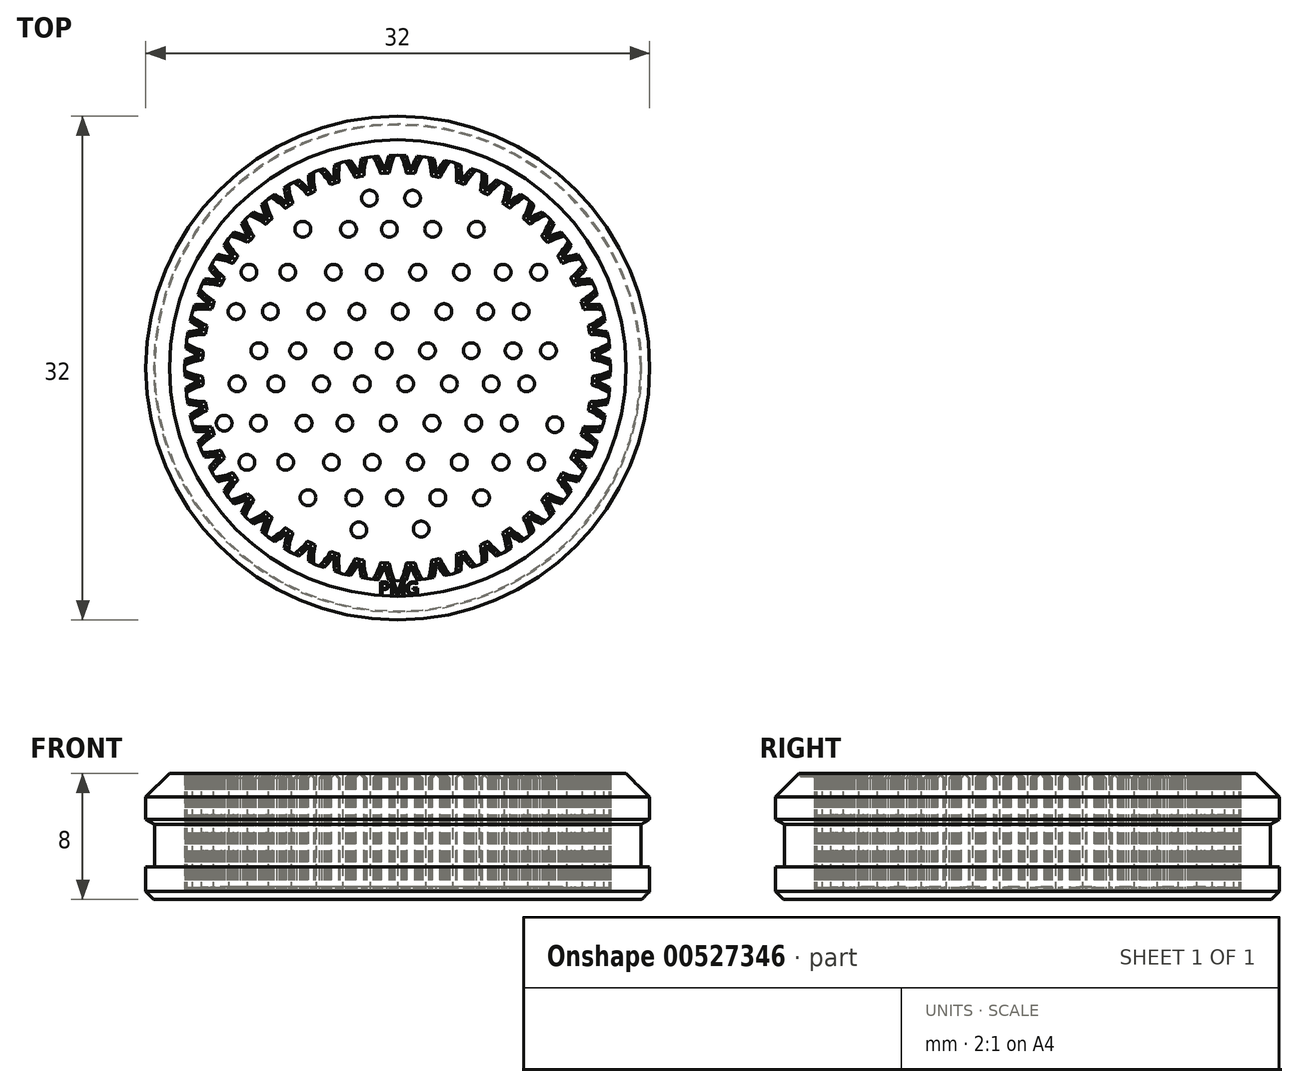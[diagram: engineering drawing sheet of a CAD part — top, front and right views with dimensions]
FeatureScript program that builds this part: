
annotation { "Feature Type Name" : "Feature", "Feature Type Description" : "" }
export const myFeature = defineFeature(function(context is Context, id is Id, definition is map)
    precondition{}
    {
        {
            var Q0;
            Q0=qCreatedBy(makeId("Top.planeOp"),FACE);
            var sketch = newSketch(context, id + "F0", { "sketchPlane" : qUnion([Q0])});
            skLineSegment(sketch, "E0", {"start": v(13.37, -1.96) * mm, "end": v(13.41, -1.77) * mm});
            skLineSegment(sketch, "E1", {"start": v(13.41, -1.77) * mm, "end": v(13.43, -1.57) * mm});
            skLineSegment(sketch, "E2", {"start": v(13.43, -1.57) * mm, "end": v(13.23, -1.46) * mm});
            skLineSegment(sketch, "E3", {"start": v(13.23, -1.46) * mm, "end": v(13.04, -1.36) * mm});
            skLineSegment(sketch, "E4", {"start": v(13.04, -1.36) * mm, "end": v(12.87, -1.28) * mm});
            skLineSegment(sketch, "E5", {"start": v(12.87, -1.28) * mm, "end": v(12.72, -1.21) * mm});
            skLineSegment(sketch, "E6", {"start": v(12.72, -1.21) * mm, "end": v(12.59, -1.16) * mm});
            skLineSegment(sketch, "E7", {"start": v(12.59, -1.16) * mm, "end": v(12.42, -1.11) * mm});
            skLineSegment(sketch, "E8", {"start": v(12.42, -1.11) * mm, "end": v(12.38, -1.09) * mm});
            skLineSegment(sketch, "E9", {"start": v(12.38, -1.09) * mm, "end": v(12.35, -1.06) * mm});
            skLineSegment(sketch, "E10", {"start": v(12.35, -1.06) * mm, "end": v(12.39, -0.56) * mm});
            skLineSegment(sketch, "E11", {"start": v(12.39, -0.56) * mm, "end": v(12.41, -0.54) * mm});
            skLineSegment(sketch, "E12", {"start": v(12.41, -0.54) * mm, "end": v(12.46, -0.52) * mm});
            skLineSegment(sketch, "E13", {"start": v(12.46, -0.52) * mm, "end": v(12.63, -0.49) * mm});
            skLineSegment(sketch, "E14", {"start": v(12.63, -0.49) * mm, "end": v(12.77, -0.46) * mm});
            skLineSegment(sketch, "E15", {"start": v(12.77, -0.46) * mm, "end": v(12.93, -0.41) * mm});
            skLineSegment(sketch, "E16", {"start": v(12.93, -0.41) * mm, "end": v(13.11, -0.36) * mm});
            skLineSegment(sketch, "E17", {"start": v(13.11, -0.36) * mm, "end": v(13.3, -0.28) * mm});
            skLineSegment(sketch, "E18", {"start": v(13.3, -0.28) * mm, "end": v(13.52, -0.2) * mm});
            skLineSegment(sketch, "E19", {"start": v(13.52, -0.2) * mm, "end": v(13.53, 0) * mm});
            skLineSegment(sketch, "E20", {"start": v(13.53, 0) * mm, "end": v(13.52, 0.2) * mm});
            skLineSegment(sketch, "E21", {"start": v(13.52, 0.2) * mm, "end": v(13.3, 0.28) * mm});
            skLineSegment(sketch, "E22", {"start": v(13.3, 0.28) * mm, "end": v(13.11, 0.36) * mm});
            skLineSegment(sketch, "E23", {"start": v(13.11, 0.36) * mm, "end": v(12.93, 0.41) * mm});
            skLineSegment(sketch, "E24", {"start": v(12.93, 0.41) * mm, "end": v(12.77, 0.46) * mm});
            skLineSegment(sketch, "E25", {"start": v(12.77, 0.46) * mm, "end": v(12.63, 0.49) * mm});
            skLineSegment(sketch, "E26", {"start": v(12.63, 0.49) * mm, "end": v(12.46, 0.52) * mm});
            skLineSegment(sketch, "E27", {"start": v(12.46, 0.52) * mm, "end": v(12.41, 0.54) * mm});
            skLineSegment(sketch, "E28", {"start": v(12.41, 0.54) * mm, "end": v(12.39, 0.56) * mm});
            skLineSegment(sketch, "E29", {"start": v(12.39, 0.56) * mm, "end": v(12.35, 1.06) * mm});
            skLineSegment(sketch, "E30", {"start": v(12.35, 1.06) * mm, "end": v(12.38, 1.09) * mm});
            skLineSegment(sketch, "E31", {"start": v(12.38, 1.09) * mm, "end": v(12.42, 1.11) * mm});
            skLineSegment(sketch, "E32", {"start": v(12.42, 1.11) * mm, "end": v(12.59, 1.16) * mm});
            skLineSegment(sketch, "E33", {"start": v(12.59, 1.16) * mm, "end": v(12.72, 1.21) * mm});
            skLineSegment(sketch, "E34", {"start": v(12.72, 1.21) * mm, "end": v(12.87, 1.28) * mm});
            skLineSegment(sketch, "E35", {"start": v(12.87, 1.28) * mm, "end": v(13.04, 1.36) * mm});
            skLineSegment(sketch, "E36", {"start": v(13.04, 1.36) * mm, "end": v(13.23, 1.46) * mm});
            skLineSegment(sketch, "E37", {"start": v(13.23, 1.46) * mm, "end": v(13.43, 1.57) * mm});
            skLineSegment(sketch, "E38", {"start": v(13.43, 1.57) * mm, "end": v(13.41, 1.77) * mm});
            skLineSegment(sketch, "E39", {"start": v(13.41, 1.77) * mm, "end": v(13.37, 1.96) * mm});
            skLineSegment(sketch, "E40", {"start": v(13.37, 1.96) * mm, "end": v(13.16, 2.02) * mm});
            skLineSegment(sketch, "E41", {"start": v(13.16, 2.02) * mm, "end": v(12.95, 2.07) * mm});
            skLineSegment(sketch, "E42", {"start": v(12.95, 2.07) * mm, "end": v(12.77, 2.1) * mm});
            skLineSegment(sketch, "E43", {"start": v(12.77, 2.1) * mm, "end": v(12.6, 2.12) * mm});
            skLineSegment(sketch, "E44", {"start": v(12.6, 2.12) * mm, "end": v(12.46, 2.13) * mm});
            skLineSegment(sketch, "E45", {"start": v(12.46, 2.13) * mm, "end": v(12.29, 2.14) * mm});
            skLineSegment(sketch, "E46", {"start": v(12.29, 2.14) * mm, "end": v(12.23, 2.15) * mm});
            skLineSegment(sketch, "E47", {"start": v(12.23, 2.15) * mm, "end": v(12.2, 2.17) * mm});
            skLineSegment(sketch, "E48", {"start": v(12.2, 2.17) * mm, "end": v(12.1, 2.66) * mm});
            skLineSegment(sketch, "E49", {"start": v(12.1, 2.66) * mm, "end": v(12.13, 2.7) * mm});
            skLineSegment(sketch, "E50", {"start": v(12.13, 2.7) * mm, "end": v(12.17, 2.72) * mm});
            skLineSegment(sketch, "E51", {"start": v(12.17, 2.72) * mm, "end": v(12.33, 2.8) * mm});
            skLineSegment(sketch, "E52", {"start": v(12.33, 2.8) * mm, "end": v(12.46, 2.86) * mm});
            skLineSegment(sketch, "E53", {"start": v(12.46, 2.86) * mm, "end": v(12.6, 2.95) * mm});
            skLineSegment(sketch, "E54", {"start": v(12.6, 2.95) * mm, "end": v(12.76, 3.05) * mm});
            skLineSegment(sketch, "E55", {"start": v(12.76, 3.05) * mm, "end": v(12.93, 3.17) * mm});
            skLineSegment(sketch, "E56", {"start": v(12.93, 3.17) * mm, "end": v(13.1, 3.3) * mm});
            skLineSegment(sketch, "E57", {"start": v(13.1, 3.3) * mm, "end": v(13.07, 3.5) * mm});
            skLineSegment(sketch, "E58", {"start": v(13.07, 3.5) * mm, "end": v(13, 3.69) * mm});
            skLineSegment(sketch, "E59", {"start": v(13, 3.69) * mm, "end": v(12.78, 3.72) * mm});
            skLineSegment(sketch, "E60", {"start": v(12.78, 3.72) * mm, "end": v(12.57, 3.74) * mm});
            skLineSegment(sketch, "E61", {"start": v(12.57, 3.74) * mm, "end": v(12.38, 3.75) * mm});
            skLineSegment(sketch, "E62", {"start": v(12.38, 3.75) * mm, "end": v(12.22, 3.75) * mm});
            skLineSegment(sketch, "E63", {"start": v(12.22, 3.75) * mm, "end": v(12.08, 3.74) * mm});
            skLineSegment(sketch, "E64", {"start": v(12.08, 3.74) * mm, "end": v(11.9, 3.73) * mm});
            skLineSegment(sketch, "E65", {"start": v(11.9, 3.73) * mm, "end": v(11.85, 3.73) * mm});
            skLineSegment(sketch, "E66", {"start": v(11.85, 3.73) * mm, "end": v(11.82, 3.75) * mm});
            skLineSegment(sketch, "E67", {"start": v(11.82, 3.75) * mm, "end": v(11.66, 4.22) * mm});
            skLineSegment(sketch, "E68", {"start": v(11.66, 4.22) * mm, "end": v(11.67, 4.25) * mm});
            skLineSegment(sketch, "E69", {"start": v(11.67, 4.25) * mm, "end": v(11.71, 4.29) * mm});
            skLineSegment(sketch, "E70", {"start": v(11.71, 4.29) * mm, "end": v(11.86, 4.38) * mm});
            skLineSegment(sketch, "E71", {"start": v(11.86, 4.38) * mm, "end": v(11.97, 4.47) * mm});
            skLineSegment(sketch, "E72", {"start": v(11.97, 4.47) * mm, "end": v(12.1, 4.57) * mm});
            skLineSegment(sketch, "E73", {"start": v(12.1, 4.57) * mm, "end": v(12.25, 4.69) * mm});
            skLineSegment(sketch, "E74", {"start": v(12.25, 4.69) * mm, "end": v(12.4, 4.83) * mm});
            skLineSegment(sketch, "E75", {"start": v(12.4, 4.83) * mm, "end": v(12.56, 4.99) * mm});
            skLineSegment(sketch, "E76", {"start": v(12.56, 4.99) * mm, "end": v(12.5, 5.18) * mm});
            skLineSegment(sketch, "E77", {"start": v(12.5, 5.18) * mm, "end": v(12.41, 5.36) * mm});
            skLineSegment(sketch, "E78", {"start": v(12.41, 5.36) * mm, "end": v(12.19, 5.36) * mm});
            skLineSegment(sketch, "E79", {"start": v(12.19, 5.36) * mm, "end": v(11.98, 5.35) * mm});
            skLineSegment(sketch, "E80", {"start": v(11.98, 5.35) * mm, "end": v(11.79, 5.33) * mm});
            skLineSegment(sketch, "E81", {"start": v(11.79, 5.33) * mm, "end": v(11.62, 5.31) * mm});
            skLineSegment(sketch, "E82", {"start": v(11.62, 5.31) * mm, "end": v(11.49, 5.29) * mm});
            skLineSegment(sketch, "E83", {"start": v(11.49, 5.29) * mm, "end": v(11.31, 5.25) * mm});
            skLineSegment(sketch, "E84", {"start": v(11.31, 5.25) * mm, "end": v(11.26, 5.25) * mm});
            skLineSegment(sketch, "E85", {"start": v(11.26, 5.25) * mm, "end": v(11.23, 5.26) * mm});
            skLineSegment(sketch, "E86", {"start": v(11.23, 5.26) * mm, "end": v(11, 5.7) * mm});
            skLineSegment(sketch, "E87", {"start": v(11, 5.7) * mm, "end": v(11.02, 5.74) * mm});
            skLineSegment(sketch, "E88", {"start": v(11.02, 5.74) * mm, "end": v(11.05, 5.78) * mm});
            skLineSegment(sketch, "E89", {"start": v(11.05, 5.78) * mm, "end": v(11.19, 5.9) * mm});
            skLineSegment(sketch, "E90", {"start": v(11.19, 5.9) * mm, "end": v(11.29, 5.99) * mm});
            skLineSegment(sketch, "E91", {"start": v(11.29, 5.99) * mm, "end": v(11.4, 6.1) * mm});
            skLineSegment(sketch, "E92", {"start": v(11.4, 6.1) * mm, "end": v(11.53, 6.25) * mm});
            skLineSegment(sketch, "E93", {"start": v(11.53, 6.25) * mm, "end": v(11.67, 6.4) * mm});
            skLineSegment(sketch, "E94", {"start": v(11.67, 6.4) * mm, "end": v(11.8, 6.59) * mm});
            skLineSegment(sketch, "E95", {"start": v(11.8, 6.59) * mm, "end": v(11.72, 6.76) * mm});
            skLineSegment(sketch, "E96", {"start": v(11.72, 6.76) * mm, "end": v(11.6, 6.93) * mm});
            skLineSegment(sketch, "E97", {"start": v(11.6, 6.93) * mm, "end": v(11.38, 6.9) * mm});
            skLineSegment(sketch, "E98", {"start": v(11.38, 6.9) * mm, "end": v(11.18, 6.86) * mm});
            skLineSegment(sketch, "E99", {"start": v(11.18, 6.86) * mm, "end": v(11, 6.82) * mm});
            skLineSegment(sketch, "E100", {"start": v(11, 6.82) * mm, "end": v(10.83, 6.78) * mm});
            skLineSegment(sketch, "E101", {"start": v(10.83, 6.78) * mm, "end": v(10.7, 6.74) * mm});
            skLineSegment(sketch, "E102", {"start": v(10.7, 6.74) * mm, "end": v(10.53, 6.68) * mm});
            skLineSegment(sketch, "E103", {"start": v(10.53, 6.68) * mm, "end": v(10.48, 6.67) * mm});
            skLineSegment(sketch, "E104", {"start": v(10.48, 6.67) * mm, "end": v(10.45, 6.68) * mm});
            skLineSegment(sketch, "E105", {"start": v(10.45, 6.68) * mm, "end": v(10.17, 7.1) * mm});
            skLineSegment(sketch, "E106", {"start": v(10.17, 7.1) * mm, "end": v(10.17, 7.13) * mm});
            skLineSegment(sketch, "E107", {"start": v(10.17, 7.13) * mm, "end": v(10.2, 7.17) * mm});
            skLineSegment(sketch, "E108", {"start": v(10.2, 7.17) * mm, "end": v(10.32, 7.3) * mm});
            skLineSegment(sketch, "E109", {"start": v(10.32, 7.3) * mm, "end": v(10.41, 7.41) * mm});
            skLineSegment(sketch, "E110", {"start": v(10.41, 7.41) * mm, "end": v(10.51, 7.54) * mm});
            skLineSegment(sketch, "E111", {"start": v(10.51, 7.54) * mm, "end": v(10.62, 7.7) * mm});
            skLineSegment(sketch, "E112", {"start": v(10.62, 7.7) * mm, "end": v(10.73, 7.88) * mm});
            skLineSegment(sketch, "E113", {"start": v(10.73, 7.88) * mm, "end": v(10.84, 8.07) * mm});
            skLineSegment(sketch, "E114", {"start": v(10.84, 8.07) * mm, "end": v(10.73, 8.24) * mm});
            skLineSegment(sketch, "E115", {"start": v(10.73, 8.24) * mm, "end": v(10.6, 8.39) * mm});
            skLineSegment(sketch, "E116", {"start": v(10.6, 8.39) * mm, "end": v(10.39, 8.33) * mm});
            skLineSegment(sketch, "E117", {"start": v(10.39, 8.33) * mm, "end": v(10.18, 8.26) * mm});
            skLineSegment(sketch, "E118", {"start": v(10.18, 8.26) * mm, "end": v(10, 8.2) * mm});
            skLineSegment(sketch, "E119", {"start": v(10, 8.2) * mm, "end": v(9.85, 8.14) * mm});
            skLineSegment(sketch, "E120", {"start": v(9.85, 8.14) * mm, "end": v(9.73, 8.08) * mm});
            skLineSegment(sketch, "E121", {"start": v(9.73, 8.08) * mm, "end": v(9.57, 8) * mm});
            skLineSegment(sketch, "E122", {"start": v(9.57, 8) * mm, "end": v(9.52, 7.98) * mm});
            skLineSegment(sketch, "E123", {"start": v(9.52, 7.98) * mm, "end": v(9.48, 7.99) * mm});
            skLineSegment(sketch, "E124", {"start": v(9.48, 7.99) * mm, "end": v(9.16, 8.36) * mm});
            skLineSegment(sketch, "E125", {"start": v(9.16, 8.36) * mm, "end": v(9.16, 8.4) * mm});
            skLineSegment(sketch, "E126", {"start": v(9.16, 8.4) * mm, "end": v(9.18, 8.44) * mm});
            skLineSegment(sketch, "E127", {"start": v(9.18, 8.44) * mm, "end": v(9.28, 8.59) * mm});
            skLineSegment(sketch, "E128", {"start": v(9.28, 8.59) * mm, "end": v(9.35, 8.7) * mm});
            skLineSegment(sketch, "E129", {"start": v(9.35, 8.7) * mm, "end": v(9.44, 8.85) * mm});
            skLineSegment(sketch, "E130", {"start": v(9.44, 8.85) * mm, "end": v(9.52, 9.02) * mm});
            skLineSegment(sketch, "E131", {"start": v(9.52, 9.02) * mm, "end": v(9.61, 9.2) * mm});
            skLineSegment(sketch, "E132", {"start": v(9.61, 9.2) * mm, "end": v(9.7, 9.42) * mm});
            skLineSegment(sketch, "E133", {"start": v(9.7, 9.42) * mm, "end": v(9.57, 9.57) * mm});
            skLineSegment(sketch, "E134", {"start": v(9.57, 9.57) * mm, "end": v(9.42, 9.7) * mm});
            skLineSegment(sketch, "E135", {"start": v(9.42, 9.7) * mm, "end": v(9.2, 9.61) * mm});
            skLineSegment(sketch, "E136", {"start": v(9.2, 9.61) * mm, "end": v(9.02, 9.52) * mm});
            skLineSegment(sketch, "E137", {"start": v(9.02, 9.52) * mm, "end": v(8.85, 9.44) * mm});
            skLineSegment(sketch, "E138", {"start": v(8.85, 9.44) * mm, "end": v(8.7, 9.35) * mm});
            skLineSegment(sketch, "E139", {"start": v(8.7, 9.35) * mm, "end": v(8.59, 9.28) * mm});
            skLineSegment(sketch, "E140", {"start": v(8.59, 9.28) * mm, "end": v(8.44, 9.18) * mm});
            skLineSegment(sketch, "E141", {"start": v(8.44, 9.18) * mm, "end": v(8.4, 9.16) * mm});
            skLineSegment(sketch, "E142", {"start": v(8.4, 9.16) * mm, "end": v(8.36, 9.16) * mm});
            skLineSegment(sketch, "E143", {"start": v(8.36, 9.16) * mm, "end": v(7.99, 9.48) * mm});
            skLineSegment(sketch, "E144", {"start": v(7.99, 9.48) * mm, "end": v(7.98, 9.52) * mm});
            skLineSegment(sketch, "E145", {"start": v(7.98, 9.52) * mm, "end": v(8, 9.57) * mm});
            skLineSegment(sketch, "E146", {"start": v(8, 9.57) * mm, "end": v(8.08, 9.73) * mm});
            skLineSegment(sketch, "E147", {"start": v(8.08, 9.73) * mm, "end": v(8.14, 9.85) * mm});
            skLineSegment(sketch, "E148", {"start": v(8.14, 9.85) * mm, "end": v(8.2, 10) * mm});
            skLineSegment(sketch, "E149", {"start": v(8.2, 10) * mm, "end": v(8.26, 10.18) * mm});
            skLineSegment(sketch, "E150", {"start": v(8.26, 10.18) * mm, "end": v(8.33, 10.39) * mm});
            skLineSegment(sketch, "E151", {"start": v(8.33, 10.39) * mm, "end": v(8.39, 10.6) * mm});
            skLineSegment(sketch, "E152", {"start": v(8.39, 10.6) * mm, "end": v(8.24, 10.73) * mm});
            skLineSegment(sketch, "E153", {"start": v(8.24, 10.73) * mm, "end": v(8.07, 10.84) * mm});
            skLineSegment(sketch, "E154", {"start": v(8.07, 10.84) * mm, "end": v(7.88, 10.73) * mm});
            skLineSegment(sketch, "E155", {"start": v(7.88, 10.73) * mm, "end": v(7.7, 10.62) * mm});
            skLineSegment(sketch, "E156", {"start": v(7.7, 10.62) * mm, "end": v(7.54, 10.51) * mm});
            skLineSegment(sketch, "E157", {"start": v(7.54, 10.51) * mm, "end": v(7.41, 10.41) * mm});
            skLineSegment(sketch, "E158", {"start": v(7.41, 10.41) * mm, "end": v(7.3, 10.32) * mm});
            skLineSegment(sketch, "E159", {"start": v(7.3, 10.32) * mm, "end": v(7.17, 10.2) * mm});
            skLineSegment(sketch, "E160", {"start": v(7.17, 10.2) * mm, "end": v(7.13, 10.17) * mm});
            skLineSegment(sketch, "E161", {"start": v(7.13, 10.17) * mm, "end": v(7.1, 10.17) * mm});
            skLineSegment(sketch, "E162", {"start": v(7.1, 10.17) * mm, "end": v(6.68, 10.45) * mm});
            skLineSegment(sketch, "E163", {"start": v(6.68, 10.45) * mm, "end": v(6.67, 10.48) * mm});
            skLineSegment(sketch, "E164", {"start": v(6.67, 10.48) * mm, "end": v(6.68, 10.53) * mm});
            skLineSegment(sketch, "E165", {"start": v(6.68, 10.53) * mm, "end": v(6.74, 10.7) * mm});
            skLineSegment(sketch, "E166", {"start": v(6.74, 10.7) * mm, "end": v(6.78, 10.83) * mm});
            skLineSegment(sketch, "E167", {"start": v(6.78, 10.83) * mm, "end": v(6.82, 11) * mm});
            skLineSegment(sketch, "E168", {"start": v(6.82, 11) * mm, "end": v(6.86, 11.18) * mm});
            skLineSegment(sketch, "E169", {"start": v(6.86, 11.18) * mm, "end": v(6.9, 11.38) * mm});
            skLineSegment(sketch, "E170", {"start": v(6.9, 11.38) * mm, "end": v(6.93, 11.6) * mm});
            skLineSegment(sketch, "E171", {"start": v(6.93, 11.6) * mm, "end": v(6.76, 11.72) * mm});
            skLineSegment(sketch, "E172", {"start": v(6.76, 11.72) * mm, "end": v(6.59, 11.8) * mm});
            skLineSegment(sketch, "E173", {"start": v(6.59, 11.8) * mm, "end": v(6.4, 11.67) * mm});
            skLineSegment(sketch, "E174", {"start": v(6.4, 11.67) * mm, "end": v(6.25, 11.53) * mm});
            skLineSegment(sketch, "E175", {"start": v(6.25, 11.53) * mm, "end": v(6.1, 11.4) * mm});
            skLineSegment(sketch, "E176", {"start": v(6.1, 11.4) * mm, "end": v(5.99, 11.29) * mm});
            skLineSegment(sketch, "E177", {"start": v(5.99, 11.29) * mm, "end": v(5.9, 11.19) * mm});
            skLineSegment(sketch, "E178", {"start": v(5.9, 11.19) * mm, "end": v(5.78, 11.05) * mm});
            skLineSegment(sketch, "E179", {"start": v(5.78, 11.05) * mm, "end": v(5.74, 11.02) * mm});
            skLineSegment(sketch, "E180", {"start": v(5.74, 11.02) * mm, "end": v(5.7, 11) * mm});
            skLineSegment(sketch, "E181", {"start": v(5.7, 11) * mm, "end": v(5.26, 11.23) * mm});
            skLineSegment(sketch, "E182", {"start": v(5.26, 11.23) * mm, "end": v(5.25, 11.26) * mm});
            skLineSegment(sketch, "E183", {"start": v(5.25, 11.26) * mm, "end": v(5.25, 11.31) * mm});
            skLineSegment(sketch, "E184", {"start": v(5.25, 11.31) * mm, "end": v(5.29, 11.49) * mm});
            skLineSegment(sketch, "E185", {"start": v(5.29, 11.49) * mm, "end": v(5.31, 11.62) * mm});
            skLineSegment(sketch, "E186", {"start": v(5.31, 11.62) * mm, "end": v(5.33, 11.79) * mm});
            skLineSegment(sketch, "E187", {"start": v(5.33, 11.79) * mm, "end": v(5.35, 11.98) * mm});
            skLineSegment(sketch, "E188", {"start": v(5.35, 11.98) * mm, "end": v(5.36, 12.19) * mm});
            skLineSegment(sketch, "E189", {"start": v(5.36, 12.19) * mm, "end": v(5.36, 12.41) * mm});
            skLineSegment(sketch, "E190", {"start": v(5.36, 12.41) * mm, "end": v(5.18, 12.5) * mm});
            skLineSegment(sketch, "E191", {"start": v(5.18, 12.5) * mm, "end": v(4.99, 12.56) * mm});
            skLineSegment(sketch, "E192", {"start": v(4.99, 12.56) * mm, "end": v(4.83, 12.4) * mm});
            skLineSegment(sketch, "E193", {"start": v(4.83, 12.4) * mm, "end": v(4.69, 12.25) * mm});
            skLineSegment(sketch, "E194", {"start": v(4.69, 12.25) * mm, "end": v(4.57, 12.1) * mm});
            skLineSegment(sketch, "E195", {"start": v(4.57, 12.1) * mm, "end": v(4.47, 11.97) * mm});
            skLineSegment(sketch, "E196", {"start": v(4.47, 11.97) * mm, "end": v(4.38, 11.86) * mm});
            skLineSegment(sketch, "E197", {"start": v(4.38, 11.86) * mm, "end": v(4.29, 11.71) * mm});
            skLineSegment(sketch, "E198", {"start": v(4.29, 11.71) * mm, "end": v(4.25, 11.67) * mm});
            skLineSegment(sketch, "E199", {"start": v(4.25, 11.67) * mm, "end": v(4.22, 11.66) * mm});
            skLineSegment(sketch, "E200", {"start": v(4.22, 11.66) * mm, "end": v(3.75, 11.82) * mm});
            skLineSegment(sketch, "E201", {"start": v(3.75, 11.82) * mm, "end": v(3.73, 11.85) * mm});
            skLineSegment(sketch, "E202", {"start": v(3.73, 11.85) * mm, "end": v(3.73, 11.9) * mm});
            skLineSegment(sketch, "E203", {"start": v(3.73, 11.9) * mm, "end": v(3.74, 12.08) * mm});
            skLineSegment(sketch, "E204", {"start": v(3.74, 12.08) * mm, "end": v(3.75, 12.22) * mm});
            skLineSegment(sketch, "E205", {"start": v(3.75, 12.22) * mm, "end": v(3.75, 12.38) * mm});
            skLineSegment(sketch, "E206", {"start": v(3.75, 12.38) * mm, "end": v(3.74, 12.57) * mm});
            skLineSegment(sketch, "E207", {"start": v(3.74, 12.57) * mm, "end": v(3.72, 12.78) * mm});
            skLineSegment(sketch, "E208", {"start": v(3.72, 12.78) * mm, "end": v(3.69, 13) * mm});
            skLineSegment(sketch, "E209", {"start": v(3.69, 13) * mm, "end": v(3.5, 13.07) * mm});
            skLineSegment(sketch, "E210", {"start": v(3.5, 13.07) * mm, "end": v(3.3, 13.1) * mm});
            skLineSegment(sketch, "E211", {"start": v(3.3, 13.1) * mm, "end": v(3.17, 12.93) * mm});
            skLineSegment(sketch, "E212", {"start": v(3.17, 12.93) * mm, "end": v(3.05, 12.76) * mm});
            skLineSegment(sketch, "E213", {"start": v(3.05, 12.76) * mm, "end": v(2.95, 12.6) * mm});
            skLineSegment(sketch, "E214", {"start": v(2.95, 12.6) * mm, "end": v(2.86, 12.46) * mm});
            skLineSegment(sketch, "E215", {"start": v(2.86, 12.46) * mm, "end": v(2.8, 12.33) * mm});
            skLineSegment(sketch, "E216", {"start": v(2.8, 12.33) * mm, "end": v(2.72, 12.17) * mm});
            skLineSegment(sketch, "E217", {"start": v(2.72, 12.17) * mm, "end": v(2.7, 12.13) * mm});
            skLineSegment(sketch, "E218", {"start": v(2.7, 12.13) * mm, "end": v(2.66, 12.1) * mm});
            skLineSegment(sketch, "E219", {"start": v(2.66, 12.1) * mm, "end": v(2.17, 12.2) * mm});
            skLineSegment(sketch, "E220", {"start": v(2.17, 12.2) * mm, "end": v(2.15, 12.23) * mm});
            skLineSegment(sketch, "E221", {"start": v(2.15, 12.23) * mm, "end": v(2.14, 12.29) * mm});
            skLineSegment(sketch, "E222", {"start": v(2.14, 12.29) * mm, "end": v(2.13, 12.46) * mm});
            skLineSegment(sketch, "E223", {"start": v(2.13, 12.46) * mm, "end": v(2.12, 12.6) * mm});
            skLineSegment(sketch, "E224", {"start": v(2.12, 12.6) * mm, "end": v(2.1, 12.77) * mm});
            skLineSegment(sketch, "E225", {"start": v(2.1, 12.77) * mm, "end": v(2.07, 12.95) * mm});
            skLineSegment(sketch, "E226", {"start": v(2.07, 12.95) * mm, "end": v(2.02, 13.16) * mm});
            skLineSegment(sketch, "E227", {"start": v(2.02, 13.16) * mm, "end": v(1.96, 13.37) * mm});
            skLineSegment(sketch, "E228", {"start": v(1.96, 13.37) * mm, "end": v(1.77, 13.41) * mm});
            skLineSegment(sketch, "E229", {"start": v(1.77, 13.41) * mm, "end": v(1.57, 13.43) * mm});
            skLineSegment(sketch, "E230", {"start": v(1.57, 13.43) * mm, "end": v(1.46, 13.23) * mm});
            skLineSegment(sketch, "E231", {"start": v(1.46, 13.23) * mm, "end": v(1.36, 13.04) * mm});
            skLineSegment(sketch, "E232", {"start": v(1.36, 13.04) * mm, "end": v(1.28, 12.87) * mm});
            skLineSegment(sketch, "E233", {"start": v(1.28, 12.87) * mm, "end": v(1.21, 12.72) * mm});
            skLineSegment(sketch, "E234", {"start": v(1.21, 12.72) * mm, "end": v(1.16, 12.59) * mm});
            skLineSegment(sketch, "E235", {"start": v(1.16, 12.59) * mm, "end": v(1.11, 12.42) * mm});
            skLineSegment(sketch, "E236", {"start": v(1.11, 12.42) * mm, "end": v(1.09, 12.38) * mm});
            skLineSegment(sketch, "E237", {"start": v(1.09, 12.38) * mm, "end": v(1.06, 12.35) * mm});
            skLineSegment(sketch, "E238", {"start": v(1.06, 12.35) * mm, "end": v(0.56, 12.39) * mm});
            skLineSegment(sketch, "E239", {"start": v(0.56, 12.39) * mm, "end": v(0.54, 12.41) * mm});
            skLineSegment(sketch, "E240", {"start": v(0.54, 12.41) * mm, "end": v(0.52, 12.46) * mm});
            skLineSegment(sketch, "E241", {"start": v(0.52, 12.46) * mm, "end": v(0.49, 12.63) * mm});
            skLineSegment(sketch, "E242", {"start": v(0.49, 12.63) * mm, "end": v(0.46, 12.77) * mm});
            skLineSegment(sketch, "E243", {"start": v(0.46, 12.77) * mm, "end": v(0.41, 12.93) * mm});
            skLineSegment(sketch, "E244", {"start": v(0.41, 12.93) * mm, "end": v(0.36, 13.11) * mm});
            skLineSegment(sketch, "E245", {"start": v(0.36, 13.11) * mm, "end": v(0.28, 13.3) * mm});
            skLineSegment(sketch, "E246", {"start": v(0.28, 13.3) * mm, "end": v(0.2, 13.52) * mm});
            skLineSegment(sketch, "E247", {"start": v(0.2, 13.52) * mm, "end": v(0, 13.53) * mm});
            skLineSegment(sketch, "E248", {"start": v(0, 13.53) * mm, "end": v(-0.2, 13.52) * mm});
            skLineSegment(sketch, "E249", {"start": v(-0.2, 13.52) * mm, "end": v(-0.28, 13.3) * mm});
            skLineSegment(sketch, "E250", {"start": v(-0.28, 13.3) * mm, "end": v(-0.36, 13.11) * mm});
            skLineSegment(sketch, "E251", {"start": v(-0.36, 13.11) * mm, "end": v(-0.41, 12.93) * mm});
            skLineSegment(sketch, "E252", {"start": v(-0.41, 12.93) * mm, "end": v(-0.46, 12.77) * mm});
            skLineSegment(sketch, "E253", {"start": v(-0.46, 12.77) * mm, "end": v(-0.49, 12.63) * mm});
            skLineSegment(sketch, "E254", {"start": v(-0.49, 12.63) * mm, "end": v(-0.52, 12.46) * mm});
            skLineSegment(sketch, "E255", {"start": v(-0.52, 12.46) * mm, "end": v(-0.54, 12.41) * mm});
            skLineSegment(sketch, "E256", {"start": v(-0.54, 12.41) * mm, "end": v(-0.56, 12.39) * mm});
            skLineSegment(sketch, "E257", {"start": v(-0.56, 12.39) * mm, "end": v(-1.06, 12.35) * mm});
            skLineSegment(sketch, "E258", {"start": v(-1.06, 12.35) * mm, "end": v(-1.09, 12.38) * mm});
            skLineSegment(sketch, "E259", {"start": v(-1.09, 12.38) * mm, "end": v(-1.11, 12.42) * mm});
            skLineSegment(sketch, "E260", {"start": v(-1.11, 12.42) * mm, "end": v(-1.16, 12.59) * mm});
            skLineSegment(sketch, "E261", {"start": v(-1.16, 12.59) * mm, "end": v(-1.21, 12.72) * mm});
            skLineSegment(sketch, "E262", {"start": v(-1.21, 12.72) * mm, "end": v(-1.28, 12.87) * mm});
            skLineSegment(sketch, "E263", {"start": v(-1.28, 12.87) * mm, "end": v(-1.36, 13.04) * mm});
            skLineSegment(sketch, "E264", {"start": v(-1.36, 13.04) * mm, "end": v(-1.46, 13.23) * mm});
            skLineSegment(sketch, "E265", {"start": v(-1.46, 13.23) * mm, "end": v(-1.57, 13.43) * mm});
            skLineSegment(sketch, "E266", {"start": v(-1.57, 13.43) * mm, "end": v(-1.77, 13.41) * mm});
            skLineSegment(sketch, "E267", {"start": v(-1.77, 13.41) * mm, "end": v(-1.96, 13.37) * mm});
            skLineSegment(sketch, "E268", {"start": v(-1.96, 13.37) * mm, "end": v(-2.02, 13.16) * mm});
            skLineSegment(sketch, "E269", {"start": v(-2.02, 13.16) * mm, "end": v(-2.07, 12.95) * mm});
            skLineSegment(sketch, "E270", {"start": v(-2.07, 12.95) * mm, "end": v(-2.1, 12.77) * mm});
            skLineSegment(sketch, "E271", {"start": v(-2.1, 12.77) * mm, "end": v(-2.12, 12.6) * mm});
            skLineSegment(sketch, "E272", {"start": v(-2.12, 12.6) * mm, "end": v(-2.13, 12.46) * mm});
            skLineSegment(sketch, "E273", {"start": v(-2.13, 12.46) * mm, "end": v(-2.14, 12.29) * mm});
            skLineSegment(sketch, "E274", {"start": v(-2.14, 12.29) * mm, "end": v(-2.15, 12.23) * mm});
            skLineSegment(sketch, "E275", {"start": v(-2.15, 12.23) * mm, "end": v(-2.17, 12.2) * mm});
            skLineSegment(sketch, "E276", {"start": v(-2.17, 12.2) * mm, "end": v(-2.66, 12.1) * mm});
            skLineSegment(sketch, "E277", {"start": v(-2.66, 12.1) * mm, "end": v(-2.7, 12.13) * mm});
            skLineSegment(sketch, "E278", {"start": v(-2.7, 12.13) * mm, "end": v(-2.72, 12.17) * mm});
            skLineSegment(sketch, "E279", {"start": v(-2.72, 12.17) * mm, "end": v(-2.8, 12.33) * mm});
            skLineSegment(sketch, "E280", {"start": v(-2.8, 12.33) * mm, "end": v(-2.86, 12.46) * mm});
            skLineSegment(sketch, "E281", {"start": v(-2.86, 12.46) * mm, "end": v(-2.95, 12.6) * mm});
            skLineSegment(sketch, "E282", {"start": v(-2.95, 12.6) * mm, "end": v(-3.05, 12.76) * mm});
            skLineSegment(sketch, "E283", {"start": v(-3.05, 12.76) * mm, "end": v(-3.17, 12.93) * mm});
            skLineSegment(sketch, "E284", {"start": v(-3.17, 12.93) * mm, "end": v(-3.3, 13.1) * mm});
            skLineSegment(sketch, "E285", {"start": v(-3.3, 13.1) * mm, "end": v(-3.5, 13.07) * mm});
            skLineSegment(sketch, "E286", {"start": v(-3.5, 13.07) * mm, "end": v(-3.69, 13) * mm});
            skLineSegment(sketch, "E287", {"start": v(-3.69, 13) * mm, "end": v(-3.72, 12.78) * mm});
            skLineSegment(sketch, "E288", {"start": v(-3.72, 12.78) * mm, "end": v(-3.74, 12.57) * mm});
            skLineSegment(sketch, "E289", {"start": v(-3.74, 12.57) * mm, "end": v(-3.75, 12.38) * mm});
            skLineSegment(sketch, "E290", {"start": v(-3.75, 12.38) * mm, "end": v(-3.75, 12.22) * mm});
            skLineSegment(sketch, "E291", {"start": v(-3.75, 12.22) * mm, "end": v(-3.74, 12.08) * mm});
            skLineSegment(sketch, "E292", {"start": v(-3.74, 12.08) * mm, "end": v(-3.73, 11.9) * mm});
            skLineSegment(sketch, "E293", {"start": v(-3.73, 11.9) * mm, "end": v(-3.73, 11.85) * mm});
            skLineSegment(sketch, "E294", {"start": v(-3.73, 11.85) * mm, "end": v(-3.75, 11.82) * mm});
            skLineSegment(sketch, "E295", {"start": v(-3.75, 11.82) * mm, "end": v(-4.22, 11.66) * mm});
            skLineSegment(sketch, "E296", {"start": v(-4.22, 11.66) * mm, "end": v(-4.25, 11.67) * mm});
            skLineSegment(sketch, "E297", {"start": v(-4.25, 11.67) * mm, "end": v(-4.29, 11.71) * mm});
            skLineSegment(sketch, "E298", {"start": v(-4.29, 11.71) * mm, "end": v(-4.38, 11.86) * mm});
            skLineSegment(sketch, "E299", {"start": v(-4.38, 11.86) * mm, "end": v(-4.47, 11.97) * mm});
            skLineSegment(sketch, "E300", {"start": v(-4.47, 11.97) * mm, "end": v(-4.57, 12.1) * mm});
            skLineSegment(sketch, "E301", {"start": v(-4.57, 12.1) * mm, "end": v(-4.69, 12.25) * mm});
            skLineSegment(sketch, "E302", {"start": v(-4.69, 12.25) * mm, "end": v(-4.83, 12.4) * mm});
            skLineSegment(sketch, "E303", {"start": v(-4.83, 12.4) * mm, "end": v(-4.99, 12.56) * mm});
            skLineSegment(sketch, "E304", {"start": v(-4.99, 12.56) * mm, "end": v(-5.18, 12.5) * mm});
            skLineSegment(sketch, "E305", {"start": v(-5.18, 12.5) * mm, "end": v(-5.36, 12.41) * mm});
            skLineSegment(sketch, "E306", {"start": v(-5.36, 12.41) * mm, "end": v(-5.36, 12.19) * mm});
            skLineSegment(sketch, "E307", {"start": v(-5.36, 12.19) * mm, "end": v(-5.35, 11.98) * mm});
            skLineSegment(sketch, "E308", {"start": v(-5.35, 11.98) * mm, "end": v(-5.33, 11.79) * mm});
            skLineSegment(sketch, "E309", {"start": v(-5.33, 11.79) * mm, "end": v(-5.31, 11.62) * mm});
            skLineSegment(sketch, "E310", {"start": v(-5.31, 11.62) * mm, "end": v(-5.29, 11.49) * mm});
            skLineSegment(sketch, "E311", {"start": v(-5.29, 11.49) * mm, "end": v(-5.25, 11.31) * mm});
            skLineSegment(sketch, "E312", {"start": v(-5.25, 11.31) * mm, "end": v(-5.25, 11.26) * mm});
            skLineSegment(sketch, "E313", {"start": v(-5.25, 11.26) * mm, "end": v(-5.26, 11.23) * mm});
            skLineSegment(sketch, "E314", {"start": v(-5.26, 11.23) * mm, "end": v(-5.7, 11) * mm});
            skLineSegment(sketch, "E315", {"start": v(-5.7, 11) * mm, "end": v(-5.74, 11.02) * mm});
            skLineSegment(sketch, "E316", {"start": v(-5.74, 11.02) * mm, "end": v(-5.78, 11.05) * mm});
            skLineSegment(sketch, "E317", {"start": v(-5.78, 11.05) * mm, "end": v(-5.9, 11.19) * mm});
            skLineSegment(sketch, "E318", {"start": v(-5.9, 11.19) * mm, "end": v(-5.99, 11.29) * mm});
            skLineSegment(sketch, "E319", {"start": v(-5.99, 11.29) * mm, "end": v(-6.1, 11.4) * mm});
            skLineSegment(sketch, "E320", {"start": v(-6.1, 11.4) * mm, "end": v(-6.25, 11.53) * mm});
            skLineSegment(sketch, "E321", {"start": v(-6.25, 11.53) * mm, "end": v(-6.4, 11.67) * mm});
            skLineSegment(sketch, "E322", {"start": v(-6.4, 11.67) * mm, "end": v(-6.59, 11.8) * mm});
            skLineSegment(sketch, "E323", {"start": v(-6.59, 11.8) * mm, "end": v(-6.76, 11.72) * mm});
            skLineSegment(sketch, "E324", {"start": v(-6.76, 11.72) * mm, "end": v(-6.93, 11.6) * mm});
            skLineSegment(sketch, "E325", {"start": v(-6.93, 11.6) * mm, "end": v(-6.9, 11.38) * mm});
            skLineSegment(sketch, "E326", {"start": v(-6.9, 11.38) * mm, "end": v(-6.86, 11.18) * mm});
            skLineSegment(sketch, "E327", {"start": v(-6.86, 11.18) * mm, "end": v(-6.82, 11) * mm});
            skLineSegment(sketch, "E328", {"start": v(-6.82, 11) * mm, "end": v(-6.78, 10.83) * mm});
            skLineSegment(sketch, "E329", {"start": v(-6.78, 10.83) * mm, "end": v(-6.74, 10.7) * mm});
            skLineSegment(sketch, "E330", {"start": v(-6.74, 10.7) * mm, "end": v(-6.68, 10.53) * mm});
            skLineSegment(sketch, "E331", {"start": v(-6.68, 10.53) * mm, "end": v(-6.67, 10.48) * mm});
            skLineSegment(sketch, "E332", {"start": v(-6.67, 10.48) * mm, "end": v(-6.68, 10.45) * mm});
            skLineSegment(sketch, "E333", {"start": v(-6.68, 10.45) * mm, "end": v(-7.1, 10.17) * mm});
            skLineSegment(sketch, "E334", {"start": v(-7.1, 10.17) * mm, "end": v(-7.13, 10.17) * mm});
            skLineSegment(sketch, "E335", {"start": v(-7.13, 10.17) * mm, "end": v(-7.17, 10.2) * mm});
            skLineSegment(sketch, "E336", {"start": v(-7.17, 10.2) * mm, "end": v(-7.3, 10.32) * mm});
            skLineSegment(sketch, "E337", {"start": v(-7.3, 10.32) * mm, "end": v(-7.41, 10.41) * mm});
            skLineSegment(sketch, "E338", {"start": v(-7.41, 10.41) * mm, "end": v(-7.54, 10.51) * mm});
            skLineSegment(sketch, "E339", {"start": v(-7.54, 10.51) * mm, "end": v(-7.7, 10.62) * mm});
            skLineSegment(sketch, "E340", {"start": v(-7.7, 10.62) * mm, "end": v(-7.88, 10.73) * mm});
            skLineSegment(sketch, "E341", {"start": v(-7.88, 10.73) * mm, "end": v(-8.07, 10.84) * mm});
            skLineSegment(sketch, "E342", {"start": v(-8.07, 10.84) * mm, "end": v(-8.24, 10.73) * mm});
            skLineSegment(sketch, "E343", {"start": v(-8.24, 10.73) * mm, "end": v(-8.39, 10.6) * mm});
            skLineSegment(sketch, "E344", {"start": v(-8.39, 10.6) * mm, "end": v(-8.33, 10.39) * mm});
            skLineSegment(sketch, "E345", {"start": v(-8.33, 10.39) * mm, "end": v(-8.26, 10.18) * mm});
            skLineSegment(sketch, "E346", {"start": v(-8.26, 10.18) * mm, "end": v(-8.2, 10) * mm});
            skLineSegment(sketch, "E347", {"start": v(-8.2, 10) * mm, "end": v(-8.14, 9.85) * mm});
            skLineSegment(sketch, "E348", {"start": v(-8.14, 9.85) * mm, "end": v(-8.08, 9.73) * mm});
            skLineSegment(sketch, "E349", {"start": v(-8.08, 9.73) * mm, "end": v(-8, 9.57) * mm});
            skLineSegment(sketch, "E350", {"start": v(-8, 9.57) * mm, "end": v(-7.98, 9.52) * mm});
            skLineSegment(sketch, "E351", {"start": v(-7.98, 9.52) * mm, "end": v(-7.99, 9.48) * mm});
            skLineSegment(sketch, "E352", {"start": v(-7.99, 9.48) * mm, "end": v(-8.36, 9.16) * mm});
            skLineSegment(sketch, "E353", {"start": v(-8.36, 9.16) * mm, "end": v(-8.4, 9.16) * mm});
            skLineSegment(sketch, "E354", {"start": v(-8.4, 9.16) * mm, "end": v(-8.44, 9.18) * mm});
            skLineSegment(sketch, "E355", {"start": v(-8.44, 9.18) * mm, "end": v(-8.59, 9.28) * mm});
            skLineSegment(sketch, "E356", {"start": v(-8.59, 9.28) * mm, "end": v(-8.7, 9.35) * mm});
            skLineSegment(sketch, "E357", {"start": v(-8.7, 9.35) * mm, "end": v(-8.85, 9.44) * mm});
            skLineSegment(sketch, "E358", {"start": v(-8.85, 9.44) * mm, "end": v(-9.02, 9.52) * mm});
            skLineSegment(sketch, "E359", {"start": v(-9.02, 9.52) * mm, "end": v(-9.2, 9.61) * mm});
            skLineSegment(sketch, "E360", {"start": v(-9.2, 9.61) * mm, "end": v(-9.42, 9.7) * mm});
            skLineSegment(sketch, "E361", {"start": v(-9.42, 9.7) * mm, "end": v(-9.57, 9.57) * mm});
            skLineSegment(sketch, "E362", {"start": v(-9.57, 9.57) * mm, "end": v(-9.7, 9.42) * mm});
            skLineSegment(sketch, "E363", {"start": v(-9.7, 9.42) * mm, "end": v(-9.61, 9.2) * mm});
            skLineSegment(sketch, "E364", {"start": v(-9.61, 9.2) * mm, "end": v(-9.52, 9.02) * mm});
            skLineSegment(sketch, "E365", {"start": v(-9.52, 9.02) * mm, "end": v(-9.44, 8.85) * mm});
            skLineSegment(sketch, "E366", {"start": v(-9.44, 8.85) * mm, "end": v(-9.35, 8.7) * mm});
            skLineSegment(sketch, "E367", {"start": v(-9.35, 8.7) * mm, "end": v(-9.28, 8.59) * mm});
            skLineSegment(sketch, "E368", {"start": v(-9.28, 8.59) * mm, "end": v(-9.18, 8.44) * mm});
            skLineSegment(sketch, "E369", {"start": v(-9.18, 8.44) * mm, "end": v(-9.16, 8.4) * mm});
            skLineSegment(sketch, "E370", {"start": v(-9.16, 8.4) * mm, "end": v(-9.16, 8.36) * mm});
            skLineSegment(sketch, "E371", {"start": v(-9.16, 8.36) * mm, "end": v(-9.48, 7.99) * mm});
            skLineSegment(sketch, "E372", {"start": v(-9.48, 7.99) * mm, "end": v(-9.52, 7.98) * mm});
            skLineSegment(sketch, "E373", {"start": v(-9.52, 7.98) * mm, "end": v(-9.57, 8) * mm});
            skLineSegment(sketch, "E374", {"start": v(-9.57, 8) * mm, "end": v(-9.73, 8.08) * mm});
            skLineSegment(sketch, "E375", {"start": v(-9.73, 8.08) * mm, "end": v(-9.85, 8.14) * mm});
            skLineSegment(sketch, "E376", {"start": v(-9.85, 8.14) * mm, "end": v(-10, 8.2) * mm});
            skLineSegment(sketch, "E377", {"start": v(-10, 8.2) * mm, "end": v(-10.18, 8.26) * mm});
            skLineSegment(sketch, "E378", {"start": v(-10.18, 8.26) * mm, "end": v(-10.39, 8.33) * mm});
            skLineSegment(sketch, "E379", {"start": v(-10.39, 8.33) * mm, "end": v(-10.6, 8.39) * mm});
            skLineSegment(sketch, "E380", {"start": v(-10.6, 8.39) * mm, "end": v(-10.73, 8.24) * mm});
            skLineSegment(sketch, "E381", {"start": v(-10.73, 8.24) * mm, "end": v(-10.84, 8.07) * mm});
            skLineSegment(sketch, "E382", {"start": v(-10.84, 8.07) * mm, "end": v(-10.73, 7.88) * mm});
            skLineSegment(sketch, "E383", {"start": v(-10.73, 7.88) * mm, "end": v(-10.62, 7.7) * mm});
            skLineSegment(sketch, "E384", {"start": v(-10.62, 7.7) * mm, "end": v(-10.51, 7.54) * mm});
            skLineSegment(sketch, "E385", {"start": v(-10.51, 7.54) * mm, "end": v(-10.41, 7.41) * mm});
            skLineSegment(sketch, "E386", {"start": v(-10.41, 7.41) * mm, "end": v(-10.32, 7.3) * mm});
            skLineSegment(sketch, "E387", {"start": v(-10.32, 7.3) * mm, "end": v(-10.2, 7.17) * mm});
            skLineSegment(sketch, "E388", {"start": v(-10.2, 7.17) * mm, "end": v(-10.17, 7.13) * mm});
            skLineSegment(sketch, "E389", {"start": v(-10.17, 7.13) * mm, "end": v(-10.17, 7.1) * mm});
            skLineSegment(sketch, "E390", {"start": v(-10.17, 7.1) * mm, "end": v(-10.45, 6.68) * mm});
            skLineSegment(sketch, "E391", {"start": v(-10.45, 6.68) * mm, "end": v(-10.48, 6.67) * mm});
            skLineSegment(sketch, "E392", {"start": v(-10.48, 6.67) * mm, "end": v(-10.53, 6.68) * mm});
            skLineSegment(sketch, "E393", {"start": v(-10.53, 6.68) * mm, "end": v(-10.7, 6.74) * mm});
            skLineSegment(sketch, "E394", {"start": v(-10.7, 6.74) * mm, "end": v(-10.83, 6.78) * mm});
            skLineSegment(sketch, "E395", {"start": v(-10.83, 6.78) * mm, "end": v(-11, 6.82) * mm});
            skLineSegment(sketch, "E396", {"start": v(-11, 6.82) * mm, "end": v(-11.18, 6.86) * mm});
            skLineSegment(sketch, "E397", {"start": v(-11.18, 6.86) * mm, "end": v(-11.38, 6.9) * mm});
            skLineSegment(sketch, "E398", {"start": v(-11.38, 6.9) * mm, "end": v(-11.6, 6.93) * mm});
            skLineSegment(sketch, "E399", {"start": v(-11.6, 6.93) * mm, "end": v(-11.72, 6.76) * mm});
            skLineSegment(sketch, "E400", {"start": v(-11.72, 6.76) * mm, "end": v(-11.8, 6.59) * mm});
            skLineSegment(sketch, "E401", {"start": v(-11.8, 6.59) * mm, "end": v(-11.67, 6.4) * mm});
            skLineSegment(sketch, "E402", {"start": v(-11.67, 6.4) * mm, "end": v(-11.53, 6.25) * mm});
            skLineSegment(sketch, "E403", {"start": v(-11.53, 6.25) * mm, "end": v(-11.4, 6.1) * mm});
            skLineSegment(sketch, "E404", {"start": v(-11.4, 6.1) * mm, "end": v(-11.29, 5.99) * mm});
            skLineSegment(sketch, "E405", {"start": v(-11.29, 5.99) * mm, "end": v(-11.19, 5.9) * mm});
            skLineSegment(sketch, "E406", {"start": v(-11.19, 5.9) * mm, "end": v(-11.05, 5.78) * mm});
            skLineSegment(sketch, "E407", {"start": v(-11.05, 5.78) * mm, "end": v(-11.02, 5.74) * mm});
            skLineSegment(sketch, "E408", {"start": v(-11.02, 5.74) * mm, "end": v(-11, 5.7) * mm});
            skLineSegment(sketch, "E409", {"start": v(-11, 5.7) * mm, "end": v(-11.23, 5.26) * mm});
            skLineSegment(sketch, "E410", {"start": v(-11.23, 5.26) * mm, "end": v(-11.26, 5.25) * mm});
            skLineSegment(sketch, "E411", {"start": v(-11.26, 5.25) * mm, "end": v(-11.31, 5.25) * mm});
            skLineSegment(sketch, "E412", {"start": v(-11.31, 5.25) * mm, "end": v(-11.49, 5.29) * mm});
            skLineSegment(sketch, "E413", {"start": v(-11.49, 5.29) * mm, "end": v(-11.62, 5.31) * mm});
            skLineSegment(sketch, "E414", {"start": v(-11.62, 5.31) * mm, "end": v(-11.79, 5.33) * mm});
            skLineSegment(sketch, "E415", {"start": v(-11.79, 5.33) * mm, "end": v(-11.98, 5.35) * mm});
            skLineSegment(sketch, "E416", {"start": v(-11.98, 5.35) * mm, "end": v(-12.19, 5.36) * mm});
            skLineSegment(sketch, "E417", {"start": v(-12.19, 5.36) * mm, "end": v(-12.41, 5.36) * mm});
            skLineSegment(sketch, "E418", {"start": v(-12.41, 5.36) * mm, "end": v(-12.5, 5.18) * mm});
            skLineSegment(sketch, "E419", {"start": v(-12.5, 5.18) * mm, "end": v(-12.56, 4.99) * mm});
            skLineSegment(sketch, "E420", {"start": v(-12.56, 4.99) * mm, "end": v(-12.4, 4.83) * mm});
            skLineSegment(sketch, "E421", {"start": v(-12.4, 4.83) * mm, "end": v(-12.25, 4.69) * mm});
            skLineSegment(sketch, "E422", {"start": v(-12.25, 4.69) * mm, "end": v(-12.1, 4.57) * mm});
            skLineSegment(sketch, "E423", {"start": v(-12.1, 4.57) * mm, "end": v(-11.97, 4.47) * mm});
            skLineSegment(sketch, "E424", {"start": v(-11.97, 4.47) * mm, "end": v(-11.86, 4.38) * mm});
            skLineSegment(sketch, "E425", {"start": v(-11.86, 4.38) * mm, "end": v(-11.71, 4.29) * mm});
            skLineSegment(sketch, "E426", {"start": v(-11.71, 4.29) * mm, "end": v(-11.67, 4.25) * mm});
            skLineSegment(sketch, "E427", {"start": v(-11.67, 4.25) * mm, "end": v(-11.66, 4.22) * mm});
            skLineSegment(sketch, "E428", {"start": v(-11.66, 4.22) * mm, "end": v(-11.82, 3.75) * mm});
            skLineSegment(sketch, "E429", {"start": v(-11.82, 3.75) * mm, "end": v(-11.85, 3.73) * mm});
            skLineSegment(sketch, "E430", {"start": v(-11.85, 3.73) * mm, "end": v(-11.9, 3.73) * mm});
            skLineSegment(sketch, "E431", {"start": v(-11.9, 3.73) * mm, "end": v(-12.08, 3.74) * mm});
            skLineSegment(sketch, "E432", {"start": v(-12.08, 3.74) * mm, "end": v(-12.22, 3.75) * mm});
            skLineSegment(sketch, "E433", {"start": v(-12.22, 3.75) * mm, "end": v(-12.38, 3.75) * mm});
            skLineSegment(sketch, "E434", {"start": v(-12.38, 3.75) * mm, "end": v(-12.57, 3.74) * mm});
            skLineSegment(sketch, "E435", {"start": v(-12.57, 3.74) * mm, "end": v(-12.78, 3.72) * mm});
            skLineSegment(sketch, "E436", {"start": v(-12.78, 3.72) * mm, "end": v(-13, 3.69) * mm});
            skLineSegment(sketch, "E437", {"start": v(-13, 3.69) * mm, "end": v(-13.07, 3.5) * mm});
            skLineSegment(sketch, "E438", {"start": v(-13.07, 3.5) * mm, "end": v(-13.1, 3.3) * mm});
            skLineSegment(sketch, "E439", {"start": v(-13.1, 3.3) * mm, "end": v(-12.93, 3.17) * mm});
            skLineSegment(sketch, "E440", {"start": v(-12.93, 3.17) * mm, "end": v(-12.76, 3.05) * mm});
            skLineSegment(sketch, "E441", {"start": v(-12.76, 3.05) * mm, "end": v(-12.6, 2.95) * mm});
            skLineSegment(sketch, "E442", {"start": v(-12.6, 2.95) * mm, "end": v(-12.46, 2.86) * mm});
            skLineSegment(sketch, "E443", {"start": v(-12.46, 2.86) * mm, "end": v(-12.33, 2.8) * mm});
            skLineSegment(sketch, "E444", {"start": v(-12.33, 2.8) * mm, "end": v(-12.17, 2.72) * mm});
            skLineSegment(sketch, "E445", {"start": v(-12.17, 2.72) * mm, "end": v(-12.13, 2.7) * mm});
            skLineSegment(sketch, "E446", {"start": v(-12.13, 2.7) * mm, "end": v(-12.1, 2.66) * mm});
            skLineSegment(sketch, "E447", {"start": v(-12.1, 2.66) * mm, "end": v(-12.2, 2.17) * mm});
            skLineSegment(sketch, "E448", {"start": v(-12.2, 2.17) * mm, "end": v(-12.23, 2.15) * mm});
            skLineSegment(sketch, "E449", {"start": v(-12.23, 2.15) * mm, "end": v(-12.29, 2.14) * mm});
            skLineSegment(sketch, "E450", {"start": v(-12.29, 2.14) * mm, "end": v(-12.46, 2.13) * mm});
            skLineSegment(sketch, "E451", {"start": v(-12.46, 2.13) * mm, "end": v(-12.6, 2.12) * mm});
            skLineSegment(sketch, "E452", {"start": v(-12.6, 2.12) * mm, "end": v(-12.77, 2.1) * mm});
            skLineSegment(sketch, "E453", {"start": v(-12.77, 2.1) * mm, "end": v(-12.95, 2.07) * mm});
            skLineSegment(sketch, "E454", {"start": v(-12.95, 2.07) * mm, "end": v(-13.16, 2.02) * mm});
            skLineSegment(sketch, "E455", {"start": v(-13.16, 2.02) * mm, "end": v(-13.37, 1.96) * mm});
            skLineSegment(sketch, "E456", {"start": v(-13.37, 1.96) * mm, "end": v(-13.41, 1.77) * mm});
            skLineSegment(sketch, "E457", {"start": v(-13.41, 1.77) * mm, "end": v(-13.43, 1.57) * mm});
            skLineSegment(sketch, "E458", {"start": v(-13.43, 1.57) * mm, "end": v(-13.23, 1.46) * mm});
            skLineSegment(sketch, "E459", {"start": v(-13.23, 1.46) * mm, "end": v(-13.04, 1.36) * mm});
            skLineSegment(sketch, "E460", {"start": v(-13.04, 1.36) * mm, "end": v(-12.87, 1.28) * mm});
            skLineSegment(sketch, "E461", {"start": v(-12.87, 1.28) * mm, "end": v(-12.72, 1.21) * mm});
            skLineSegment(sketch, "E462", {"start": v(-12.72, 1.21) * mm, "end": v(-12.59, 1.16) * mm});
            skLineSegment(sketch, "E463", {"start": v(-12.59, 1.16) * mm, "end": v(-12.42, 1.11) * mm});
            skLineSegment(sketch, "E464", {"start": v(-12.42, 1.11) * mm, "end": v(-12.38, 1.09) * mm});
            skLineSegment(sketch, "E465", {"start": v(-12.38, 1.09) * mm, "end": v(-12.35, 1.06) * mm});
            skLineSegment(sketch, "E466", {"start": v(-12.35, 1.06) * mm, "end": v(-12.39, 0.56) * mm});
            skLineSegment(sketch, "E467", {"start": v(-12.39, 0.56) * mm, "end": v(-12.41, 0.54) * mm});
            skLineSegment(sketch, "E468", {"start": v(-12.41, 0.54) * mm, "end": v(-12.46, 0.52) * mm});
            skLineSegment(sketch, "E469", {"start": v(-12.46, 0.52) * mm, "end": v(-12.63, 0.49) * mm});
            skLineSegment(sketch, "E470", {"start": v(-12.63, 0.49) * mm, "end": v(-12.77, 0.46) * mm});
            skLineSegment(sketch, "E471", {"start": v(-12.77, 0.46) * mm, "end": v(-12.93, 0.41) * mm});
            skLineSegment(sketch, "E472", {"start": v(-12.93, 0.41) * mm, "end": v(-13.11, 0.36) * mm});
            skLineSegment(sketch, "E473", {"start": v(-13.11, 0.36) * mm, "end": v(-13.3, 0.28) * mm});
            skLineSegment(sketch, "E474", {"start": v(-13.3, 0.28) * mm, "end": v(-13.52, 0.2) * mm});
            skLineSegment(sketch, "E475", {"start": v(-13.52, 0.2) * mm, "end": v(-13.53, 0) * mm});
            skLineSegment(sketch, "E476", {"start": v(-13.53, 0) * mm, "end": v(-13.52, -0.2) * mm});
            skLineSegment(sketch, "E477", {"start": v(-13.52, -0.2) * mm, "end": v(-13.3, -0.28) * mm});
            skLineSegment(sketch, "E478", {"start": v(-13.3, -0.28) * mm, "end": v(-13.11, -0.36) * mm});
            skLineSegment(sketch, "E479", {"start": v(-13.11, -0.36) * mm, "end": v(-12.93, -0.41) * mm});
            skLineSegment(sketch, "E480", {"start": v(-12.93, -0.41) * mm, "end": v(-12.77, -0.46) * mm});
            skLineSegment(sketch, "E481", {"start": v(-12.77, -0.46) * mm, "end": v(-12.63, -0.49) * mm});
            skLineSegment(sketch, "E482", {"start": v(-12.63, -0.49) * mm, "end": v(-12.46, -0.52) * mm});
            skLineSegment(sketch, "E483", {"start": v(-12.46, -0.52) * mm, "end": v(-12.41, -0.54) * mm});
            skLineSegment(sketch, "E484", {"start": v(-12.41, -0.54) * mm, "end": v(-12.39, -0.56) * mm});
            skLineSegment(sketch, "E485", {"start": v(-12.39, -0.56) * mm, "end": v(-12.35, -1.06) * mm});
            skLineSegment(sketch, "E486", {"start": v(-12.35, -1.06) * mm, "end": v(-12.38, -1.09) * mm});
            skLineSegment(sketch, "E487", {"start": v(-12.38, -1.09) * mm, "end": v(-12.42, -1.11) * mm});
            skLineSegment(sketch, "E488", {"start": v(-12.42, -1.11) * mm, "end": v(-12.59, -1.16) * mm});
            skLineSegment(sketch, "E489", {"start": v(-12.59, -1.16) * mm, "end": v(-12.72, -1.21) * mm});
            skLineSegment(sketch, "E490", {"start": v(-12.72, -1.21) * mm, "end": v(-12.87, -1.28) * mm});
            skLineSegment(sketch, "E491", {"start": v(-12.87, -1.28) * mm, "end": v(-13.04, -1.36) * mm});
            skLineSegment(sketch, "E492", {"start": v(-13.04, -1.36) * mm, "end": v(-13.23, -1.46) * mm});
            skLineSegment(sketch, "E493", {"start": v(-13.23, -1.46) * mm, "end": v(-13.43, -1.57) * mm});
            skLineSegment(sketch, "E494", {"start": v(-13.43, -1.57) * mm, "end": v(-13.41, -1.77) * mm});
            skLineSegment(sketch, "E495", {"start": v(-13.41, -1.77) * mm, "end": v(-13.37, -1.96) * mm});
            skLineSegment(sketch, "E496", {"start": v(-13.37, -1.96) * mm, "end": v(-13.16, -2.02) * mm});
            skLineSegment(sketch, "E497", {"start": v(-13.16, -2.02) * mm, "end": v(-12.95, -2.07) * mm});
            skLineSegment(sketch, "E498", {"start": v(-12.95, -2.07) * mm, "end": v(-12.77, -2.1) * mm});
            skLineSegment(sketch, "E499", {"start": v(-12.77, -2.1) * mm, "end": v(-12.6, -2.12) * mm});
            skLineSegment(sketch, "E500", {"start": v(-12.6, -2.12) * mm, "end": v(-12.46, -2.13) * mm});
            skLineSegment(sketch, "E501", {"start": v(-12.46, -2.13) * mm, "end": v(-12.29, -2.14) * mm});
            skLineSegment(sketch, "E502", {"start": v(-12.29, -2.14) * mm, "end": v(-12.23, -2.15) * mm});
            skLineSegment(sketch, "E503", {"start": v(-12.23, -2.15) * mm, "end": v(-12.2, -2.17) * mm});
            skLineSegment(sketch, "E504", {"start": v(-12.2, -2.17) * mm, "end": v(-12.1, -2.66) * mm});
            skLineSegment(sketch, "E505", {"start": v(-12.1, -2.66) * mm, "end": v(-12.13, -2.7) * mm});
            skLineSegment(sketch, "E506", {"start": v(-12.13, -2.7) * mm, "end": v(-12.17, -2.72) * mm});
            skLineSegment(sketch, "E507", {"start": v(-12.17, -2.72) * mm, "end": v(-12.33, -2.8) * mm});
            skLineSegment(sketch, "E508", {"start": v(-12.33, -2.8) * mm, "end": v(-12.46, -2.86) * mm});
            skLineSegment(sketch, "E509", {"start": v(-12.46, -2.86) * mm, "end": v(-12.6, -2.95) * mm});
            skLineSegment(sketch, "E510", {"start": v(-12.6, -2.95) * mm, "end": v(-12.76, -3.05) * mm});
            skLineSegment(sketch, "E511", {"start": v(-12.76, -3.05) * mm, "end": v(-12.93, -3.17) * mm});
            skLineSegment(sketch, "E512", {"start": v(-12.93, -3.17) * mm, "end": v(-13.1, -3.3) * mm});
            skLineSegment(sketch, "E513", {"start": v(-13.1, -3.3) * mm, "end": v(-13.07, -3.5) * mm});
            skLineSegment(sketch, "E514", {"start": v(-13.07, -3.5) * mm, "end": v(-13, -3.69) * mm});
            skLineSegment(sketch, "E515", {"start": v(-13, -3.69) * mm, "end": v(-12.78, -3.72) * mm});
            skLineSegment(sketch, "E516", {"start": v(-12.78, -3.72) * mm, "end": v(-12.57, -3.74) * mm});
            skLineSegment(sketch, "E517", {"start": v(-12.57, -3.74) * mm, "end": v(-12.38, -3.75) * mm});
            skLineSegment(sketch, "E518", {"start": v(-12.38, -3.75) * mm, "end": v(-12.22, -3.75) * mm});
            skLineSegment(sketch, "E519", {"start": v(-12.22, -3.75) * mm, "end": v(-12.08, -3.74) * mm});
            skLineSegment(sketch, "E520", {"start": v(-12.08, -3.74) * mm, "end": v(-11.9, -3.73) * mm});
            skLineSegment(sketch, "E521", {"start": v(-11.9, -3.73) * mm, "end": v(-11.85, -3.73) * mm});
            skLineSegment(sketch, "E522", {"start": v(-11.85, -3.73) * mm, "end": v(-11.82, -3.75) * mm});
            skLineSegment(sketch, "E523", {"start": v(-11.82, -3.75) * mm, "end": v(-11.66, -4.22) * mm});
            skLineSegment(sketch, "E524", {"start": v(-11.66, -4.22) * mm, "end": v(-11.67, -4.25) * mm});
            skLineSegment(sketch, "E525", {"start": v(-11.67, -4.25) * mm, "end": v(-11.71, -4.29) * mm});
            skLineSegment(sketch, "E526", {"start": v(-11.71, -4.29) * mm, "end": v(-11.86, -4.38) * mm});
            skLineSegment(sketch, "E527", {"start": v(-11.86, -4.38) * mm, "end": v(-11.97, -4.47) * mm});
            skLineSegment(sketch, "E528", {"start": v(-11.97, -4.47) * mm, "end": v(-12.1, -4.57) * mm});
            skLineSegment(sketch, "E529", {"start": v(-12.1, -4.57) * mm, "end": v(-12.25, -4.69) * mm});
            skLineSegment(sketch, "E530", {"start": v(-12.25, -4.69) * mm, "end": v(-12.4, -4.83) * mm});
            skLineSegment(sketch, "E531", {"start": v(-12.4, -4.83) * mm, "end": v(-12.56, -4.99) * mm});
            skLineSegment(sketch, "E532", {"start": v(-12.56, -4.99) * mm, "end": v(-12.5, -5.18) * mm});
            skLineSegment(sketch, "E533", {"start": v(-12.5, -5.18) * mm, "end": v(-12.41, -5.36) * mm});
            skLineSegment(sketch, "E534", {"start": v(-12.41, -5.36) * mm, "end": v(-12.19, -5.36) * mm});
            skLineSegment(sketch, "E535", {"start": v(-12.19, -5.36) * mm, "end": v(-11.98, -5.35) * mm});
            skLineSegment(sketch, "E536", {"start": v(-11.98, -5.35) * mm, "end": v(-11.79, -5.33) * mm});
            skLineSegment(sketch, "E537", {"start": v(-11.79, -5.33) * mm, "end": v(-11.62, -5.31) * mm});
            skLineSegment(sketch, "E538", {"start": v(-11.62, -5.31) * mm, "end": v(-11.49, -5.29) * mm});
            skLineSegment(sketch, "E539", {"start": v(-11.49, -5.29) * mm, "end": v(-11.31, -5.25) * mm});
            skLineSegment(sketch, "E540", {"start": v(-11.31, -5.25) * mm, "end": v(-11.26, -5.25) * mm});
            skLineSegment(sketch, "E541", {"start": v(-11.26, -5.25) * mm, "end": v(-11.23, -5.26) * mm});
            skLineSegment(sketch, "E542", {"start": v(-11.23, -5.26) * mm, "end": v(-11, -5.7) * mm});
            skLineSegment(sketch, "E543", {"start": v(-11, -5.7) * mm, "end": v(-11.02, -5.74) * mm});
            skLineSegment(sketch, "E544", {"start": v(-11.02, -5.74) * mm, "end": v(-11.05, -5.78) * mm});
            skLineSegment(sketch, "E545", {"start": v(-11.05, -5.78) * mm, "end": v(-11.19, -5.9) * mm});
            skLineSegment(sketch, "E546", {"start": v(-11.19, -5.9) * mm, "end": v(-11.29, -5.99) * mm});
            skLineSegment(sketch, "E547", {"start": v(-11.29, -5.99) * mm, "end": v(-11.4, -6.1) * mm});
            skLineSegment(sketch, "E548", {"start": v(-11.4, -6.1) * mm, "end": v(-11.53, -6.25) * mm});
            skLineSegment(sketch, "E549", {"start": v(-11.53, -6.25) * mm, "end": v(-11.67, -6.4) * mm});
            skLineSegment(sketch, "E550", {"start": v(-11.67, -6.4) * mm, "end": v(-11.8, -6.59) * mm});
            skLineSegment(sketch, "E551", {"start": v(-11.8, -6.59) * mm, "end": v(-11.72, -6.76) * mm});
            skLineSegment(sketch, "E552", {"start": v(-11.72, -6.76) * mm, "end": v(-11.6, -6.93) * mm});
            skLineSegment(sketch, "E553", {"start": v(-11.6, -6.93) * mm, "end": v(-11.38, -6.9) * mm});
            skLineSegment(sketch, "E554", {"start": v(-11.38, -6.9) * mm, "end": v(-11.18, -6.86) * mm});
            skLineSegment(sketch, "E555", {"start": v(-11.18, -6.86) * mm, "end": v(-11, -6.82) * mm});
            skLineSegment(sketch, "E556", {"start": v(-11, -6.82) * mm, "end": v(-10.83, -6.78) * mm});
            skLineSegment(sketch, "E557", {"start": v(-10.83, -6.78) * mm, "end": v(-10.7, -6.74) * mm});
            skLineSegment(sketch, "E558", {"start": v(-10.7, -6.74) * mm, "end": v(-10.53, -6.68) * mm});
            skLineSegment(sketch, "E559", {"start": v(-10.53, -6.68) * mm, "end": v(-10.48, -6.67) * mm});
            skLineSegment(sketch, "E560", {"start": v(-10.48, -6.67) * mm, "end": v(-10.45, -6.68) * mm});
            skLineSegment(sketch, "E561", {"start": v(-10.45, -6.68) * mm, "end": v(-10.17, -7.1) * mm});
            skLineSegment(sketch, "E562", {"start": v(-10.17, -7.1) * mm, "end": v(-10.17, -7.13) * mm});
            skLineSegment(sketch, "E563", {"start": v(-10.17, -7.13) * mm, "end": v(-10.2, -7.17) * mm});
            skLineSegment(sketch, "E564", {"start": v(-10.2, -7.17) * mm, "end": v(-10.32, -7.3) * mm});
            skLineSegment(sketch, "E565", {"start": v(-10.32, -7.3) * mm, "end": v(-10.41, -7.41) * mm});
            skLineSegment(sketch, "E566", {"start": v(-10.41, -7.41) * mm, "end": v(-10.51, -7.54) * mm});
            skLineSegment(sketch, "E567", {"start": v(-10.51, -7.54) * mm, "end": v(-10.62, -7.7) * mm});
            skLineSegment(sketch, "E568", {"start": v(-10.62, -7.7) * mm, "end": v(-10.73, -7.88) * mm});
            skLineSegment(sketch, "E569", {"start": v(-10.73, -7.88) * mm, "end": v(-10.84, -8.07) * mm});
            skLineSegment(sketch, "E570", {"start": v(-10.84, -8.07) * mm, "end": v(-10.73, -8.24) * mm});
            skLineSegment(sketch, "E571", {"start": v(-10.73, -8.24) * mm, "end": v(-10.6, -8.39) * mm});
            skLineSegment(sketch, "E572", {"start": v(-10.6, -8.39) * mm, "end": v(-10.39, -8.33) * mm});
            skLineSegment(sketch, "E573", {"start": v(-10.39, -8.33) * mm, "end": v(-10.18, -8.26) * mm});
            skLineSegment(sketch, "E574", {"start": v(-10.18, -8.26) * mm, "end": v(-10, -8.2) * mm});
            skLineSegment(sketch, "E575", {"start": v(-10, -8.2) * mm, "end": v(-9.85, -8.14) * mm});
            skLineSegment(sketch, "E576", {"start": v(-9.85, -8.14) * mm, "end": v(-9.73, -8.08) * mm});
            skLineSegment(sketch, "E577", {"start": v(-9.73, -8.08) * mm, "end": v(-9.57, -8) * mm});
            skLineSegment(sketch, "E578", {"start": v(-9.57, -8) * mm, "end": v(-9.52, -7.98) * mm});
            skLineSegment(sketch, "E579", {"start": v(-9.52, -7.98) * mm, "end": v(-9.48, -7.99) * mm});
            skLineSegment(sketch, "E580", {"start": v(-9.48, -7.99) * mm, "end": v(-9.16, -8.36) * mm});
            skLineSegment(sketch, "E581", {"start": v(-9.16, -8.36) * mm, "end": v(-9.16, -8.4) * mm});
            skLineSegment(sketch, "E582", {"start": v(-9.16, -8.4) * mm, "end": v(-9.18, -8.44) * mm});
            skLineSegment(sketch, "E583", {"start": v(-9.18, -8.44) * mm, "end": v(-9.28, -8.59) * mm});
            skLineSegment(sketch, "E584", {"start": v(-9.28, -8.59) * mm, "end": v(-9.35, -8.7) * mm});
            skLineSegment(sketch, "E585", {"start": v(-9.35, -8.7) * mm, "end": v(-9.44, -8.85) * mm});
            skLineSegment(sketch, "E586", {"start": v(-9.44, -8.85) * mm, "end": v(-9.52, -9.02) * mm});
            skLineSegment(sketch, "E587", {"start": v(-9.52, -9.02) * mm, "end": v(-9.61, -9.2) * mm});
            skLineSegment(sketch, "E588", {"start": v(-9.61, -9.2) * mm, "end": v(-9.7, -9.42) * mm});
            skLineSegment(sketch, "E589", {"start": v(-9.7, -9.42) * mm, "end": v(-9.57, -9.57) * mm});
            skLineSegment(sketch, "E590", {"start": v(-9.57, -9.57) * mm, "end": v(-9.42, -9.7) * mm});
            skLineSegment(sketch, "E591", {"start": v(-9.42, -9.7) * mm, "end": v(-9.2, -9.61) * mm});
            skLineSegment(sketch, "E592", {"start": v(-9.2, -9.61) * mm, "end": v(-9.02, -9.52) * mm});
            skLineSegment(sketch, "E593", {"start": v(-9.02, -9.52) * mm, "end": v(-8.85, -9.44) * mm});
            skLineSegment(sketch, "E594", {"start": v(-8.85, -9.44) * mm, "end": v(-8.7, -9.35) * mm});
            skLineSegment(sketch, "E595", {"start": v(-8.7, -9.35) * mm, "end": v(-8.59, -9.28) * mm});
            skLineSegment(sketch, "E596", {"start": v(-8.59, -9.28) * mm, "end": v(-8.44, -9.18) * mm});
            skLineSegment(sketch, "E597", {"start": v(-8.44, -9.18) * mm, "end": v(-8.4, -9.16) * mm});
            skLineSegment(sketch, "E598", {"start": v(-8.4, -9.16) * mm, "end": v(-8.36, -9.16) * mm});
            skLineSegment(sketch, "E599", {"start": v(-8.36, -9.16) * mm, "end": v(-7.99, -9.48) * mm});
            skLineSegment(sketch, "E600", {"start": v(-7.99, -9.48) * mm, "end": v(-7.98, -9.52) * mm});
            skLineSegment(sketch, "E601", {"start": v(-7.98, -9.52) * mm, "end": v(-8, -9.57) * mm});
            skLineSegment(sketch, "E602", {"start": v(-8, -9.57) * mm, "end": v(-8.08, -9.73) * mm});
            skLineSegment(sketch, "E603", {"start": v(-8.08, -9.73) * mm, "end": v(-8.14, -9.85) * mm});
            skLineSegment(sketch, "E604", {"start": v(-8.14, -9.85) * mm, "end": v(-8.2, -10) * mm});
            skLineSegment(sketch, "E605", {"start": v(-8.2, -10) * mm, "end": v(-8.26, -10.18) * mm});
            skLineSegment(sketch, "E606", {"start": v(-8.26, -10.18) * mm, "end": v(-8.33, -10.39) * mm});
            skLineSegment(sketch, "E607", {"start": v(-8.33, -10.39) * mm, "end": v(-8.39, -10.6) * mm});
            skLineSegment(sketch, "E608", {"start": v(-8.39, -10.6) * mm, "end": v(-8.24, -10.73) * mm});
            skLineSegment(sketch, "E609", {"start": v(-8.24, -10.73) * mm, "end": v(-8.07, -10.84) * mm});
            skLineSegment(sketch, "E610", {"start": v(-8.07, -10.84) * mm, "end": v(-7.88, -10.73) * mm});
            skLineSegment(sketch, "E611", {"start": v(-7.88, -10.73) * mm, "end": v(-7.7, -10.62) * mm});
            skLineSegment(sketch, "E612", {"start": v(-7.7, -10.62) * mm, "end": v(-7.54, -10.51) * mm});
            skLineSegment(sketch, "E613", {"start": v(-7.54, -10.51) * mm, "end": v(-7.41, -10.41) * mm});
            skLineSegment(sketch, "E614", {"start": v(-7.41, -10.41) * mm, "end": v(-7.3, -10.32) * mm});
            skLineSegment(sketch, "E615", {"start": v(-7.3, -10.32) * mm, "end": v(-7.17, -10.2) * mm});
            skLineSegment(sketch, "E616", {"start": v(-7.17, -10.2) * mm, "end": v(-7.13, -10.17) * mm});
            skLineSegment(sketch, "E617", {"start": v(-7.13, -10.17) * mm, "end": v(-7.1, -10.17) * mm});
            skLineSegment(sketch, "E618", {"start": v(-7.1, -10.17) * mm, "end": v(-6.68, -10.45) * mm});
            skLineSegment(sketch, "E619", {"start": v(-6.68, -10.45) * mm, "end": v(-6.67, -10.48) * mm});
            skLineSegment(sketch, "E620", {"start": v(-6.67, -10.48) * mm, "end": v(-6.68, -10.53) * mm});
            skLineSegment(sketch, "E621", {"start": v(-6.68, -10.53) * mm, "end": v(-6.74, -10.7) * mm});
            skLineSegment(sketch, "E622", {"start": v(-6.74, -10.7) * mm, "end": v(-6.78, -10.83) * mm});
            skLineSegment(sketch, "E623", {"start": v(-6.78, -10.83) * mm, "end": v(-6.82, -11) * mm});
            skLineSegment(sketch, "E624", {"start": v(-6.82, -11) * mm, "end": v(-6.86, -11.18) * mm});
            skLineSegment(sketch, "E625", {"start": v(-6.86, -11.18) * mm, "end": v(-6.9, -11.38) * mm});
            skLineSegment(sketch, "E626", {"start": v(-6.9, -11.38) * mm, "end": v(-6.93, -11.6) * mm});
            skLineSegment(sketch, "E627", {"start": v(-6.93, -11.6) * mm, "end": v(-6.76, -11.72) * mm});
            skLineSegment(sketch, "E628", {"start": v(-6.76, -11.72) * mm, "end": v(-6.59, -11.8) * mm});
            skLineSegment(sketch, "E629", {"start": v(-6.59, -11.8) * mm, "end": v(-6.4, -11.67) * mm});
            skLineSegment(sketch, "E630", {"start": v(-6.4, -11.67) * mm, "end": v(-6.25, -11.53) * mm});
            skLineSegment(sketch, "E631", {"start": v(-6.25, -11.53) * mm, "end": v(-6.1, -11.4) * mm});
            skLineSegment(sketch, "E632", {"start": v(-6.1, -11.4) * mm, "end": v(-5.99, -11.29) * mm});
            skLineSegment(sketch, "E633", {"start": v(-5.99, -11.29) * mm, "end": v(-5.9, -11.19) * mm});
            skLineSegment(sketch, "E634", {"start": v(-5.9, -11.19) * mm, "end": v(-5.78, -11.05) * mm});
            skLineSegment(sketch, "E635", {"start": v(-5.78, -11.05) * mm, "end": v(-5.74, -11.02) * mm});
            skLineSegment(sketch, "E636", {"start": v(-5.74, -11.02) * mm, "end": v(-5.7, -11) * mm});
            skLineSegment(sketch, "E637", {"start": v(-5.7, -11) * mm, "end": v(-5.26, -11.23) * mm});
            skLineSegment(sketch, "E638", {"start": v(-5.26, -11.23) * mm, "end": v(-5.25, -11.26) * mm});
            skLineSegment(sketch, "E639", {"start": v(-5.25, -11.26) * mm, "end": v(-5.25, -11.31) * mm});
            skLineSegment(sketch, "E640", {"start": v(-5.25, -11.31) * mm, "end": v(-5.29, -11.49) * mm});
            skLineSegment(sketch, "E641", {"start": v(-5.29, -11.49) * mm, "end": v(-5.31, -11.62) * mm});
            skLineSegment(sketch, "E642", {"start": v(-5.31, -11.62) * mm, "end": v(-5.33, -11.79) * mm});
            skLineSegment(sketch, "E643", {"start": v(-5.33, -11.79) * mm, "end": v(-5.35, -11.98) * mm});
            skLineSegment(sketch, "E644", {"start": v(-5.35, -11.98) * mm, "end": v(-5.36, -12.19) * mm});
            skLineSegment(sketch, "E645", {"start": v(-5.36, -12.19) * mm, "end": v(-5.36, -12.41) * mm});
            skLineSegment(sketch, "E646", {"start": v(-5.36, -12.41) * mm, "end": v(-5.18, -12.5) * mm});
            skLineSegment(sketch, "E647", {"start": v(-5.18, -12.5) * mm, "end": v(-4.99, -12.56) * mm});
            skLineSegment(sketch, "E648", {"start": v(-4.99, -12.56) * mm, "end": v(-4.83, -12.4) * mm});
            skLineSegment(sketch, "E649", {"start": v(-4.83, -12.4) * mm, "end": v(-4.69, -12.25) * mm});
            skLineSegment(sketch, "E650", {"start": v(-4.69, -12.25) * mm, "end": v(-4.57, -12.1) * mm});
            skLineSegment(sketch, "E651", {"start": v(-4.57, -12.1) * mm, "end": v(-4.47, -11.97) * mm});
            skLineSegment(sketch, "E652", {"start": v(-4.47, -11.97) * mm, "end": v(-4.38, -11.86) * mm});
            skLineSegment(sketch, "E653", {"start": v(-4.38, -11.86) * mm, "end": v(-4.29, -11.71) * mm});
            skLineSegment(sketch, "E654", {"start": v(-4.29, -11.71) * mm, "end": v(-4.25, -11.67) * mm});
            skLineSegment(sketch, "E655", {"start": v(-4.25, -11.67) * mm, "end": v(-4.22, -11.66) * mm});
            skLineSegment(sketch, "E656", {"start": v(-4.22, -11.66) * mm, "end": v(-3.75, -11.82) * mm});
            skLineSegment(sketch, "E657", {"start": v(-3.75, -11.82) * mm, "end": v(-3.73, -11.85) * mm});
            skLineSegment(sketch, "E658", {"start": v(-3.73, -11.85) * mm, "end": v(-3.73, -11.9) * mm});
            skLineSegment(sketch, "E659", {"start": v(-3.73, -11.9) * mm, "end": v(-3.74, -12.08) * mm});
            skLineSegment(sketch, "E660", {"start": v(-3.74, -12.08) * mm, "end": v(-3.75, -12.22) * mm});
            skLineSegment(sketch, "E661", {"start": v(-3.75, -12.22) * mm, "end": v(-3.75, -12.38) * mm});
            skLineSegment(sketch, "E662", {"start": v(-3.75, -12.38) * mm, "end": v(-3.74, -12.57) * mm});
            skLineSegment(sketch, "E663", {"start": v(-3.74, -12.57) * mm, "end": v(-3.72, -12.78) * mm});
            skLineSegment(sketch, "E664", {"start": v(-3.72, -12.78) * mm, "end": v(-3.69, -13) * mm});
            skLineSegment(sketch, "E665", {"start": v(-3.69, -13) * mm, "end": v(-3.5, -13.07) * mm});
            skLineSegment(sketch, "E666", {"start": v(-3.5, -13.07) * mm, "end": v(-3.3, -13.1) * mm});
            skLineSegment(sketch, "E667", {"start": v(-3.3, -13.1) * mm, "end": v(-3.17, -12.93) * mm});
            skLineSegment(sketch, "E668", {"start": v(-3.17, -12.93) * mm, "end": v(-3.05, -12.76) * mm});
            skLineSegment(sketch, "E669", {"start": v(-3.05, -12.76) * mm, "end": v(-2.95, -12.6) * mm});
            skLineSegment(sketch, "E670", {"start": v(-2.95, -12.6) * mm, "end": v(-2.86, -12.46) * mm});
            skLineSegment(sketch, "E671", {"start": v(-2.86, -12.46) * mm, "end": v(-2.8, -12.33) * mm});
            skLineSegment(sketch, "E672", {"start": v(-2.8, -12.33) * mm, "end": v(-2.72, -12.17) * mm});
            skLineSegment(sketch, "E673", {"start": v(-2.72, -12.17) * mm, "end": v(-2.7, -12.13) * mm});
            skLineSegment(sketch, "E674", {"start": v(-2.7, -12.13) * mm, "end": v(-2.66, -12.1) * mm});
            skLineSegment(sketch, "E675", {"start": v(-2.66, -12.1) * mm, "end": v(-2.17, -12.2) * mm});
            skLineSegment(sketch, "E676", {"start": v(-2.17, -12.2) * mm, "end": v(-2.15, -12.23) * mm});
            skLineSegment(sketch, "E677", {"start": v(-2.15, -12.23) * mm, "end": v(-2.14, -12.29) * mm});
            skLineSegment(sketch, "E678", {"start": v(-2.14, -12.29) * mm, "end": v(-2.13, -12.46) * mm});
            skLineSegment(sketch, "E679", {"start": v(-2.13, -12.46) * mm, "end": v(-2.12, -12.6) * mm});
            skLineSegment(sketch, "E680", {"start": v(-2.12, -12.6) * mm, "end": v(-2.1, -12.77) * mm});
            skLineSegment(sketch, "E681", {"start": v(-2.1, -12.77) * mm, "end": v(-2.07, -12.95) * mm});
            skLineSegment(sketch, "E682", {"start": v(-2.07, -12.95) * mm, "end": v(-2.02, -13.16) * mm});
            skLineSegment(sketch, "E683", {"start": v(-2.02, -13.16) * mm, "end": v(-1.96, -13.37) * mm});
            skLineSegment(sketch, "E684", {"start": v(-1.96, -13.37) * mm, "end": v(-1.77, -13.41) * mm});
            skLineSegment(sketch, "E685", {"start": v(-1.77, -13.41) * mm, "end": v(-1.57, -13.43) * mm});
            skLineSegment(sketch, "E686", {"start": v(-1.57, -13.43) * mm, "end": v(-1.46, -13.23) * mm});
            skLineSegment(sketch, "E687", {"start": v(-1.46, -13.23) * mm, "end": v(-1.36, -13.04) * mm});
            skLineSegment(sketch, "E688", {"start": v(-1.36, -13.04) * mm, "end": v(-1.28, -12.87) * mm});
            skLineSegment(sketch, "E689", {"start": v(-1.28, -12.87) * mm, "end": v(-1.21, -12.72) * mm});
            skLineSegment(sketch, "E690", {"start": v(-1.21, -12.72) * mm, "end": v(-1.16, -12.59) * mm});
            skLineSegment(sketch, "E691", {"start": v(-1.16, -12.59) * mm, "end": v(-1.11, -12.42) * mm});
            skLineSegment(sketch, "E692", {"start": v(-1.11, -12.42) * mm, "end": v(-1.09, -12.38) * mm});
            skLineSegment(sketch, "E693", {"start": v(-1.09, -12.38) * mm, "end": v(-1.06, -12.35) * mm});
            skLineSegment(sketch, "E694", {"start": v(-1.06, -12.35) * mm, "end": v(-0.56, -12.39) * mm});
            skLineSegment(sketch, "E695", {"start": v(-0.56, -12.39) * mm, "end": v(-0.54, -12.41) * mm});
            skLineSegment(sketch, "E696", {"start": v(-0.54, -12.41) * mm, "end": v(-0.52, -12.46) * mm});
            skLineSegment(sketch, "E697", {"start": v(-0.52, -12.46) * mm, "end": v(-0.49, -12.63) * mm});
            skLineSegment(sketch, "E698", {"start": v(-0.49, -12.63) * mm, "end": v(-0.46, -12.77) * mm});
            skLineSegment(sketch, "E699", {"start": v(-0.46, -12.77) * mm, "end": v(-0.41, -12.93) * mm});
            skLineSegment(sketch, "E700", {"start": v(-0.41, -12.93) * mm, "end": v(-0.36, -13.11) * mm});
            skLineSegment(sketch, "E701", {"start": v(-0.36, -13.11) * mm, "end": v(-0.28, -13.3) * mm});
            skLineSegment(sketch, "E702", {"start": v(-0.28, -13.3) * mm, "end": v(-0.2, -13.52) * mm});
            skLineSegment(sketch, "E703", {"start": v(-0.2, -13.52) * mm, "end": v(0, -13.53) * mm});
            skLineSegment(sketch, "E704", {"start": v(0, -13.53) * mm, "end": v(0.2, -13.52) * mm});
            skLineSegment(sketch, "E705", {"start": v(0.2, -13.52) * mm, "end": v(0.28, -13.3) * mm});
            skLineSegment(sketch, "E706", {"start": v(0.28, -13.3) * mm, "end": v(0.36, -13.11) * mm});
            skLineSegment(sketch, "E707", {"start": v(0.36, -13.11) * mm, "end": v(0.41, -12.93) * mm});
            skLineSegment(sketch, "E708", {"start": v(0.41, -12.93) * mm, "end": v(0.46, -12.77) * mm});
            skLineSegment(sketch, "E709", {"start": v(0.46, -12.77) * mm, "end": v(0.49, -12.63) * mm});
            skLineSegment(sketch, "E710", {"start": v(0.49, -12.63) * mm, "end": v(0.52, -12.46) * mm});
            skLineSegment(sketch, "E711", {"start": v(0.52, -12.46) * mm, "end": v(0.54, -12.41) * mm});
            skLineSegment(sketch, "E712", {"start": v(0.54, -12.41) * mm, "end": v(0.56, -12.39) * mm});
            skLineSegment(sketch, "E713", {"start": v(0.56, -12.39) * mm, "end": v(1.06, -12.35) * mm});
            skLineSegment(sketch, "E714", {"start": v(1.06, -12.35) * mm, "end": v(1.09, -12.38) * mm});
            skLineSegment(sketch, "E715", {"start": v(1.09, -12.38) * mm, "end": v(1.11, -12.42) * mm});
            skLineSegment(sketch, "E716", {"start": v(1.11, -12.42) * mm, "end": v(1.16, -12.59) * mm});
            skLineSegment(sketch, "E717", {"start": v(1.16, -12.59) * mm, "end": v(1.21, -12.72) * mm});
            skLineSegment(sketch, "E718", {"start": v(1.21, -12.72) * mm, "end": v(1.28, -12.87) * mm});
            skLineSegment(sketch, "E719", {"start": v(1.28, -12.87) * mm, "end": v(1.36, -13.04) * mm});
            skLineSegment(sketch, "E720", {"start": v(1.36, -13.04) * mm, "end": v(1.46, -13.23) * mm});
            skLineSegment(sketch, "E721", {"start": v(1.46, -13.23) * mm, "end": v(1.57, -13.43) * mm});
            skLineSegment(sketch, "E722", {"start": v(1.57, -13.43) * mm, "end": v(1.77, -13.41) * mm});
            skLineSegment(sketch, "E723", {"start": v(1.77, -13.41) * mm, "end": v(1.96, -13.37) * mm});
            skLineSegment(sketch, "E724", {"start": v(1.96, -13.37) * mm, "end": v(2.02, -13.16) * mm});
            skLineSegment(sketch, "E725", {"start": v(2.02, -13.16) * mm, "end": v(2.07, -12.95) * mm});
            skLineSegment(sketch, "E726", {"start": v(2.07, -12.95) * mm, "end": v(2.1, -12.77) * mm});
            skLineSegment(sketch, "E727", {"start": v(2.1, -12.77) * mm, "end": v(2.12, -12.6) * mm});
            skLineSegment(sketch, "E728", {"start": v(2.12, -12.6) * mm, "end": v(2.13, -12.46) * mm});
            skLineSegment(sketch, "E729", {"start": v(2.13, -12.46) * mm, "end": v(2.14, -12.29) * mm});
            skLineSegment(sketch, "E730", {"start": v(2.14, -12.29) * mm, "end": v(2.15, -12.23) * mm});
            skLineSegment(sketch, "E731", {"start": v(2.15, -12.23) * mm, "end": v(2.17, -12.2) * mm});
            skLineSegment(sketch, "E732", {"start": v(2.17, -12.2) * mm, "end": v(2.66, -12.1) * mm});
            skLineSegment(sketch, "E733", {"start": v(2.66, -12.1) * mm, "end": v(2.7, -12.13) * mm});
            skLineSegment(sketch, "E734", {"start": v(2.7, -12.13) * mm, "end": v(2.72, -12.17) * mm});
            skLineSegment(sketch, "E735", {"start": v(2.72, -12.17) * mm, "end": v(2.8, -12.33) * mm});
            skLineSegment(sketch, "E736", {"start": v(2.8, -12.33) * mm, "end": v(2.86, -12.46) * mm});
            skLineSegment(sketch, "E737", {"start": v(2.86, -12.46) * mm, "end": v(2.95, -12.6) * mm});
            skLineSegment(sketch, "E738", {"start": v(2.95, -12.6) * mm, "end": v(3.05, -12.76) * mm});
            skLineSegment(sketch, "E739", {"start": v(3.05, -12.76) * mm, "end": v(3.17, -12.93) * mm});
            skLineSegment(sketch, "E740", {"start": v(3.17, -12.93) * mm, "end": v(3.3, -13.1) * mm});
            skLineSegment(sketch, "E741", {"start": v(3.3, -13.1) * mm, "end": v(3.5, -13.07) * mm});
            skLineSegment(sketch, "E742", {"start": v(3.5, -13.07) * mm, "end": v(3.69, -13) * mm});
            skLineSegment(sketch, "E743", {"start": v(3.69, -13) * mm, "end": v(3.72, -12.78) * mm});
            skLineSegment(sketch, "E744", {"start": v(3.72, -12.78) * mm, "end": v(3.74, -12.57) * mm});
            skLineSegment(sketch, "E745", {"start": v(3.74, -12.57) * mm, "end": v(3.75, -12.38) * mm});
            skLineSegment(sketch, "E746", {"start": v(3.75, -12.38) * mm, "end": v(3.75, -12.22) * mm});
            skLineSegment(sketch, "E747", {"start": v(3.75, -12.22) * mm, "end": v(3.74, -12.08) * mm});
            skLineSegment(sketch, "E748", {"start": v(3.74, -12.08) * mm, "end": v(3.73, -11.9) * mm});
            skLineSegment(sketch, "E749", {"start": v(3.73, -11.9) * mm, "end": v(3.73, -11.85) * mm});
            skLineSegment(sketch, "E750", {"start": v(3.73, -11.85) * mm, "end": v(3.75, -11.82) * mm});
            skLineSegment(sketch, "E751", {"start": v(3.75, -11.82) * mm, "end": v(4.22, -11.66) * mm});
            skLineSegment(sketch, "E752", {"start": v(4.22, -11.66) * mm, "end": v(4.25, -11.67) * mm});
            skLineSegment(sketch, "E753", {"start": v(4.25, -11.67) * mm, "end": v(4.29, -11.71) * mm});
            skLineSegment(sketch, "E754", {"start": v(4.29, -11.71) * mm, "end": v(4.38, -11.86) * mm});
            skLineSegment(sketch, "E755", {"start": v(4.38, -11.86) * mm, "end": v(4.47, -11.97) * mm});
            skLineSegment(sketch, "E756", {"start": v(4.47, -11.97) * mm, "end": v(4.57, -12.1) * mm});
            skLineSegment(sketch, "E757", {"start": v(4.57, -12.1) * mm, "end": v(4.69, -12.25) * mm});
            skLineSegment(sketch, "E758", {"start": v(4.69, -12.25) * mm, "end": v(4.83, -12.4) * mm});
            skLineSegment(sketch, "E759", {"start": v(4.83, -12.4) * mm, "end": v(4.99, -12.56) * mm});
            skLineSegment(sketch, "E760", {"start": v(4.99, -12.56) * mm, "end": v(5.18, -12.5) * mm});
            skLineSegment(sketch, "E761", {"start": v(5.18, -12.5) * mm, "end": v(5.36, -12.41) * mm});
            skLineSegment(sketch, "E762", {"start": v(5.36, -12.41) * mm, "end": v(5.36, -12.19) * mm});
            skLineSegment(sketch, "E763", {"start": v(5.36, -12.19) * mm, "end": v(5.35, -11.98) * mm});
            skLineSegment(sketch, "E764", {"start": v(5.35, -11.98) * mm, "end": v(5.33, -11.79) * mm});
            skLineSegment(sketch, "E765", {"start": v(5.33, -11.79) * mm, "end": v(5.31, -11.62) * mm});
            skLineSegment(sketch, "E766", {"start": v(5.31, -11.62) * mm, "end": v(5.29, -11.49) * mm});
            skLineSegment(sketch, "E767", {"start": v(5.29, -11.49) * mm, "end": v(5.25, -11.31) * mm});
            skLineSegment(sketch, "E768", {"start": v(5.25, -11.31) * mm, "end": v(5.25, -11.26) * mm});
            skLineSegment(sketch, "E769", {"start": v(5.25, -11.26) * mm, "end": v(5.26, -11.23) * mm});
            skLineSegment(sketch, "E770", {"start": v(5.26, -11.23) * mm, "end": v(5.7, -11) * mm});
            skLineSegment(sketch, "E771", {"start": v(5.7, -11) * mm, "end": v(5.74, -11.02) * mm});
            skLineSegment(sketch, "E772", {"start": v(5.74, -11.02) * mm, "end": v(5.78, -11.05) * mm});
            skLineSegment(sketch, "E773", {"start": v(5.78, -11.05) * mm, "end": v(5.9, -11.19) * mm});
            skLineSegment(sketch, "E774", {"start": v(5.9, -11.19) * mm, "end": v(5.99, -11.29) * mm});
            skLineSegment(sketch, "E775", {"start": v(5.99, -11.29) * mm, "end": v(6.1, -11.4) * mm});
            skLineSegment(sketch, "E776", {"start": v(6.1, -11.4) * mm, "end": v(6.25, -11.53) * mm});
            skLineSegment(sketch, "E777", {"start": v(6.25, -11.53) * mm, "end": v(6.4, -11.67) * mm});
            skLineSegment(sketch, "E778", {"start": v(6.4, -11.67) * mm, "end": v(6.59, -11.8) * mm});
            skLineSegment(sketch, "E779", {"start": v(6.59, -11.8) * mm, "end": v(6.76, -11.72) * mm});
            skLineSegment(sketch, "E780", {"start": v(6.76, -11.72) * mm, "end": v(6.93, -11.6) * mm});
            skLineSegment(sketch, "E781", {"start": v(6.93, -11.6) * mm, "end": v(6.9, -11.38) * mm});
            skLineSegment(sketch, "E782", {"start": v(6.9, -11.38) * mm, "end": v(6.86, -11.18) * mm});
            skLineSegment(sketch, "E783", {"start": v(6.86, -11.18) * mm, "end": v(6.82, -11) * mm});
            skLineSegment(sketch, "E784", {"start": v(6.82, -11) * mm, "end": v(6.78, -10.83) * mm});
            skLineSegment(sketch, "E785", {"start": v(6.78, -10.83) * mm, "end": v(6.74, -10.7) * mm});
            skLineSegment(sketch, "E786", {"start": v(6.74, -10.7) * mm, "end": v(6.68, -10.53) * mm});
            skLineSegment(sketch, "E787", {"start": v(6.68, -10.53) * mm, "end": v(6.67, -10.48) * mm});
            skLineSegment(sketch, "E788", {"start": v(6.67, -10.48) * mm, "end": v(6.68, -10.45) * mm});
            skLineSegment(sketch, "E789", {"start": v(6.68, -10.45) * mm, "end": v(7.1, -10.17) * mm});
            skLineSegment(sketch, "E790", {"start": v(7.1, -10.17) * mm, "end": v(7.13, -10.17) * mm});
            skLineSegment(sketch, "E791", {"start": v(7.13, -10.17) * mm, "end": v(7.17, -10.2) * mm});
            skLineSegment(sketch, "E792", {"start": v(7.17, -10.2) * mm, "end": v(7.3, -10.32) * mm});
            skLineSegment(sketch, "E793", {"start": v(7.3, -10.32) * mm, "end": v(7.41, -10.41) * mm});
            skLineSegment(sketch, "E794", {"start": v(7.41, -10.41) * mm, "end": v(7.54, -10.51) * mm});
            skLineSegment(sketch, "E795", {"start": v(7.54, -10.51) * mm, "end": v(7.7, -10.62) * mm});
            skLineSegment(sketch, "E796", {"start": v(7.7, -10.62) * mm, "end": v(7.88, -10.73) * mm});
            skLineSegment(sketch, "E797", {"start": v(7.88, -10.73) * mm, "end": v(8.07, -10.84) * mm});
            skLineSegment(sketch, "E798", {"start": v(8.07, -10.84) * mm, "end": v(8.24, -10.73) * mm});
            skLineSegment(sketch, "E799", {"start": v(8.24, -10.73) * mm, "end": v(8.39, -10.6) * mm});
            skLineSegment(sketch, "E800", {"start": v(8.39, -10.6) * mm, "end": v(8.33, -10.39) * mm});
            skLineSegment(sketch, "E801", {"start": v(8.33, -10.39) * mm, "end": v(8.26, -10.18) * mm});
            skLineSegment(sketch, "E802", {"start": v(8.26, -10.18) * mm, "end": v(8.2, -10) * mm});
            skLineSegment(sketch, "E803", {"start": v(8.2, -10) * mm, "end": v(8.14, -9.85) * mm});
            skLineSegment(sketch, "E804", {"start": v(8.14, -9.85) * mm, "end": v(8.08, -9.73) * mm});
            skLineSegment(sketch, "E805", {"start": v(8.08, -9.73) * mm, "end": v(8, -9.57) * mm});
            skLineSegment(sketch, "E806", {"start": v(8, -9.57) * mm, "end": v(7.98, -9.52) * mm});
            skLineSegment(sketch, "E807", {"start": v(7.98, -9.52) * mm, "end": v(7.99, -9.48) * mm});
            skLineSegment(sketch, "E808", {"start": v(7.99, -9.48) * mm, "end": v(8.36, -9.16) * mm});
            skLineSegment(sketch, "E809", {"start": v(8.36, -9.16) * mm, "end": v(8.4, -9.16) * mm});
            skLineSegment(sketch, "E810", {"start": v(8.4, -9.16) * mm, "end": v(8.44, -9.18) * mm});
            skLineSegment(sketch, "E811", {"start": v(8.44, -9.18) * mm, "end": v(8.59, -9.28) * mm});
            skLineSegment(sketch, "E812", {"start": v(8.59, -9.28) * mm, "end": v(8.7, -9.35) * mm});
            skLineSegment(sketch, "E813", {"start": v(8.7, -9.35) * mm, "end": v(8.85, -9.44) * mm});
            skLineSegment(sketch, "E814", {"start": v(8.85, -9.44) * mm, "end": v(9.02, -9.52) * mm});
            skLineSegment(sketch, "E815", {"start": v(9.02, -9.52) * mm, "end": v(9.2, -9.61) * mm});
            skLineSegment(sketch, "E816", {"start": v(9.2, -9.61) * mm, "end": v(9.42, -9.7) * mm});
            skLineSegment(sketch, "E817", {"start": v(9.42, -9.7) * mm, "end": v(9.57, -9.57) * mm});
            skLineSegment(sketch, "E818", {"start": v(9.57, -9.57) * mm, "end": v(9.7, -9.42) * mm});
            skLineSegment(sketch, "E819", {"start": v(9.7, -9.42) * mm, "end": v(9.61, -9.2) * mm});
            skLineSegment(sketch, "E820", {"start": v(9.61, -9.2) * mm, "end": v(9.52, -9.02) * mm});
            skLineSegment(sketch, "E821", {"start": v(9.52, -9.02) * mm, "end": v(9.44, -8.85) * mm});
            skLineSegment(sketch, "E822", {"start": v(9.44, -8.85) * mm, "end": v(9.35, -8.7) * mm});
            skLineSegment(sketch, "E823", {"start": v(9.35, -8.7) * mm, "end": v(9.28, -8.59) * mm});
            skLineSegment(sketch, "E824", {"start": v(9.28, -8.59) * mm, "end": v(9.18, -8.44) * mm});
            skLineSegment(sketch, "E825", {"start": v(9.18, -8.44) * mm, "end": v(9.16, -8.4) * mm});
            skLineSegment(sketch, "E826", {"start": v(9.16, -8.4) * mm, "end": v(9.16, -8.36) * mm});
            skLineSegment(sketch, "E827", {"start": v(9.16, -8.36) * mm, "end": v(9.48, -7.99) * mm});
            skLineSegment(sketch, "E828", {"start": v(9.48, -7.99) * mm, "end": v(9.52, -7.98) * mm});
            skLineSegment(sketch, "E829", {"start": v(9.52, -7.98) * mm, "end": v(9.57, -8) * mm});
            skLineSegment(sketch, "E830", {"start": v(9.57, -8) * mm, "end": v(9.73, -8.08) * mm});
            skLineSegment(sketch, "E831", {"start": v(9.73, -8.08) * mm, "end": v(9.85, -8.14) * mm});
            skLineSegment(sketch, "E832", {"start": v(9.85, -8.14) * mm, "end": v(10, -8.2) * mm});
            skLineSegment(sketch, "E833", {"start": v(10, -8.2) * mm, "end": v(10.18, -8.26) * mm});
            skLineSegment(sketch, "E834", {"start": v(10.18, -8.26) * mm, "end": v(10.39, -8.33) * mm});
            skLineSegment(sketch, "E835", {"start": v(10.39, -8.33) * mm, "end": v(10.6, -8.39) * mm});
            skLineSegment(sketch, "E836", {"start": v(10.6, -8.39) * mm, "end": v(10.73, -8.24) * mm});
            skLineSegment(sketch, "E837", {"start": v(10.73, -8.24) * mm, "end": v(10.84, -8.07) * mm});
            skLineSegment(sketch, "E838", {"start": v(10.84, -8.07) * mm, "end": v(10.73, -7.88) * mm});
            skLineSegment(sketch, "E839", {"start": v(10.73, -7.88) * mm, "end": v(10.62, -7.7) * mm});
            skLineSegment(sketch, "E840", {"start": v(10.62, -7.7) * mm, "end": v(10.51, -7.54) * mm});
            skLineSegment(sketch, "E841", {"start": v(10.51, -7.54) * mm, "end": v(10.41, -7.41) * mm});
            skLineSegment(sketch, "E842", {"start": v(10.41, -7.41) * mm, "end": v(10.32, -7.3) * mm});
            skLineSegment(sketch, "E843", {"start": v(10.32, -7.3) * mm, "end": v(10.2, -7.17) * mm});
            skLineSegment(sketch, "E844", {"start": v(10.2, -7.17) * mm, "end": v(10.17, -7.13) * mm});
            skLineSegment(sketch, "E845", {"start": v(10.17, -7.13) * mm, "end": v(10.17, -7.1) * mm});
            skLineSegment(sketch, "E846", {"start": v(10.17, -7.1) * mm, "end": v(10.45, -6.68) * mm});
            skLineSegment(sketch, "E847", {"start": v(10.45, -6.68) * mm, "end": v(10.48, -6.67) * mm});
            skLineSegment(sketch, "E848", {"start": v(10.48, -6.67) * mm, "end": v(10.53, -6.68) * mm});
            skLineSegment(sketch, "E849", {"start": v(10.53, -6.68) * mm, "end": v(10.7, -6.74) * mm});
            skLineSegment(sketch, "E850", {"start": v(10.7, -6.74) * mm, "end": v(10.83, -6.78) * mm});
            skLineSegment(sketch, "E851", {"start": v(10.83, -6.78) * mm, "end": v(11, -6.82) * mm});
            skLineSegment(sketch, "E852", {"start": v(11, -6.82) * mm, "end": v(11.18, -6.86) * mm});
            skLineSegment(sketch, "E853", {"start": v(11.18, -6.86) * mm, "end": v(11.38, -6.9) * mm});
            skLineSegment(sketch, "E854", {"start": v(11.38, -6.9) * mm, "end": v(11.6, -6.93) * mm});
            skLineSegment(sketch, "E855", {"start": v(11.6, -6.93) * mm, "end": v(11.72, -6.76) * mm});
            skLineSegment(sketch, "E856", {"start": v(11.72, -6.76) * mm, "end": v(11.8, -6.59) * mm});
            skLineSegment(sketch, "E857", {"start": v(11.8, -6.59) * mm, "end": v(11.67, -6.4) * mm});
            skLineSegment(sketch, "E858", {"start": v(11.67, -6.4) * mm, "end": v(11.53, -6.25) * mm});
            skLineSegment(sketch, "E859", {"start": v(11.53, -6.25) * mm, "end": v(11.4, -6.1) * mm});
            skLineSegment(sketch, "E860", {"start": v(11.4, -6.1) * mm, "end": v(11.29, -5.99) * mm});
            skLineSegment(sketch, "E861", {"start": v(11.29, -5.99) * mm, "end": v(11.19, -5.9) * mm});
            skLineSegment(sketch, "E862", {"start": v(11.19, -5.9) * mm, "end": v(11.05, -5.78) * mm});
            skLineSegment(sketch, "E863", {"start": v(11.05, -5.78) * mm, "end": v(11.02, -5.74) * mm});
            skLineSegment(sketch, "E864", {"start": v(11.02, -5.74) * mm, "end": v(11, -5.7) * mm});
            skLineSegment(sketch, "E865", {"start": v(11, -5.7) * mm, "end": v(11.23, -5.26) * mm});
            skLineSegment(sketch, "E866", {"start": v(11.23, -5.26) * mm, "end": v(11.26, -5.25) * mm});
            skLineSegment(sketch, "E867", {"start": v(11.26, -5.25) * mm, "end": v(11.31, -5.25) * mm});
            skLineSegment(sketch, "E868", {"start": v(11.31, -5.25) * mm, "end": v(11.49, -5.29) * mm});
            skLineSegment(sketch, "E869", {"start": v(11.49, -5.29) * mm, "end": v(11.62, -5.31) * mm});
            skLineSegment(sketch, "E870", {"start": v(11.62, -5.31) * mm, "end": v(11.79, -5.33) * mm});
            skLineSegment(sketch, "E871", {"start": v(11.79, -5.33) * mm, "end": v(11.98, -5.35) * mm});
            skLineSegment(sketch, "E872", {"start": v(11.98, -5.35) * mm, "end": v(12.19, -5.36) * mm});
            skLineSegment(sketch, "E873", {"start": v(12.19, -5.36) * mm, "end": v(12.41, -5.36) * mm});
            skLineSegment(sketch, "E874", {"start": v(12.41, -5.36) * mm, "end": v(12.5, -5.18) * mm});
            skLineSegment(sketch, "E875", {"start": v(12.5, -5.18) * mm, "end": v(12.56, -4.99) * mm});
            skLineSegment(sketch, "E876", {"start": v(12.56, -4.99) * mm, "end": v(12.4, -4.83) * mm});
            skLineSegment(sketch, "E877", {"start": v(12.4, -4.83) * mm, "end": v(12.25, -4.69) * mm});
            skLineSegment(sketch, "E878", {"start": v(12.25, -4.69) * mm, "end": v(12.1, -4.57) * mm});
            skLineSegment(sketch, "E879", {"start": v(12.1, -4.57) * mm, "end": v(11.97, -4.47) * mm});
            skLineSegment(sketch, "E880", {"start": v(11.97, -4.47) * mm, "end": v(11.86, -4.38) * mm});
            skLineSegment(sketch, "E881", {"start": v(11.86, -4.38) * mm, "end": v(11.71, -4.29) * mm});
            skLineSegment(sketch, "E882", {"start": v(11.71, -4.29) * mm, "end": v(11.67, -4.25) * mm});
            skLineSegment(sketch, "E883", {"start": v(11.67, -4.25) * mm, "end": v(11.66, -4.22) * mm});
            skLineSegment(sketch, "E884", {"start": v(11.66, -4.22) * mm, "end": v(11.82, -3.75) * mm});
            skLineSegment(sketch, "E885", {"start": v(11.82, -3.75) * mm, "end": v(11.85, -3.73) * mm});
            skLineSegment(sketch, "E886", {"start": v(11.85, -3.73) * mm, "end": v(11.9, -3.73) * mm});
            skLineSegment(sketch, "E887", {"start": v(11.9, -3.73) * mm, "end": v(12.08, -3.74) * mm});
            skLineSegment(sketch, "E888", {"start": v(12.08, -3.74) * mm, "end": v(12.22, -3.75) * mm});
            skLineSegment(sketch, "E889", {"start": v(12.22, -3.75) * mm, "end": v(12.38, -3.75) * mm});
            skLineSegment(sketch, "E890", {"start": v(12.38, -3.75) * mm, "end": v(12.57, -3.74) * mm});
            skLineSegment(sketch, "E891", {"start": v(12.57, -3.74) * mm, "end": v(12.78, -3.72) * mm});
            skLineSegment(sketch, "E892", {"start": v(12.78, -3.72) * mm, "end": v(13, -3.69) * mm});
            skLineSegment(sketch, "E893", {"start": v(13, -3.69) * mm, "end": v(13.07, -3.5) * mm});
            skLineSegment(sketch, "E894", {"start": v(13.07, -3.5) * mm, "end": v(13.1, -3.3) * mm});
            skLineSegment(sketch, "E895", {"start": v(13.1, -3.3) * mm, "end": v(12.93, -3.17) * mm});
            skLineSegment(sketch, "E896", {"start": v(12.93, -3.17) * mm, "end": v(12.76, -3.05) * mm});
            skLineSegment(sketch, "E897", {"start": v(12.76, -3.05) * mm, "end": v(12.6, -2.95) * mm});
            skLineSegment(sketch, "E898", {"start": v(12.6, -2.95) * mm, "end": v(12.46, -2.86) * mm});
            skLineSegment(sketch, "E899", {"start": v(12.46, -2.86) * mm, "end": v(12.33, -2.8) * mm});
            skLineSegment(sketch, "E900", {"start": v(12.33, -2.8) * mm, "end": v(12.17, -2.72) * mm});
            skLineSegment(sketch, "E901", {"start": v(12.17, -2.72) * mm, "end": v(12.13, -2.7) * mm});
            skLineSegment(sketch, "E902", {"start": v(12.13, -2.7) * mm, "end": v(12.1, -2.66) * mm});
            skLineSegment(sketch, "E903", {"start": v(12.1, -2.66) * mm, "end": v(12.2, -2.17) * mm});
            skLineSegment(sketch, "E904", {"start": v(12.2, -2.17) * mm, "end": v(12.23, -2.15) * mm});
            skLineSegment(sketch, "E905", {"start": v(12.23, -2.15) * mm, "end": v(12.29, -2.14) * mm});
            skLineSegment(sketch, "E906", {"start": v(12.29, -2.14) * mm, "end": v(12.46, -2.13) * mm});
            skLineSegment(sketch, "E907", {"start": v(12.46, -2.13) * mm, "end": v(12.6, -2.12) * mm});
            skLineSegment(sketch, "E908", {"start": v(12.6, -2.12) * mm, "end": v(12.77, -2.1) * mm});
            skLineSegment(sketch, "E909", {"start": v(12.77, -2.1) * mm, "end": v(12.95, -2.07) * mm});
            skLineSegment(sketch, "E910", {"start": v(12.95, -2.07) * mm, "end": v(13.16, -2.02) * mm});
            skLineSegment(sketch, "E911", {"start": v(13.16, -2.02) * mm, "end": v(13.37, -1.96) * mm});
            skLineSegment(sketch, "E912", {"start": v(0.42, -1.96) * mm, "end": v(0, -2) * mm});
            skLineSegment(sketch, "E913", {"start": v(0, -2) * mm, "end": v(-0.42, -1.96) * mm});
            skLineSegment(sketch, "E914", {"start": v(-0.42, -1.96) * mm, "end": v(-0.81, -1.83) * mm});
            skLineSegment(sketch, "E915", {"start": v(-0.81, -1.83) * mm, "end": v(-1.18, -1.62) * mm});
            skLineSegment(sketch, "E916", {"start": v(-1.18, -1.62) * mm, "end": v(-1.49, -1.34) * mm});
            skLineSegment(sketch, "E917", {"start": v(-1.49, -1.34) * mm, "end": v(-1.73, -1) * mm});
            skLineSegment(sketch, "E918", {"start": v(-1.73, -1) * mm, "end": v(-1.9, -0.62) * mm});
            skLineSegment(sketch, "E919", {"start": v(-1.9, -0.62) * mm, "end": v(-1.99, -0.2) * mm});
            skLineSegment(sketch, "E920", {"start": v(-1.99, -0.2) * mm, "end": v(-1.99, 0.2) * mm});
            skLineSegment(sketch, "E921", {"start": v(-1.99, 0.2) * mm, "end": v(-1.9, 0.62) * mm});
            skLineSegment(sketch, "E922", {"start": v(-1.9, 0.62) * mm, "end": v(-1.73, 1) * mm});
            skLineSegment(sketch, "E923", {"start": v(-1.73, 1) * mm, "end": v(-1.49, 1.34) * mm});
            skLineSegment(sketch, "E924", {"start": v(-1.49, 1.34) * mm, "end": v(-1.18, 1.62) * mm});
            skLineSegment(sketch, "E925", {"start": v(-1.18, 1.62) * mm, "end": v(-0.81, 1.83) * mm});
            skLineSegment(sketch, "E926", {"start": v(-0.81, 1.83) * mm, "end": v(-0.42, 1.96) * mm});
            skLineSegment(sketch, "E927", {"start": v(-0.42, 1.96) * mm, "end": v(0, 2) * mm});
            skLineSegment(sketch, "E928", {"start": v(0, 2) * mm, "end": v(0.42, 1.96) * mm});
            skLineSegment(sketch, "E929", {"start": v(0.42, 1.96) * mm, "end": v(0.81, 1.83) * mm});
            skLineSegment(sketch, "E930", {"start": v(0.81, 1.83) * mm, "end": v(1.18, 1.62) * mm});
            skLineSegment(sketch, "E931", {"start": v(1.18, 1.62) * mm, "end": v(1.49, 1.34) * mm});
            skLineSegment(sketch, "E932", {"start": v(1.49, 1.34) * mm, "end": v(1.73, 1) * mm});
            skLineSegment(sketch, "E933", {"start": v(1.73, 1) * mm, "end": v(1.9, 0.62) * mm});
            skLineSegment(sketch, "E934", {"start": v(1.9, 0.62) * mm, "end": v(1.99, 0.2) * mm});
            skLineSegment(sketch, "E935", {"start": v(1.99, 0.2) * mm, "end": v(1.99, -0.2) * mm});
            skLineSegment(sketch, "E936", {"start": v(1.99, -0.2) * mm, "end": v(1.9, -0.62) * mm});
            skLineSegment(sketch, "E937", {"start": v(1.9, -0.62) * mm, "end": v(1.73, -1) * mm});
            skLineSegment(sketch, "E938", {"start": v(1.73, -1) * mm, "end": v(1.49, -1.34) * mm});
            skLineSegment(sketch, "E939", {"start": v(1.49, -1.34) * mm, "end": v(1.18, -1.62) * mm});
            skLineSegment(sketch, "E940", {"start": v(1.18, -1.62) * mm, "end": v(0.81, -1.83) * mm});
            skLineSegment(sketch, "E941", {"start": v(0.81, -1.83) * mm, "end": v(0.42, -1.96) * mm});
            skCircle(sketch, "E942", {"center": v(0, 0) * mm, "radius": 13.53 * mm, "construction": true});
            skCircle(sketch, "E943", {"center": v(0, 0) * mm, "radius": 16 * mm});
            skSolve(sketch);
        }
        {
            var Q0;
            Q0=makeQuery(id+"F0.imprint","IMPRINT",FACE,{"disambiguationData":[TD([[makeQuery(id+"F0.imprint","IMPRINT",EDGE,{"derivedFrom":sQuery(id+"F0.wireOp",EDGE,"E0")}),-1.0]])]});
            var Q1;
            Q1 = qConstructionFilter(qBodyType(qCreatedBy(id + "F0" ,EDGE), BodyType.WIRE), ConstructionObject.NO);
            extrude(context, id + "F1", {"entities" : qUnion([Q0]), "surfaceEntities" : qUnion([Q1]), "depth" : 8 * mm, "offsetDistance" : 25 * mm});
        }
        {
            var Q0;
            Q0=makeQuery(id+"F1.opExtrude","CAP_EDGE",EDGE,{"disambiguationData":[OSD([sQuery(id+"F0.wireOp",EDGE,"E943")])],"isStart":false});
            chamfer(context, id + "F2", {"entities" : qUnion([Q0]), "width" : 1.5 * mm, "tangentPropagation" : true});
        }
        {
            var Q0;
            Q0=qCreatedBy(makeId("Top.planeOp"),FACE);
            var sketch = newSketch(context, id + "F3", { "sketchPlane" : qUnion([Q0])});
            skCircle(sketch, "E944", {"center": v(0, 0) * mm, "radius": 16 * mm});
            skSolve(sketch);
        }
        {
            var Q0;
            Q0=makeQuery(id+"F3.imprint","IMPRINT",FACE,{"disambiguationData":[TD([[makeQuery(id+"F3.imprint","IMPRINT",EDGE,{"derivedFrom":sQuery(id+"F3.wireOp",EDGE,"E944")}),1.0]])]});
            extrude(context, id + "F4", {"entities" : qUnion([Q0]), "operationType" : NewBodyOperationType.ADD, "depth" : 0.6 * mm, "offsetDistance" : 25 * mm});
        }
        {
            var Q0;
            Q0=makeQuery(id+"F1.opExtrude","CAP_EDGE",EDGE,{"disambiguationData":[OSD([sQuery(id+"F0.wireOp",EDGE,"E892")])],"isStart":false});
            var Q1;
            Q1=makeQuery(id+"F1.opExtrude","CAP_EDGE",EDGE,{"disambiguationData":[OSD([sQuery(id+"F0.wireOp",EDGE,"E891")])],"isStart":false});
            var Q2;
            Q2=makeQuery(id+"F1.opExtrude","CAP_EDGE",EDGE,{"disambiguationData":[OSD([sQuery(id+"F0.wireOp",EDGE,"E890")])],"isStart":false});
            var Q3;
            Q3=makeQuery(id+"F1.opExtrude","CAP_EDGE",EDGE,{"disambiguationData":[OSD([sQuery(id+"F0.wireOp",EDGE,"E889")])],"isStart":false});
            var Q4;
            Q4=makeQuery(id+"F1.opExtrude","CAP_EDGE",EDGE,{"disambiguationData":[OSD([sQuery(id+"F0.wireOp",EDGE,"E888")])],"isStart":false});
            var Q5;
            Q5=makeQuery(id+"F1.opExtrude","CAP_EDGE",EDGE,{"disambiguationData":[OSD([sQuery(id+"F0.wireOp",EDGE,"E887")])],"isStart":false});
            var Q6;
            Q6=makeQuery(id+"F1.opExtrude","CAP_EDGE",EDGE,{"disambiguationData":[OSD([sQuery(id+"F0.wireOp",EDGE,"E886")])],"isStart":false});
            var Q7;
            Q7=makeQuery(id+"F1.opExtrude","CAP_EDGE",EDGE,{"disambiguationData":[OSD([sQuery(id+"F0.wireOp",EDGE,"E881")])],"isStart":false});
            var Q8;
            Q8=makeQuery(id+"F1.opExtrude","CAP_EDGE",EDGE,{"disambiguationData":[OSD([sQuery(id+"F0.wireOp",EDGE,"E870")])],"isStart":false});
            var Q9;
            Q9=makeQuery(id+"F1.opExtrude","CAP_EDGE",EDGE,{"disambiguationData":[OSD([sQuery(id+"F0.wireOp",EDGE,"E860")])],"isStart":false});
            var Q10;
            Q10=makeQuery(id+"F1.opExtrude","CAP_EDGE",EDGE,{"disambiguationData":[OSD([sQuery(id+"F0.wireOp",EDGE,"E851")])],"isStart":false});
            var Q11;
            Q11=makeQuery(id+"F1.opExtrude","CAP_EDGE",EDGE,{"disambiguationData":[OSD([sQuery(id+"F0.wireOp",EDGE,"E841")])],"isStart":false});
            var Q12;
            Q12=makeQuery(id+"F1.opExtrude","CAP_EDGE",EDGE,{"disambiguationData":[OSD([sQuery(id+"F0.wireOp",EDGE,"E832")])],"isStart":false});
            var Q13;
            Q13=makeQuery(id+"F1.opExtrude","CAP_EDGE",EDGE,{"disambiguationData":[OSD([sQuery(id+"F0.wireOp",EDGE,"E822")])],"isStart":false});
            var Q14;
            Q14=makeQuery(id+"F1.opExtrude","CAP_EDGE",EDGE,{"disambiguationData":[OSD([sQuery(id+"F0.wireOp",EDGE,"E813")])],"isStart":false});
            var Q15;
            Q15=makeQuery(id+"F1.opExtrude","CAP_EDGE",EDGE,{"disambiguationData":[OSD([sQuery(id+"F0.wireOp",EDGE,"E802")])],"isStart":false});
            var Q16;
            Q16=makeQuery(id+"F1.opExtrude","CAP_EDGE",EDGE,{"disambiguationData":[OSD([sQuery(id+"F0.wireOp",EDGE,"E794")])],"isStart":false});
            var Q17;
            Q17=makeQuery(id+"F1.opExtrude","CAP_EDGE",EDGE,{"disambiguationData":[OSD([sQuery(id+"F0.wireOp",EDGE,"E784")])],"isStart":false});
            var Q18;
            Q18=makeQuery(id+"F1.opExtrude","CAP_EDGE",EDGE,{"disambiguationData":[OSD([sQuery(id+"F0.wireOp",EDGE,"E775")])],"isStart":false});
            var Q19;
            Q19=makeQuery(id+"F1.opExtrude","CAP_EDGE",EDGE,{"disambiguationData":[OSD([sQuery(id+"F0.wireOp",EDGE,"E765")])],"isStart":false});
            var Q20;
            Q20=makeQuery(id+"F1.opExtrude","CAP_EDGE",EDGE,{"disambiguationData":[OSD([sQuery(id+"F0.wireOp",EDGE,"E756")])],"isStart":false});
            var Q21;
            Q21=makeQuery(id+"F1.opExtrude","CAP_EDGE",EDGE,{"disambiguationData":[OSD([sQuery(id+"F0.wireOp",EDGE,"E746")])],"isStart":false});
            chamfer(context, id + "F5", {"entities" : qUnion([Q0, Q1, Q2, Q3, Q4, Q5, Q6, Q7, Q8, Q9, Q10, Q11, Q12, Q13, Q14, Q15, Q16, Q17, Q18, Q19, Q20, Q21]), "width" : 0.3 * mm, "tangentPropagation" : true});
        }
        {
            var Q0;
            Q0=qCreatedBy(makeId("Right.planeOp"),FACE);
            var sketch = newSketch(context, id + "F6", { "sketchPlane" : qUnion([Q0])});
            skLineSegment(sketch, "E945", {"start": v(-16.5, 5.39) * mm, "end": v(-15.44, 4.75) * mm});
            skLineSegment(sketch, "E946", {"start": v(-15.44, 4.75) * mm, "end": v(-15.44, 2.05) * mm});
            skLineSegment(sketch, "E947", {"start": v(-15.44, 2.05) * mm, "end": v(-16.5, 2.05) * mm});
            skLineSegment(sketch, "E948", {"start": v(-16.5, 2.05) * mm, "end": v(-16.5, 5.39) * mm});
            skSolve(sketch);
        }
        {
            var Q0;
            Q0=qCreatedBy(makeId("Right.planeOp"),FACE);
            var sketch = newSketch(context, id + "F7", { "sketchPlane" : qUnion([Q0])});
            skLineSegment(sketch, "E949", {"start": v(0, 0) * mm, "end": v(0, 28.16) * mm});
            skSolve(sketch);
        }
        {
            var Q0;
            Q0=makeQuery(id+"F6.imprint","IMPRINT",FACE,{"disambiguationData":[TD([[makeQuery(id+"F6.imprint","IMPRINT",EDGE,{"derivedFrom":sQuery(id+"F6.wireOp",EDGE,"E945")}),-1.0]])]});
            var Q1;
            Q1=sQuery(id+"F7.wireOp",EDGE,"E949");
            revolve(context, id + "F8", {"operationType" : NewBodyOperationType.REMOVE, "entities" : qUnion([Q0]), "axis" : qUnion([Q1]), "revolveType" : RevolveType.FULL, "oppositeDirection" : true});
        }
        {
            var Q0;
            Q0=makeQuery(id+"F1.opExtrude","CAP_EDGE",EDGE,{"disambiguationData":[OSD([sQuery(id+"F0.wireOp",EDGE,"E740")])],"isStart":false});
            var Q1;
            Q1=makeQuery(id+"F1.opExtrude","CAP_EDGE",EDGE,{"disambiguationData":[OSD([sQuery(id+"F0.wireOp",EDGE,"E739")])],"isStart":false});
            var Q2;
            Q2=makeQuery(id+"F1.opExtrude","CAP_EDGE",EDGE,{"disambiguationData":[OSD([sQuery(id+"F0.wireOp",EDGE,"E728")])],"isStart":false});
            var Q3;
            Q3=makeQuery(id+"F1.opExtrude","CAP_EDGE",EDGE,{"disambiguationData":[OSD([sQuery(id+"F0.wireOp",EDGE,"E727")])],"isStart":false});
            var Q4;
            Q4=makeQuery(id+"F1.opExtrude","CAP_EDGE",EDGE,{"disambiguationData":[OSD([sQuery(id+"F0.wireOp",EDGE,"E720")])],"isStart":false});
            var Q5;
            Q5=makeQuery(id+"F1.opExtrude","CAP_EDGE",EDGE,{"disambiguationData":[OSD([sQuery(id+"F0.wireOp",EDGE,"E719")])],"isStart":false});
            var Q6;
            Q6=makeQuery(id+"F1.opExtrude","CAP_EDGE",EDGE,{"disambiguationData":[OSD([sQuery(id+"F0.wireOp",EDGE,"E708")])],"isStart":false});
            var Q7;
            Q7=makeQuery(id+"F1.opExtrude","CAP_EDGE",EDGE,{"disambiguationData":[OSD([sQuery(id+"F0.wireOp",EDGE,"E707")])],"isStart":false});
            var Q8;
            Q8=makeQuery(id+"F1.opExtrude","CAP_EDGE",EDGE,{"disambiguationData":[OSD([sQuery(id+"F0.wireOp",EDGE,"E699")])],"isStart":false});
            var Q9;
            Q9=makeQuery(id+"F1.opExtrude","CAP_EDGE",EDGE,{"disambiguationData":[OSD([sQuery(id+"F0.wireOp",EDGE,"E700")])],"isStart":false});
            var Q10;
            Q10=makeQuery(id+"F1.opExtrude","CAP_EDGE",EDGE,{"disambiguationData":[OSD([sQuery(id+"F0.wireOp",EDGE,"E689")])],"isStart":false});
            var Q11;
            Q11=makeQuery(id+"F1.opExtrude","CAP_EDGE",EDGE,{"disambiguationData":[OSD([sQuery(id+"F0.wireOp",EDGE,"E688")])],"isStart":false});
            var Q12;
            Q12=makeQuery(id+"F1.opExtrude","CAP_EDGE",EDGE,{"disambiguationData":[OSD([sQuery(id+"F0.wireOp",EDGE,"E681")])],"isStart":false});
            var Q13;
            Q13=makeQuery(id+"F1.opExtrude","CAP_EDGE",EDGE,{"disambiguationData":[OSD([sQuery(id+"F0.wireOp",EDGE,"E680")])],"isStart":false});
            var Q14;
            Q14=makeQuery(id+"F1.opExtrude","CAP_EDGE",EDGE,{"disambiguationData":[OSD([sQuery(id+"F0.wireOp",EDGE,"E670")])],"isStart":false});
            var Q15;
            Q15=makeQuery(id+"F1.opExtrude","CAP_EDGE",EDGE,{"disambiguationData":[OSD([sQuery(id+"F0.wireOp",EDGE,"E669")])],"isStart":false});
            var Q16;
            Q16=makeQuery(id+"F1.opExtrude","CAP_EDGE",EDGE,{"disambiguationData":[OSD([sQuery(id+"F0.wireOp",EDGE,"E662")])],"isStart":false});
            var Q17;
            Q17=makeQuery(id+"F1.opExtrude","CAP_EDGE",EDGE,{"disambiguationData":[OSD([sQuery(id+"F0.wireOp",EDGE,"E661")])],"isStart":false});
            var Q18;
            Q18=makeQuery(id+"F1.opExtrude","CAP_EDGE",EDGE,{"disambiguationData":[OSD([sQuery(id+"F0.wireOp",EDGE,"E651")])],"isStart":false});
            var Q19;
            Q19=makeQuery(id+"F1.opExtrude","CAP_EDGE",EDGE,{"disambiguationData":[OSD([sQuery(id+"F0.wireOp",EDGE,"E650")])],"isStart":false});
            var Q20;
            Q20=makeQuery(id+"F1.opExtrude","CAP_EDGE",EDGE,{"disambiguationData":[OSD([sQuery(id+"F0.wireOp",EDGE,"E643")])],"isStart":false});
            var Q21;
            Q21=makeQuery(id+"F1.opExtrude","CAP_EDGE",EDGE,{"disambiguationData":[OSD([sQuery(id+"F0.wireOp",EDGE,"E642")])],"isStart":false});
            var Q22;
            Q22=makeQuery(id+"F1.opExtrude","CAP_EDGE",EDGE,{"disambiguationData":[OSD([sQuery(id+"F0.wireOp",EDGE,"E633")])],"isStart":false});
            var Q23;
            Q23=makeQuery(id+"F1.opExtrude","CAP_EDGE",EDGE,{"disambiguationData":[OSD([sQuery(id+"F0.wireOp",EDGE,"E632")])],"isStart":false});
            var Q24;
            Q24=makeQuery(id+"F1.opExtrude","CAP_EDGE",EDGE,{"disambiguationData":[OSD([sQuery(id+"F0.wireOp",EDGE,"E624")])],"isStart":false});
            var Q25;
            Q25=makeQuery(id+"F1.opExtrude","CAP_EDGE",EDGE,{"disambiguationData":[OSD([sQuery(id+"F0.wireOp",EDGE,"E623")])],"isStart":false});
            var Q26;
            Q26=makeQuery(id+"F1.opExtrude","CAP_EDGE",EDGE,{"disambiguationData":[OSD([sQuery(id+"F0.wireOp",EDGE,"E613")])],"isStart":false});
            var Q27;
            Q27=makeQuery(id+"F1.opExtrude","CAP_EDGE",EDGE,{"disambiguationData":[OSD([sQuery(id+"F0.wireOp",EDGE,"E612")])],"isStart":false});
            var Q28;
            Q28=makeQuery(id+"F1.opExtrude","CAP_EDGE",EDGE,{"disambiguationData":[OSD([sQuery(id+"F0.wireOp",EDGE,"E605")])],"isStart":false});
            var Q29;
            Q29=makeQuery(id+"F1.opExtrude","CAP_EDGE",EDGE,{"disambiguationData":[OSD([sQuery(id+"F0.wireOp",EDGE,"E604")])],"isStart":false});
            var Q30;
            Q30=makeQuery(id+"F1.opExtrude","CAP_EDGE",EDGE,{"disambiguationData":[OSD([sQuery(id+"F0.wireOp",EDGE,"E594")])],"isStart":false});
            var Q31;
            Q31=makeQuery(id+"F1.opExtrude","CAP_EDGE",EDGE,{"disambiguationData":[OSD([sQuery(id+"F0.wireOp",EDGE,"E593")])],"isStart":false});
            var Q32;
            Q32=makeQuery(id+"F1.opExtrude","CAP_EDGE",EDGE,{"disambiguationData":[OSD([sQuery(id+"F0.wireOp",EDGE,"E585")])],"isStart":false});
            var Q33;
            Q33=makeQuery(id+"F1.opExtrude","CAP_EDGE",EDGE,{"disambiguationData":[OSD([sQuery(id+"F0.wireOp",EDGE,"E586")])],"isStart":false});
            var Q34;
            Q34=makeQuery(id+"F1.opExtrude","CAP_EDGE",EDGE,{"disambiguationData":[OSD([sQuery(id+"F0.wireOp",EDGE,"E575")])],"isStart":false});
            var Q35;
            Q35=makeQuery(id+"F1.opExtrude","CAP_EDGE",EDGE,{"disambiguationData":[OSD([sQuery(id+"F0.wireOp",EDGE,"E574")])],"isStart":false});
            var Q36;
            Q36=makeQuery(id+"F1.opExtrude","CAP_EDGE",EDGE,{"disambiguationData":[OSD([sQuery(id+"F0.wireOp",EDGE,"E567")])],"isStart":false});
            var Q37;
            Q37=makeQuery(id+"F1.opExtrude","CAP_EDGE",EDGE,{"disambiguationData":[OSD([sQuery(id+"F0.wireOp",EDGE,"E566")])],"isStart":false});
            var Q38;
            Q38=makeQuery(id+"F1.opExtrude","CAP_EDGE",EDGE,{"disambiguationData":[OSD([sQuery(id+"F0.wireOp",EDGE,"E556")])],"isStart":false});
            var Q39;
            Q39=makeQuery(id+"F1.opExtrude","CAP_EDGE",EDGE,{"disambiguationData":[OSD([sQuery(id+"F0.wireOp",EDGE,"E555")])],"isStart":false});
            var Q40;
            Q40=makeQuery(id+"F1.opExtrude","CAP_EDGE",EDGE,{"disambiguationData":[OSD([sQuery(id+"F0.wireOp",EDGE,"E548")])],"isStart":false});
            var Q41;
            Q41=makeQuery(id+"F1.opExtrude","CAP_EDGE",EDGE,{"disambiguationData":[OSD([sQuery(id+"F0.wireOp",EDGE,"E547")])],"isStart":false});
            var Q42;
            Q42=makeQuery(id+"F1.opExtrude","CAP_EDGE",EDGE,{"disambiguationData":[OSD([sQuery(id+"F0.wireOp",EDGE,"E537")])],"isStart":false});
            var Q43;
            Q43=makeQuery(id+"F1.opExtrude","CAP_EDGE",EDGE,{"disambiguationData":[OSD([sQuery(id+"F0.wireOp",EDGE,"E536")])],"isStart":false});
            var Q44;
            Q44=makeQuery(id+"F1.opExtrude","CAP_EDGE",EDGE,{"disambiguationData":[OSD([sQuery(id+"F0.wireOp",EDGE,"E529")])],"isStart":false});
            var Q45;
            Q45=makeQuery(id+"F1.opExtrude","CAP_EDGE",EDGE,{"disambiguationData":[OSD([sQuery(id+"F0.wireOp",EDGE,"E530")])],"isStart":false});
            var Q46;
            Q46=makeQuery(id+"F1.opExtrude","CAP_EDGE",EDGE,{"disambiguationData":[OSD([sQuery(id+"F0.wireOp",EDGE,"E518")])],"isStart":false});
            var Q47;
            Q47=makeQuery(id+"F1.opExtrude","CAP_EDGE",EDGE,{"disambiguationData":[OSD([sQuery(id+"F0.wireOp",EDGE,"E517")])],"isStart":false});
            var Q48;
            Q48=makeQuery(id+"F1.opExtrude","CAP_EDGE",EDGE,{"disambiguationData":[OSD([sQuery(id+"F0.wireOp",EDGE,"E511")])],"isStart":false});
            var Q49;
            Q49=makeQuery(id+"F1.opExtrude","CAP_EDGE",EDGE,{"disambiguationData":[OSD([sQuery(id+"F0.wireOp",EDGE,"E510")])],"isStart":false});
            var Q50;
            Q50=makeQuery(id+"F1.opExtrude","CAP_EDGE",EDGE,{"disambiguationData":[OSD([sQuery(id+"F0.wireOp",EDGE,"E498")])],"isStart":false});
            var Q51;
            Q51=makeQuery(id+"F1.opExtrude","CAP_EDGE",EDGE,{"disambiguationData":[OSD([sQuery(id+"F0.wireOp",EDGE,"E497")])],"isStart":false});
            var Q52;
            Q52=makeQuery(id+"F1.opExtrude","CAP_EDGE",EDGE,{"disambiguationData":[OSD([sQuery(id+"F0.wireOp",EDGE,"E490")])],"isStart":false});
            var Q53;
            Q53=makeQuery(id+"F1.opExtrude","CAP_EDGE",EDGE,{"disambiguationData":[OSD([sQuery(id+"F0.wireOp",EDGE,"E489")])],"isStart":false});
            var Q54;
            Q54=makeQuery(id+"F1.opExtrude","CAP_EDGE",EDGE,{"disambiguationData":[OSD([sQuery(id+"F0.wireOp",EDGE,"E480")])],"isStart":false});
            var Q55;
            Q55=makeQuery(id+"F1.opExtrude","CAP_EDGE",EDGE,{"disambiguationData":[OSD([sQuery(id+"F0.wireOp",EDGE,"E479")])],"isStart":false});
            var Q56;
            Q56=makeQuery(id+"F1.opExtrude","CAP_EDGE",EDGE,{"disambiguationData":[OSD([sQuery(id+"F0.wireOp",EDGE,"E472")])],"isStart":false});
            var Q57;
            Q57=makeQuery(id+"F1.opExtrude","CAP_EDGE",EDGE,{"disambiguationData":[OSD([sQuery(id+"F0.wireOp",EDGE,"E471")])],"isStart":false});
            var Q58;
            Q58=makeQuery(id+"F1.opExtrude","CAP_EDGE",EDGE,{"disambiguationData":[OSD([sQuery(id+"F0.wireOp",EDGE,"E461")])],"isStart":false});
            var Q59;
            Q59=makeQuery(id+"F1.opExtrude","CAP_EDGE",EDGE,{"disambiguationData":[OSD([sQuery(id+"F0.wireOp",EDGE,"E460")])],"isStart":false});
            var Q60;
            Q60=makeQuery(id+"F1.opExtrude","CAP_EDGE",EDGE,{"disambiguationData":[OSD([sQuery(id+"F0.wireOp",EDGE,"E454")])],"isStart":false});
            var Q61;
            Q61=makeQuery(id+"F1.opExtrude","CAP_EDGE",EDGE,{"disambiguationData":[OSD([sQuery(id+"F0.wireOp",EDGE,"E453")])],"isStart":false});
            var Q62;
            Q62=makeQuery(id+"F1.opExtrude","CAP_EDGE",EDGE,{"disambiguationData":[OSD([sQuery(id+"F0.wireOp",EDGE,"E441")])],"isStart":false});
            chamfer(context, id + "F9", {"entities" : qUnion([Q0, Q1, Q2, Q3, Q4, Q5, Q6, Q7, Q8, Q9, Q10, Q11, Q12, Q13, Q14, Q15, Q16, Q17, Q18, Q19, Q20, Q21, Q22, Q23, Q24, Q25, Q26, Q27, Q28, Q29, Q30, Q31, Q32, Q33, Q34, Q35, Q36, Q37, Q38, Q39, Q40, Q41, Q42, Q43, Q44, Q45, Q46, Q47, Q48, Q49, Q50, Q51, Q52, Q53, Q54, Q55, Q56, Q57, Q58, Q59, Q60, Q61, Q62]), "width" : 0.3 * mm, "tangentPropagation" : true});
        }
        {
            var Q0;
            Q0=makeQuery(id+"F1.opExtrude","CAP_EDGE",EDGE,{"disambiguationData":[OSD([sQuery(id+"F0.wireOp",EDGE,"E434")])],"isStart":false});
            var Q1;
            Q1=makeQuery(id+"F1.opExtrude","CAP_EDGE",EDGE,{"disambiguationData":[OSD([sQuery(id+"F0.wireOp",EDGE,"E433")])],"isStart":false});
            var Q2;
            Q2=makeQuery(id+"F1.opExtrude","CAP_EDGE",EDGE,{"disambiguationData":[OSD([sQuery(id+"F0.wireOp",EDGE,"E422")])],"isStart":false});
            var Q3;
            Q3=makeQuery(id+"F1.opExtrude","CAP_EDGE",EDGE,{"disambiguationData":[OSD([sQuery(id+"F0.wireOp",EDGE,"E421")])],"isStart":false});
            var Q4;
            Q4=makeQuery(id+"F1.opExtrude","CAP_EDGE",EDGE,{"disambiguationData":[OSD([sQuery(id+"F0.wireOp",EDGE,"E416")])],"isStart":false});
            var Q5;
            Q5=makeQuery(id+"F1.opExtrude","CAP_EDGE",EDGE,{"disambiguationData":[OSD([sQuery(id+"F0.wireOp",EDGE,"E415")])],"isStart":false});
            var Q6;
            Q6=makeQuery(id+"F1.opExtrude","CAP_EDGE",EDGE,{"disambiguationData":[OSD([sQuery(id+"F0.wireOp",EDGE,"E403")])],"isStart":false});
            var Q7;
            Q7=makeQuery(id+"F1.opExtrude","CAP_EDGE",EDGE,{"disambiguationData":[OSD([sQuery(id+"F0.wireOp",EDGE,"E402")])],"isStart":false});
            var Q8;
            Q8=makeQuery(id+"F1.opExtrude","CAP_EDGE",EDGE,{"disambiguationData":[OSD([sQuery(id+"F0.wireOp",EDGE,"E397")])],"isStart":false});
            var Q9;
            Q9=makeQuery(id+"F1.opExtrude","CAP_EDGE",EDGE,{"disambiguationData":[OSD([sQuery(id+"F0.wireOp",EDGE,"E396")])],"isStart":false});
            var Q10;
            Q10=makeQuery(id+"F1.opExtrude","CAP_EDGE",EDGE,{"disambiguationData":[OSD([sQuery(id+"F0.wireOp",EDGE,"E384")])],"isStart":false});
            var Q11;
            Q11=makeQuery(id+"F1.opExtrude","CAP_EDGE",EDGE,{"disambiguationData":[OSD([sQuery(id+"F0.wireOp",EDGE,"E383")])],"isStart":false});
            var Q12;
            Q12=makeQuery(id+"F1.opExtrude","CAP_EDGE",EDGE,{"disambiguationData":[OSD([sQuery(id+"F0.wireOp",EDGE,"E365")])],"isStart":false});
            var Q13;
            Q13=makeQuery(id+"F1.opExtrude","CAP_EDGE",EDGE,{"disambiguationData":[OSD([sQuery(id+"F0.wireOp",EDGE,"E364")])],"isStart":false});
            var Q14;
            Q14=makeQuery(id+"F1.opExtrude","CAP_EDGE",EDGE,{"disambiguationData":[OSD([sQuery(id+"F0.wireOp",EDGE,"E346")])],"isStart":false});
            var Q15;
            Q15=makeQuery(id+"F1.opExtrude","CAP_EDGE",EDGE,{"disambiguationData":[OSD([sQuery(id+"F0.wireOp",EDGE,"E347")])],"isStart":false});
            var Q16;
            Q16=makeQuery(id+"F1.opExtrude","CAP_EDGE",EDGE,{"disambiguationData":[OSD([sQuery(id+"F0.wireOp",EDGE,"E357")])],"isStart":false});
            var Q17;
            Q17=makeQuery(id+"F1.opExtrude","CAP_EDGE",EDGE,{"disambiguationData":[OSD([sQuery(id+"F0.wireOp",EDGE,"E358")])],"isStart":false});
            var Q18;
            Q18=makeQuery(id+"F1.opExtrude","CAP_EDGE",EDGE,{"disambiguationData":[OSD([sQuery(id+"F0.wireOp",EDGE,"E377")])],"isStart":false});
            var Q19;
            Q19=makeQuery(id+"F1.opExtrude","CAP_EDGE",EDGE,{"disambiguationData":[OSD([sQuery(id+"F0.wireOp",EDGE,"E339")])],"isStart":false});
            var Q20;
            Q20=makeQuery(id+"F1.opExtrude","CAP_EDGE",EDGE,{"disambiguationData":[OSD([sQuery(id+"F0.wireOp",EDGE,"E340")])],"isStart":false});
            var Q21;
            Q21=makeQuery(id+"F1.opExtrude","CAP_EDGE",EDGE,{"disambiguationData":[OSD([sQuery(id+"F0.wireOp",EDGE,"E327")])],"isStart":false});
            var Q22;
            Q22=makeQuery(id+"F1.opExtrude","CAP_EDGE",EDGE,{"disambiguationData":[OSD([sQuery(id+"F0.wireOp",EDGE,"E326")])],"isStart":false});
            var Q23;
            Q23=makeQuery(id+"F1.opExtrude","CAP_EDGE",EDGE,{"disambiguationData":[OSD([sQuery(id+"F0.wireOp",EDGE,"E320")])],"isStart":false});
            var Q24;
            Q24=makeQuery(id+"F1.opExtrude","CAP_EDGE",EDGE,{"disambiguationData":[OSD([sQuery(id+"F0.wireOp",EDGE,"E319")])],"isStart":false});
            var Q25;
            Q25=makeQuery(id+"F1.opExtrude","CAP_EDGE",EDGE,{"disambiguationData":[OSD([sQuery(id+"F0.wireOp",EDGE,"E308")])],"isStart":false});
            var Q26;
            Q26=makeQuery(id+"F1.opExtrude","CAP_EDGE",EDGE,{"disambiguationData":[OSD([sQuery(id+"F0.wireOp",EDGE,"E307")])],"isStart":false});
            var Q27;
            Q27=makeQuery(id+"F1.opExtrude","CAP_EDGE",EDGE,{"disambiguationData":[OSD([sQuery(id+"F0.wireOp",EDGE,"E301")])],"isStart":false});
            var Q28;
            Q28=makeQuery(id+"F1.opExtrude","CAP_EDGE",EDGE,{"disambiguationData":[OSD([sQuery(id+"F0.wireOp",EDGE,"E302")])],"isStart":false});
            var Q29;
            Q29=makeQuery(id+"F1.opExtrude","CAP_EDGE",EDGE,{"disambiguationData":[OSD([sQuery(id+"F0.wireOp",EDGE,"E288")])],"isStart":false});
            var Q30;
            Q30=makeQuery(id+"F1.opExtrude","CAP_EDGE",EDGE,{"disambiguationData":[OSD([sQuery(id+"F0.wireOp",EDGE,"E289")])],"isStart":false});
            var Q31;
            Q31=makeQuery(id+"F1.opExtrude","CAP_EDGE",EDGE,{"disambiguationData":[OSD([sQuery(id+"F0.wireOp",EDGE,"E282")])],"isStart":false});
            var Q32;
            Q32=makeQuery(id+"F1.opExtrude","CAP_EDGE",EDGE,{"disambiguationData":[OSD([sQuery(id+"F0.wireOp",EDGE,"E283")])],"isStart":false});
            var Q33;
            Q33=makeQuery(id+"F1.opExtrude","CAP_EDGE",EDGE,{"disambiguationData":[OSD([sQuery(id+"F0.wireOp",EDGE,"E270")])],"isStart":false});
            var Q34;
            Q34=makeQuery(id+"F1.opExtrude","CAP_EDGE",EDGE,{"disambiguationData":[OSD([sQuery(id+"F0.wireOp",EDGE,"E269")])],"isStart":false});
            var Q35;
            Q35=makeQuery(id+"F1.opExtrude","CAP_EDGE",EDGE,{"disambiguationData":[OSD([sQuery(id+"F0.wireOp",EDGE,"E263")])],"isStart":false});
            var Q36;
            Q36=makeQuery(id+"F1.opExtrude","CAP_EDGE",EDGE,{"disambiguationData":[OSD([sQuery(id+"F0.wireOp",EDGE,"E264")])],"isStart":false});
            var Q37;
            Q37=makeQuery(id+"F1.opExtrude","CAP_EDGE",EDGE,{"disambiguationData":[OSD([sQuery(id+"F0.wireOp",EDGE,"E251")])],"isStart":false});
            var Q38;
            Q38=makeQuery(id+"F1.opExtrude","CAP_EDGE",EDGE,{"disambiguationData":[OSD([sQuery(id+"F0.wireOp",EDGE,"E250")])],"isStart":false});
            chamfer(context, id + "F10", {"entities" : qUnion([Q0, Q1, Q2, Q3, Q4, Q5, Q6, Q7, Q8, Q9, Q10, Q11, Q12, Q13, Q14, Q15, Q16, Q17, Q18, Q19, Q20, Q21, Q22, Q23, Q24, Q25, Q26, Q27, Q28, Q29, Q30, Q31, Q32, Q33, Q34, Q35, Q36, Q37, Q38]), "width" : 0.3 * mm, "tangentPropagation" : true});
        }
        {
            var Q0;
            Q0=makeQuery(id+"F1.opExtrude","CAP_EDGE",EDGE,{"disambiguationData":[OSD([sQuery(id+"F0.wireOp",EDGE,"E243")])],"isStart":false});
            var Q1;
            Q1=makeQuery(id+"F1.opExtrude","CAP_EDGE",EDGE,{"disambiguationData":[OSD([sQuery(id+"F0.wireOp",EDGE,"E244")])],"isStart":false});
            var Q2;
            Q2=makeQuery(id+"F1.opExtrude","CAP_EDGE",EDGE,{"disambiguationData":[OSD([sQuery(id+"F0.wireOp",EDGE,"E232")])],"isStart":false});
            var Q3;
            Q3=makeQuery(id+"F1.opExtrude","CAP_EDGE",EDGE,{"disambiguationData":[OSD([sQuery(id+"F0.wireOp",EDGE,"E231")])],"isStart":false});
            var Q4;
            Q4=makeQuery(id+"F1.opExtrude","CAP_EDGE",EDGE,{"disambiguationData":[OSD([sQuery(id+"F0.wireOp",EDGE,"E225")])],"isStart":false});
            var Q5;
            Q5=makeQuery(id+"F1.opExtrude","CAP_EDGE",EDGE,{"disambiguationData":[OSD([sQuery(id+"F0.wireOp",EDGE,"E226")])],"isStart":false});
            var Q6;
            Q6=makeQuery(id+"F1.opExtrude","CAP_EDGE",EDGE,{"disambiguationData":[OSD([sQuery(id+"F0.wireOp",EDGE,"E213")])],"isStart":false});
            var Q7;
            Q7=makeQuery(id+"F1.opExtrude","CAP_EDGE",EDGE,{"disambiguationData":[OSD([sQuery(id+"F0.wireOp",EDGE,"E212")])],"isStart":false});
            var Q8;
            Q8=makeQuery(id+"F1.opExtrude","CAP_EDGE",EDGE,{"disambiguationData":[OSD([sQuery(id+"F0.wireOp",EDGE,"E207")])],"isStart":false});
            var Q9;
            Q9=makeQuery(id+"F1.opExtrude","CAP_EDGE",EDGE,{"disambiguationData":[OSD([sQuery(id+"F0.wireOp",EDGE,"E206")])],"isStart":false});
            var Q10;
            Q10=makeQuery(id+"F1.opExtrude","CAP_EDGE",EDGE,{"disambiguationData":[OSD([sQuery(id+"F0.wireOp",EDGE,"E195")])],"isStart":false});
            var Q11;
            Q11=makeQuery(id+"F1.opExtrude","CAP_EDGE",EDGE,{"disambiguationData":[OSD([sQuery(id+"F0.wireOp",EDGE,"E194")])],"isStart":false});
            var Q12;
            Q12=makeQuery(id+"F1.opExtrude","CAP_EDGE",EDGE,{"disambiguationData":[OSD([sQuery(id+"F0.wireOp",EDGE,"E187")])],"isStart":false});
            var Q13;
            Q13=makeQuery(id+"F1.opExtrude","CAP_EDGE",EDGE,{"disambiguationData":[OSD([sQuery(id+"F0.wireOp",EDGE,"E186")])],"isStart":false});
            var Q14;
            Q14=makeQuery(id+"F1.opExtrude","CAP_EDGE",EDGE,{"disambiguationData":[OSD([sQuery(id+"F0.wireOp",EDGE,"E176")])],"isStart":false});
            var Q15;
            Q15=makeQuery(id+"F1.opExtrude","CAP_EDGE",EDGE,{"disambiguationData":[OSD([sQuery(id+"F0.wireOp",EDGE,"E175")])],"isStart":false});
            var Q16;
            Q16=makeQuery(id+"F1.opExtrude","CAP_EDGE",EDGE,{"disambiguationData":[OSD([sQuery(id+"F0.wireOp",EDGE,"E168")])],"isStart":false});
            var Q17;
            Q17=makeQuery(id+"F1.opExtrude","CAP_EDGE",EDGE,{"disambiguationData":[OSD([sQuery(id+"F0.wireOp",EDGE,"E167")])],"isStart":false});
            var Q18;
            Q18=makeQuery(id+"F1.opExtrude","CAP_EDGE",EDGE,{"disambiguationData":[OSD([sQuery(id+"F0.wireOp",EDGE,"E157")])],"isStart":false});
            var Q19;
            Q19=makeQuery(id+"F1.opExtrude","CAP_EDGE",EDGE,{"disambiguationData":[OSD([sQuery(id+"F0.wireOp",EDGE,"E156")])],"isStart":false});
            var Q20;
            Q20=makeQuery(id+"F1.opExtrude","CAP_EDGE",EDGE,{"disambiguationData":[OSD([sQuery(id+"F0.wireOp",EDGE,"E149")])],"isStart":false});
            var Q21;
            Q21=makeQuery(id+"F1.opExtrude","CAP_EDGE",EDGE,{"disambiguationData":[OSD([sQuery(id+"F0.wireOp",EDGE,"E148")])],"isStart":false});
            var Q22;
            Q22=makeQuery(id+"F1.opExtrude","CAP_EDGE",EDGE,{"disambiguationData":[OSD([sQuery(id+"F0.wireOp",EDGE,"E137")])],"isStart":false});
            var Q23;
            Q23=makeQuery(id+"F1.opExtrude","CAP_EDGE",EDGE,{"disambiguationData":[OSD([sQuery(id+"F0.wireOp",EDGE,"E136")])],"isStart":false});
            var Q24;
            Q24=makeQuery(id+"F1.opExtrude","CAP_EDGE",EDGE,{"disambiguationData":[OSD([sQuery(id+"F0.wireOp",EDGE,"E130")])],"isStart":false});
            var Q25;
            Q25=makeQuery(id+"F1.opExtrude","CAP_EDGE",EDGE,{"disambiguationData":[OSD([sQuery(id+"F0.wireOp",EDGE,"E129")])],"isStart":false});
            var Q26;
            Q26=makeQuery(id+"F1.opExtrude","CAP_EDGE",EDGE,{"disambiguationData":[OSD([sQuery(id+"F0.wireOp",EDGE,"E119")])],"isStart":false});
            var Q27;
            Q27=makeQuery(id+"F1.opExtrude","CAP_EDGE",EDGE,{"disambiguationData":[OSD([sQuery(id+"F0.wireOp",EDGE,"E118")])],"isStart":false});
            var Q28;
            Q28=makeQuery(id+"F1.opExtrude","CAP_EDGE",EDGE,{"disambiguationData":[OSD([sQuery(id+"F0.wireOp",EDGE,"E110")])],"isStart":false});
            var Q29;
            Q29=makeQuery(id+"F1.opExtrude","CAP_EDGE",EDGE,{"disambiguationData":[OSD([sQuery(id+"F0.wireOp",EDGE,"E111")])],"isStart":false});
            var Q30;
            Q30=makeQuery(id+"F1.opExtrude","CAP_EDGE",EDGE,{"disambiguationData":[OSD([sQuery(id+"F0.wireOp",EDGE,"E99")])],"isStart":false});
            var Q31;
            Q31=makeQuery(id+"F1.opExtrude","CAP_EDGE",EDGE,{"disambiguationData":[OSD([sQuery(id+"F0.wireOp",EDGE,"E98")])],"isStart":false});
            chamfer(context, id + "F11", {"entities" : qUnion([Q0, Q1, Q2, Q3, Q4, Q5, Q6, Q7, Q8, Q9, Q10, Q11, Q12, Q13, Q14, Q15, Q16, Q17, Q18, Q19, Q20, Q21, Q22, Q23, Q24, Q25, Q26, Q27, Q28, Q29, Q30, Q31]), "width" : .3 * mm, "tangentPropagation" : true});
        }
        {
            var Q0;
            Q0=makeQuery(id+"F1.opExtrude","CAP_EDGE",EDGE,{"disambiguationData":[OSD([sQuery(id+"F0.wireOp",EDGE,"E92")])],"isStart":false});
            var Q1;
            Q1=makeQuery(id+"F1.opExtrude","CAP_EDGE",EDGE,{"disambiguationData":[OSD([sQuery(id+"F0.wireOp",EDGE,"E91")])],"isStart":false});
            var Q2;
            Q2=makeQuery(id+"F1.opExtrude","CAP_EDGE",EDGE,{"disambiguationData":[OSD([sQuery(id+"F0.wireOp",EDGE,"E80")])],"isStart":false});
            var Q3;
            Q3=makeQuery(id+"F1.opExtrude","CAP_EDGE",EDGE,{"disambiguationData":[OSD([sQuery(id+"F0.wireOp",EDGE,"E79")])],"isStart":false});
            var Q4;
            Q4=makeQuery(id+"F1.opExtrude","CAP_EDGE",EDGE,{"disambiguationData":[OSD([sQuery(id+"F0.wireOp",EDGE,"E74")])],"isStart":false});
            var Q5;
            Q5=makeQuery(id+"F1.opExtrude","CAP_EDGE",EDGE,{"disambiguationData":[OSD([sQuery(id+"F0.wireOp",EDGE,"E73")])],"isStart":false});
            var Q6;
            Q6=makeQuery(id+"F1.opExtrude","CAP_EDGE",EDGE,{"disambiguationData":[OSD([sQuery(id+"F0.wireOp",EDGE,"E60")])],"isStart":false});
            var Q7;
            Q7=makeQuery(id+"F1.opExtrude","CAP_EDGE",EDGE,{"disambiguationData":[OSD([sQuery(id+"F0.wireOp",EDGE,"E61")])],"isStart":false});
            var Q8;
            Q8=makeQuery(id+"F1.opExtrude","CAP_EDGE",EDGE,{"disambiguationData":[OSD([sQuery(id+"F0.wireOp",EDGE,"E55")])],"isStart":false});
            var Q9;
            Q9=makeQuery(id+"F1.opExtrude","CAP_EDGE",EDGE,{"disambiguationData":[OSD([sQuery(id+"F0.wireOp",EDGE,"E54")])],"isStart":false});
            var Q10;
            Q10=makeQuery(id+"F1.opExtrude","CAP_EDGE",EDGE,{"disambiguationData":[OSD([sQuery(id+"F0.wireOp",EDGE,"E41")])],"isStart":false});
            var Q11;
            Q11=makeQuery(id+"F1.opExtrude","CAP_EDGE",EDGE,{"disambiguationData":[OSD([sQuery(id+"F0.wireOp",EDGE,"E42")])],"isStart":false});
            var Q12;
            Q12=makeQuery(id+"F1.opExtrude","CAP_EDGE",EDGE,{"disambiguationData":[OSD([sQuery(id+"F0.wireOp",EDGE,"E36")])],"isStart":false});
            var Q13;
            Q13=makeQuery(id+"F1.opExtrude","CAP_EDGE",EDGE,{"disambiguationData":[OSD([sQuery(id+"F0.wireOp",EDGE,"E35")])],"isStart":false});
            var Q14;
            Q14=makeQuery(id+"F1.opExtrude","CAP_EDGE",EDGE,{"disambiguationData":[OSD([sQuery(id+"F0.wireOp",EDGE,"E23")])],"isStart":false});
            var Q15;
            Q15=makeQuery(id+"F1.opExtrude","CAP_EDGE",EDGE,{"disambiguationData":[OSD([sQuery(id+"F0.wireOp",EDGE,"E22")])],"isStart":false});
            var Q16;
            Q16=makeQuery(id+"F1.opExtrude","CAP_EDGE",EDGE,{"disambiguationData":[OSD([sQuery(id+"F0.wireOp",EDGE,"E16")])],"isStart":false});
            var Q17;
            Q17=makeQuery(id+"F1.opExtrude","CAP_EDGE",EDGE,{"disambiguationData":[OSD([sQuery(id+"F0.wireOp",EDGE,"E17")])],"isStart":false});
            var Q18;
            Q18=makeQuery(id+"F1.opExtrude","CAP_EDGE",EDGE,{"disambiguationData":[OSD([sQuery(id+"F0.wireOp",EDGE,"E4")])],"isStart":false});
            var Q19;
            Q19=makeQuery(id+"F1.opExtrude","CAP_EDGE",EDGE,{"disambiguationData":[OSD([sQuery(id+"F0.wireOp",EDGE,"E5")])],"isStart":false});
            var Q20;
            Q20=makeQuery(id+"F1.opExtrude","CAP_EDGE",EDGE,{"disambiguationData":[OSD([sQuery(id+"F0.wireOp",EDGE,"E909")])],"isStart":false});
            var Q21;
            Q21=makeQuery(id+"F1.opExtrude","CAP_EDGE",EDGE,{"disambiguationData":[OSD([sQuery(id+"F0.wireOp",EDGE,"E910")])],"isStart":false});
            var Q22;
            Q22=makeQuery(id+"F1.opExtrude","CAP_EDGE",EDGE,{"disambiguationData":[OSD([sQuery(id+"F0.wireOp",EDGE,"E897")])],"isStart":false});
            var Q23;
            Q23=makeQuery(id+"F1.opExtrude","CAP_EDGE",EDGE,{"disambiguationData":[OSD([sQuery(id+"F0.wireOp",EDGE,"E898")])],"isStart":false});
            chamfer(context, id + "F12", {"entities" : qUnion([Q0, Q1, Q2, Q3, Q4, Q5, Q6, Q7, Q8, Q9, Q10, Q11, Q12, Q13, Q14, Q15, Q16, Q17, Q18, Q19, Q20, Q21, Q22, Q23]), "width" : .3 * mm, "tangentPropagation" : true});
        }
        {
            var Q0;
            Q0=makeQuery(id+"F1.opExtrude","CAP_FACE",FACE,{"disambiguationData":[OSD([sQuery(id+"F0.wireOp",EDGE,"E0"),sQuery(id+"F0.wireOp",EDGE,"E1"),sQuery(id+"F0.wireOp",EDGE,"E2"),sQuery(id+"F0.wireOp",EDGE,"E3"),sQuery(id+"F0.wireOp",EDGE,"E4"),sQuery(id+"F0.wireOp",EDGE,"E5"),sQuery(id+"F0.wireOp",EDGE,"E6"),sQuery(id+"F0.wireOp",EDGE,"E7"),sQuery(id+"F0.wireOp",EDGE,"E8"),sQuery(id+"F0.wireOp",EDGE,"E9"),sQuery(id+"F0.wireOp",EDGE,"E10"),sQuery(id+"F0.wireOp",EDGE,"E11"),sQuery(id+"F0.wireOp",EDGE,"E12"),sQuery(id+"F0.wireOp",EDGE,"E13"),sQuery(id+"F0.wireOp",EDGE,"E14"),sQuery(id+"F0.wireOp",EDGE,"E15"),sQuery(id+"F0.wireOp",EDGE,"E16"),sQuery(id+"F0.wireOp",EDGE,"E17"),sQuery(id+"F0.wireOp",EDGE,"E18"),sQuery(id+"F0.wireOp",EDGE,"E19"),sQuery(id+"F0.wireOp",EDGE,"E20"),sQuery(id+"F0.wireOp",EDGE,"E21"),sQuery(id+"F0.wireOp",EDGE,"E22"),sQuery(id+"F0.wireOp",EDGE,"E23"),sQuery(id+"F0.wireOp",EDGE,"E24"),sQuery(id+"F0.wireOp",EDGE,"E25"),sQuery(id+"F0.wireOp",EDGE,"E26"),sQuery(id+"F0.wireOp",EDGE,"E27"),sQuery(id+"F0.wireOp",EDGE,"E28"),sQuery(id+"F0.wireOp",EDGE,"E29"),sQuery(id+"F0.wireOp",EDGE,"E30"),sQuery(id+"F0.wireOp",EDGE,"E31"),sQuery(id+"F0.wireOp",EDGE,"E32"),sQuery(id+"F0.wireOp",EDGE,"E33"),sQuery(id+"F0.wireOp",EDGE,"E34"),sQuery(id+"F0.wireOp",EDGE,"E35"),sQuery(id+"F0.wireOp",EDGE,"E36"),sQuery(id+"F0.wireOp",EDGE,"E37"),sQuery(id+"F0.wireOp",EDGE,"E38"),sQuery(id+"F0.wireOp",EDGE,"E39"),sQuery(id+"F0.wireOp",EDGE,"E40"),sQuery(id+"F0.wireOp",EDGE,"E41"),sQuery(id+"F0.wireOp",EDGE,"E42"),sQuery(id+"F0.wireOp",EDGE,"E43"),sQuery(id+"F0.wireOp",EDGE,"E44"),sQuery(id+"F0.wireOp",EDGE,"E45"),sQuery(id+"F0.wireOp",EDGE,"E46"),sQuery(id+"F0.wireOp",EDGE,"E47"),sQuery(id+"F0.wireOp",EDGE,"E48"),sQuery(id+"F0.wireOp",EDGE,"E49"),sQuery(id+"F0.wireOp",EDGE,"E50"),sQuery(id+"F0.wireOp",EDGE,"E51"),sQuery(id+"F0.wireOp",EDGE,"E52"),sQuery(id+"F0.wireOp",EDGE,"E53"),sQuery(id+"F0.wireOp",EDGE,"E54"),sQuery(id+"F0.wireOp",EDGE,"E55"),sQuery(id+"F0.wireOp",EDGE,"E56"),sQuery(id+"F0.wireOp",EDGE,"E57"),sQuery(id+"F0.wireOp",EDGE,"E58"),sQuery(id+"F0.wireOp",EDGE,"E59"),sQuery(id+"F0.wireOp",EDGE,"E60"),sQuery(id+"F0.wireOp",EDGE,"E61"),sQuery(id+"F0.wireOp",EDGE,"E62"),sQuery(id+"F0.wireOp",EDGE,"E63"),sQuery(id+"F0.wireOp",EDGE,"E64"),sQuery(id+"F0.wireOp",EDGE,"E65"),sQuery(id+"F0.wireOp",EDGE,"E66"),sQuery(id+"F0.wireOp",EDGE,"E67"),sQuery(id+"F0.wireOp",EDGE,"E68"),sQuery(id+"F0.wireOp",EDGE,"E69"),sQuery(id+"F0.wireOp",EDGE,"E70"),sQuery(id+"F0.wireOp",EDGE,"E71"),sQuery(id+"F0.wireOp",EDGE,"E72"),sQuery(id+"F0.wireOp",EDGE,"E73"),sQuery(id+"F0.wireOp",EDGE,"E74"),sQuery(id+"F0.wireOp",EDGE,"E75"),sQuery(id+"F0.wireOp",EDGE,"E76"),sQuery(id+"F0.wireOp",EDGE,"E77"),sQuery(id+"F0.wireOp",EDGE,"E78"),sQuery(id+"F0.wireOp",EDGE,"E79"),sQuery(id+"F0.wireOp",EDGE,"E80"),sQuery(id+"F0.wireOp",EDGE,"E81"),sQuery(id+"F0.wireOp",EDGE,"E82"),sQuery(id+"F0.wireOp",EDGE,"E83"),sQuery(id+"F0.wireOp",EDGE,"E84"),sQuery(id+"F0.wireOp",EDGE,"E85"),sQuery(id+"F0.wireOp",EDGE,"E86"),sQuery(id+"F0.wireOp",EDGE,"E87"),sQuery(id+"F0.wireOp",EDGE,"E88"),sQuery(id+"F0.wireOp",EDGE,"E89"),sQuery(id+"F0.wireOp",EDGE,"E90"),sQuery(id+"F0.wireOp",EDGE,"E91"),sQuery(id+"F0.wireOp",EDGE,"E92"),sQuery(id+"F0.wireOp",EDGE,"E93"),sQuery(id+"F0.wireOp",EDGE,"E94"),sQuery(id+"F0.wireOp",EDGE,"E95"),sQuery(id+"F0.wireOp",EDGE,"E96"),sQuery(id+"F0.wireOp",EDGE,"E97"),sQuery(id+"F0.wireOp",EDGE,"E98"),sQuery(id+"F0.wireOp",EDGE,"E99"),sQuery(id+"F0.wireOp",EDGE,"E100"),sQuery(id+"F0.wireOp",EDGE,"E101"),sQuery(id+"F0.wireOp",EDGE,"E102"),sQuery(id+"F0.wireOp",EDGE,"E103"),sQuery(id+"F0.wireOp",EDGE,"E104"),sQuery(id+"F0.wireOp",EDGE,"E105"),sQuery(id+"F0.wireOp",EDGE,"E106"),sQuery(id+"F0.wireOp",EDGE,"E107"),sQuery(id+"F0.wireOp",EDGE,"E108"),sQuery(id+"F0.wireOp",EDGE,"E109"),sQuery(id+"F0.wireOp",EDGE,"E110"),sQuery(id+"F0.wireOp",EDGE,"E111"),sQuery(id+"F0.wireOp",EDGE,"E112"),sQuery(id+"F0.wireOp",EDGE,"E113"),sQuery(id+"F0.wireOp",EDGE,"E114"),sQuery(id+"F0.wireOp",EDGE,"E115"),sQuery(id+"F0.wireOp",EDGE,"E116"),sQuery(id+"F0.wireOp",EDGE,"E117"),sQuery(id+"F0.wireOp",EDGE,"E118"),sQuery(id+"F0.wireOp",EDGE,"E119"),sQuery(id+"F0.wireOp",EDGE,"E120"),sQuery(id+"F0.wireOp",EDGE,"E121"),sQuery(id+"F0.wireOp",EDGE,"E122"),sQuery(id+"F0.wireOp",EDGE,"E123"),sQuery(id+"F0.wireOp",EDGE,"E124"),sQuery(id+"F0.wireOp",EDGE,"E125"),sQuery(id+"F0.wireOp",EDGE,"E126"),sQuery(id+"F0.wireOp",EDGE,"E127"),sQuery(id+"F0.wireOp",EDGE,"E128"),sQuery(id+"F0.wireOp",EDGE,"E129"),sQuery(id+"F0.wireOp",EDGE,"E130"),sQuery(id+"F0.wireOp",EDGE,"E131"),sQuery(id+"F0.wireOp",EDGE,"E132"),sQuery(id+"F0.wireOp",EDGE,"E133"),sQuery(id+"F0.wireOp",EDGE,"E134"),sQuery(id+"F0.wireOp",EDGE,"E135"),sQuery(id+"F0.wireOp",EDGE,"E136"),sQuery(id+"F0.wireOp",EDGE,"E137"),sQuery(id+"F0.wireOp",EDGE,"E138"),sQuery(id+"F0.wireOp",EDGE,"E139"),sQuery(id+"F0.wireOp",EDGE,"E140"),sQuery(id+"F0.wireOp",EDGE,"E141"),sQuery(id+"F0.wireOp",EDGE,"E142"),sQuery(id+"F0.wireOp",EDGE,"E143"),sQuery(id+"F0.wireOp",EDGE,"E144"),sQuery(id+"F0.wireOp",EDGE,"E145"),sQuery(id+"F0.wireOp",EDGE,"E146"),sQuery(id+"F0.wireOp",EDGE,"E147"),sQuery(id+"F0.wireOp",EDGE,"E148"),sQuery(id+"F0.wireOp",EDGE,"E149"),sQuery(id+"F0.wireOp",EDGE,"E150"),sQuery(id+"F0.wireOp",EDGE,"E151"),sQuery(id+"F0.wireOp",EDGE,"E152"),sQuery(id+"F0.wireOp",EDGE,"E153"),sQuery(id+"F0.wireOp",EDGE,"E154"),sQuery(id+"F0.wireOp",EDGE,"E155"),sQuery(id+"F0.wireOp",EDGE,"E156"),sQuery(id+"F0.wireOp",EDGE,"E157"),sQuery(id+"F0.wireOp",EDGE,"E158"),sQuery(id+"F0.wireOp",EDGE,"E159"),sQuery(id+"F0.wireOp",EDGE,"E160"),sQuery(id+"F0.wireOp",EDGE,"E161"),sQuery(id+"F0.wireOp",EDGE,"E162"),sQuery(id+"F0.wireOp",EDGE,"E163"),sQuery(id+"F0.wireOp",EDGE,"E164"),sQuery(id+"F0.wireOp",EDGE,"E165"),sQuery(id+"F0.wireOp",EDGE,"E166"),sQuery(id+"F0.wireOp",EDGE,"E167"),sQuery(id+"F0.wireOp",EDGE,"E168"),sQuery(id+"F0.wireOp",EDGE,"E169"),sQuery(id+"F0.wireOp",EDGE,"E170"),sQuery(id+"F0.wireOp",EDGE,"E171"),sQuery(id+"F0.wireOp",EDGE,"E172"),sQuery(id+"F0.wireOp",EDGE,"E173"),sQuery(id+"F0.wireOp",EDGE,"E174"),sQuery(id+"F0.wireOp",EDGE,"E175"),sQuery(id+"F0.wireOp",EDGE,"E176"),sQuery(id+"F0.wireOp",EDGE,"E177"),sQuery(id+"F0.wireOp",EDGE,"E178"),sQuery(id+"F0.wireOp",EDGE,"E179"),sQuery(id+"F0.wireOp",EDGE,"E180"),sQuery(id+"F0.wireOp",EDGE,"E181"),sQuery(id+"F0.wireOp",EDGE,"E182"),sQuery(id+"F0.wireOp",EDGE,"E183"),sQuery(id+"F0.wireOp",EDGE,"E184"),sQuery(id+"F0.wireOp",EDGE,"E185"),sQuery(id+"F0.wireOp",EDGE,"E186"),sQuery(id+"F0.wireOp",EDGE,"E187"),sQuery(id+"F0.wireOp",EDGE,"E188"),sQuery(id+"F0.wireOp",EDGE,"E189"),sQuery(id+"F0.wireOp",EDGE,"E190"),sQuery(id+"F0.wireOp",EDGE,"E191"),sQuery(id+"F0.wireOp",EDGE,"E192"),sQuery(id+"F0.wireOp",EDGE,"E193"),sQuery(id+"F0.wireOp",EDGE,"E194"),sQuery(id+"F0.wireOp",EDGE,"E195"),sQuery(id+"F0.wireOp",EDGE,"E196"),sQuery(id+"F0.wireOp",EDGE,"E197"),sQuery(id+"F0.wireOp",EDGE,"E198"),sQuery(id+"F0.wireOp",EDGE,"E199"),sQuery(id+"F0.wireOp",EDGE,"E200"),sQuery(id+"F0.wireOp",EDGE,"E201"),sQuery(id+"F0.wireOp",EDGE,"E202"),sQuery(id+"F0.wireOp",EDGE,"E203"),sQuery(id+"F0.wireOp",EDGE,"E204"),sQuery(id+"F0.wireOp",EDGE,"E205"),sQuery(id+"F0.wireOp",EDGE,"E206"),sQuery(id+"F0.wireOp",EDGE,"E207"),sQuery(id+"F0.wireOp",EDGE,"E208"),sQuery(id+"F0.wireOp",EDGE,"E209"),sQuery(id+"F0.wireOp",EDGE,"E210"),sQuery(id+"F0.wireOp",EDGE,"E211"),sQuery(id+"F0.wireOp",EDGE,"E212"),sQuery(id+"F0.wireOp",EDGE,"E213"),sQuery(id+"F0.wireOp",EDGE,"E214"),sQuery(id+"F0.wireOp",EDGE,"E215"),sQuery(id+"F0.wireOp",EDGE,"E216"),sQuery(id+"F0.wireOp",EDGE,"E217"),sQuery(id+"F0.wireOp",EDGE,"E218"),sQuery(id+"F0.wireOp",EDGE,"E219"),sQuery(id+"F0.wireOp",EDGE,"E220"),sQuery(id+"F0.wireOp",EDGE,"E221"),sQuery(id+"F0.wireOp",EDGE,"E222"),sQuery(id+"F0.wireOp",EDGE,"E223"),sQuery(id+"F0.wireOp",EDGE,"E224"),sQuery(id+"F0.wireOp",EDGE,"E225"),sQuery(id+"F0.wireOp",EDGE,"E226"),sQuery(id+"F0.wireOp",EDGE,"E227"),sQuery(id+"F0.wireOp",EDGE,"E228"),sQuery(id+"F0.wireOp",EDGE,"E229"),sQuery(id+"F0.wireOp",EDGE,"E230"),sQuery(id+"F0.wireOp",EDGE,"E231"),sQuery(id+"F0.wireOp",EDGE,"E232"),sQuery(id+"F0.wireOp",EDGE,"E233"),sQuery(id+"F0.wireOp",EDGE,"E234"),sQuery(id+"F0.wireOp",EDGE,"E235"),sQuery(id+"F0.wireOp",EDGE,"E236"),sQuery(id+"F0.wireOp",EDGE,"E237"),sQuery(id+"F0.wireOp",EDGE,"E238"),sQuery(id+"F0.wireOp",EDGE,"E239"),sQuery(id+"F0.wireOp",EDGE,"E240"),sQuery(id+"F0.wireOp",EDGE,"E241"),sQuery(id+"F0.wireOp",EDGE,"E242"),sQuery(id+"F0.wireOp",EDGE,"E243"),sQuery(id+"F0.wireOp",EDGE,"E244"),sQuery(id+"F0.wireOp",EDGE,"E245"),sQuery(id+"F0.wireOp",EDGE,"E246"),sQuery(id+"F0.wireOp",EDGE,"E247"),sQuery(id+"F0.wireOp",EDGE,"E248"),sQuery(id+"F0.wireOp",EDGE,"E249"),sQuery(id+"F0.wireOp",EDGE,"E250"),sQuery(id+"F0.wireOp",EDGE,"E251"),sQuery(id+"F0.wireOp",EDGE,"E252"),sQuery(id+"F0.wireOp",EDGE,"E253"),sQuery(id+"F0.wireOp",EDGE,"E254"),sQuery(id+"F0.wireOp",EDGE,"E255"),sQuery(id+"F0.wireOp",EDGE,"E256"),sQuery(id+"F0.wireOp",EDGE,"E257"),sQuery(id+"F0.wireOp",EDGE,"E258"),sQuery(id+"F0.wireOp",EDGE,"E259"),sQuery(id+"F0.wireOp",EDGE,"E260"),sQuery(id+"F0.wireOp",EDGE,"E261"),sQuery(id+"F0.wireOp",EDGE,"E262"),sQuery(id+"F0.wireOp",EDGE,"E263"),sQuery(id+"F0.wireOp",EDGE,"E264"),sQuery(id+"F0.wireOp",EDGE,"E265"),sQuery(id+"F0.wireOp",EDGE,"E266"),sQuery(id+"F0.wireOp",EDGE,"E267"),sQuery(id+"F0.wireOp",EDGE,"E268"),sQuery(id+"F0.wireOp",EDGE,"E269"),sQuery(id+"F0.wireOp",EDGE,"E270"),sQuery(id+"F0.wireOp",EDGE,"E271"),sQuery(id+"F0.wireOp",EDGE,"E272"),sQuery(id+"F0.wireOp",EDGE,"E273"),sQuery(id+"F0.wireOp",EDGE,"E274"),sQuery(id+"F0.wireOp",EDGE,"E275"),sQuery(id+"F0.wireOp",EDGE,"E276"),sQuery(id+"F0.wireOp",EDGE,"E277"),sQuery(id+"F0.wireOp",EDGE,"E278"),sQuery(id+"F0.wireOp",EDGE,"E279"),sQuery(id+"F0.wireOp",EDGE,"E280"),sQuery(id+"F0.wireOp",EDGE,"E281"),sQuery(id+"F0.wireOp",EDGE,"E282"),sQuery(id+"F0.wireOp",EDGE,"E283"),sQuery(id+"F0.wireOp",EDGE,"E284"),sQuery(id+"F0.wireOp",EDGE,"E285"),sQuery(id+"F0.wireOp",EDGE,"E286"),sQuery(id+"F0.wireOp",EDGE,"E287"),sQuery(id+"F0.wireOp",EDGE,"E288"),sQuery(id+"F0.wireOp",EDGE,"E289"),sQuery(id+"F0.wireOp",EDGE,"E290"),sQuery(id+"F0.wireOp",EDGE,"E291"),sQuery(id+"F0.wireOp",EDGE,"E292"),sQuery(id+"F0.wireOp",EDGE,"E293"),sQuery(id+"F0.wireOp",EDGE,"E294"),sQuery(id+"F0.wireOp",EDGE,"E295"),sQuery(id+"F0.wireOp",EDGE,"E296"),sQuery(id+"F0.wireOp",EDGE,"E297"),sQuery(id+"F0.wireOp",EDGE,"E298"),sQuery(id+"F0.wireOp",EDGE,"E299"),sQuery(id+"F0.wireOp",EDGE,"E300"),sQuery(id+"F0.wireOp",EDGE,"E301"),sQuery(id+"F0.wireOp",EDGE,"E302"),sQuery(id+"F0.wireOp",EDGE,"E303"),sQuery(id+"F0.wireOp",EDGE,"E304"),sQuery(id+"F0.wireOp",EDGE,"E305"),sQuery(id+"F0.wireOp",EDGE,"E306"),sQuery(id+"F0.wireOp",EDGE,"E307"),sQuery(id+"F0.wireOp",EDGE,"E308"),sQuery(id+"F0.wireOp",EDGE,"E309"),sQuery(id+"F0.wireOp",EDGE,"E310"),sQuery(id+"F0.wireOp",EDGE,"E311"),sQuery(id+"F0.wireOp",EDGE,"E312"),sQuery(id+"F0.wireOp",EDGE,"E313"),sQuery(id+"F0.wireOp",EDGE,"E314"),sQuery(id+"F0.wireOp",EDGE,"E315"),sQuery(id+"F0.wireOp",EDGE,"E316"),sQuery(id+"F0.wireOp",EDGE,"E317"),sQuery(id+"F0.wireOp",EDGE,"E318"),sQuery(id+"F0.wireOp",EDGE,"E319"),sQuery(id+"F0.wireOp",EDGE,"E320"),sQuery(id+"F0.wireOp",EDGE,"E321"),sQuery(id+"F0.wireOp",EDGE,"E322"),sQuery(id+"F0.wireOp",EDGE,"E323"),sQuery(id+"F0.wireOp",EDGE,"E324"),sQuery(id+"F0.wireOp",EDGE,"E325"),sQuery(id+"F0.wireOp",EDGE,"E326"),sQuery(id+"F0.wireOp",EDGE,"E327"),sQuery(id+"F0.wireOp",EDGE,"E328"),sQuery(id+"F0.wireOp",EDGE,"E329"),sQuery(id+"F0.wireOp",EDGE,"E330"),sQuery(id+"F0.wireOp",EDGE,"E331"),sQuery(id+"F0.wireOp",EDGE,"E332"),sQuery(id+"F0.wireOp",EDGE,"E333"),sQuery(id+"F0.wireOp",EDGE,"E334"),sQuery(id+"F0.wireOp",EDGE,"E335"),sQuery(id+"F0.wireOp",EDGE,"E336"),sQuery(id+"F0.wireOp",EDGE,"E337"),sQuery(id+"F0.wireOp",EDGE,"E338"),sQuery(id+"F0.wireOp",EDGE,"E339"),sQuery(id+"F0.wireOp",EDGE,"E340"),sQuery(id+"F0.wireOp",EDGE,"E341"),sQuery(id+"F0.wireOp",EDGE,"E342"),sQuery(id+"F0.wireOp",EDGE,"E343"),sQuery(id+"F0.wireOp",EDGE,"E344"),sQuery(id+"F0.wireOp",EDGE,"E345"),sQuery(id+"F0.wireOp",EDGE,"E346"),sQuery(id+"F0.wireOp",EDGE,"E347"),sQuery(id+"F0.wireOp",EDGE,"E348"),sQuery(id+"F0.wireOp",EDGE,"E349"),sQuery(id+"F0.wireOp",EDGE,"E350"),sQuery(id+"F0.wireOp",EDGE,"E351"),sQuery(id+"F0.wireOp",EDGE,"E352"),sQuery(id+"F0.wireOp",EDGE,"E353"),sQuery(id+"F0.wireOp",EDGE,"E354"),sQuery(id+"F0.wireOp",EDGE,"E355"),sQuery(id+"F0.wireOp",EDGE,"E356"),sQuery(id+"F0.wireOp",EDGE,"E357"),sQuery(id+"F0.wireOp",EDGE,"E358"),sQuery(id+"F0.wireOp",EDGE,"E359"),sQuery(id+"F0.wireOp",EDGE,"E360"),sQuery(id+"F0.wireOp",EDGE,"E361"),sQuery(id+"F0.wireOp",EDGE,"E362"),sQuery(id+"F0.wireOp",EDGE,"E363"),sQuery(id+"F0.wireOp",EDGE,"E364"),sQuery(id+"F0.wireOp",EDGE,"E365"),sQuery(id+"F0.wireOp",EDGE,"E366"),sQuery(id+"F0.wireOp",EDGE,"E367"),sQuery(id+"F0.wireOp",EDGE,"E368"),sQuery(id+"F0.wireOp",EDGE,"E369"),sQuery(id+"F0.wireOp",EDGE,"E370"),sQuery(id+"F0.wireOp",EDGE,"E371"),sQuery(id+"F0.wireOp",EDGE,"E372"),sQuery(id+"F0.wireOp",EDGE,"E373"),sQuery(id+"F0.wireOp",EDGE,"E374"),sQuery(id+"F0.wireOp",EDGE,"E375"),sQuery(id+"F0.wireOp",EDGE,"E376"),sQuery(id+"F0.wireOp",EDGE,"E377"),sQuery(id+"F0.wireOp",EDGE,"E378"),sQuery(id+"F0.wireOp",EDGE,"E379"),sQuery(id+"F0.wireOp",EDGE,"E380"),sQuery(id+"F0.wireOp",EDGE,"E381"),sQuery(id+"F0.wireOp",EDGE,"E382"),sQuery(id+"F0.wireOp",EDGE,"E383"),sQuery(id+"F0.wireOp",EDGE,"E384"),sQuery(id+"F0.wireOp",EDGE,"E385"),sQuery(id+"F0.wireOp",EDGE,"E386"),sQuery(id+"F0.wireOp",EDGE,"E387"),sQuery(id+"F0.wireOp",EDGE,"E388"),sQuery(id+"F0.wireOp",EDGE,"E389"),sQuery(id+"F0.wireOp",EDGE,"E390"),sQuery(id+"F0.wireOp",EDGE,"E391"),sQuery(id+"F0.wireOp",EDGE,"E392"),sQuery(id+"F0.wireOp",EDGE,"E393"),sQuery(id+"F0.wireOp",EDGE,"E394"),sQuery(id+"F0.wireOp",EDGE,"E395"),sQuery(id+"F0.wireOp",EDGE,"E396"),sQuery(id+"F0.wireOp",EDGE,"E397"),sQuery(id+"F0.wireOp",EDGE,"E398"),sQuery(id+"F0.wireOp",EDGE,"E399"),sQuery(id+"F0.wireOp",EDGE,"E400"),sQuery(id+"F0.wireOp",EDGE,"E401"),sQuery(id+"F0.wireOp",EDGE,"E402"),sQuery(id+"F0.wireOp",EDGE,"E403"),sQuery(id+"F0.wireOp",EDGE,"E404"),sQuery(id+"F0.wireOp",EDGE,"E405"),sQuery(id+"F0.wireOp",EDGE,"E406"),sQuery(id+"F0.wireOp",EDGE,"E407"),sQuery(id+"F0.wireOp",EDGE,"E408"),sQuery(id+"F0.wireOp",EDGE,"E409"),sQuery(id+"F0.wireOp",EDGE,"E410"),sQuery(id+"F0.wireOp",EDGE,"E411"),sQuery(id+"F0.wireOp",EDGE,"E412"),sQuery(id+"F0.wireOp",EDGE,"E413"),sQuery(id+"F0.wireOp",EDGE,"E414"),sQuery(id+"F0.wireOp",EDGE,"E415"),sQuery(id+"F0.wireOp",EDGE,"E416"),sQuery(id+"F0.wireOp",EDGE,"E417"),sQuery(id+"F0.wireOp",EDGE,"E418"),sQuery(id+"F0.wireOp",EDGE,"E419"),sQuery(id+"F0.wireOp",EDGE,"E420"),sQuery(id+"F0.wireOp",EDGE,"E421"),sQuery(id+"F0.wireOp",EDGE,"E422"),sQuery(id+"F0.wireOp",EDGE,"E423"),sQuery(id+"F0.wireOp",EDGE,"E424"),sQuery(id+"F0.wireOp",EDGE,"E425"),sQuery(id+"F0.wireOp",EDGE,"E426"),sQuery(id+"F0.wireOp",EDGE,"E427"),sQuery(id+"F0.wireOp",EDGE,"E428"),sQuery(id+"F0.wireOp",EDGE,"E429"),sQuery(id+"F0.wireOp",EDGE,"E430"),sQuery(id+"F0.wireOp",EDGE,"E431"),sQuery(id+"F0.wireOp",EDGE,"E432"),sQuery(id+"F0.wireOp",EDGE,"E433"),sQuery(id+"F0.wireOp",EDGE,"E434"),sQuery(id+"F0.wireOp",EDGE,"E435"),sQuery(id+"F0.wireOp",EDGE,"E436"),sQuery(id+"F0.wireOp",EDGE,"E437"),sQuery(id+"F0.wireOp",EDGE,"E438"),sQuery(id+"F0.wireOp",EDGE,"E439"),sQuery(id+"F0.wireOp",EDGE,"E440"),sQuery(id+"F0.wireOp",EDGE,"E441"),sQuery(id+"F0.wireOp",EDGE,"E442"),sQuery(id+"F0.wireOp",EDGE,"E443"),sQuery(id+"F0.wireOp",EDGE,"E444"),sQuery(id+"F0.wireOp",EDGE,"E445"),sQuery(id+"F0.wireOp",EDGE,"E446"),sQuery(id+"F0.wireOp",EDGE,"E447"),sQuery(id+"F0.wireOp",EDGE,"E448"),sQuery(id+"F0.wireOp",EDGE,"E449"),sQuery(id+"F0.wireOp",EDGE,"E450"),sQuery(id+"F0.wireOp",EDGE,"E451"),sQuery(id+"F0.wireOp",EDGE,"E452"),sQuery(id+"F0.wireOp",EDGE,"E453"),sQuery(id+"F0.wireOp",EDGE,"E454"),sQuery(id+"F0.wireOp",EDGE,"E455"),sQuery(id+"F0.wireOp",EDGE,"E456"),sQuery(id+"F0.wireOp",EDGE,"E457"),sQuery(id+"F0.wireOp",EDGE,"E458"),sQuery(id+"F0.wireOp",EDGE,"E459"),sQuery(id+"F0.wireOp",EDGE,"E460"),sQuery(id+"F0.wireOp",EDGE,"E461"),sQuery(id+"F0.wireOp",EDGE,"E462"),sQuery(id+"F0.wireOp",EDGE,"E463"),sQuery(id+"F0.wireOp",EDGE,"E464"),sQuery(id+"F0.wireOp",EDGE,"E465"),sQuery(id+"F0.wireOp",EDGE,"E466"),sQuery(id+"F0.wireOp",EDGE,"E467"),sQuery(id+"F0.wireOp",EDGE,"E468"),sQuery(id+"F0.wireOp",EDGE,"E469"),sQuery(id+"F0.wireOp",EDGE,"E470"),sQuery(id+"F0.wireOp",EDGE,"E471"),sQuery(id+"F0.wireOp",EDGE,"E472"),sQuery(id+"F0.wireOp",EDGE,"E473"),sQuery(id+"F0.wireOp",EDGE,"E474"),sQuery(id+"F0.wireOp",EDGE,"E475"),sQuery(id+"F0.wireOp",EDGE,"E476"),sQuery(id+"F0.wireOp",EDGE,"E477"),sQuery(id+"F0.wireOp",EDGE,"E478"),sQuery(id+"F0.wireOp",EDGE,"E479"),sQuery(id+"F0.wireOp",EDGE,"E480"),sQuery(id+"F0.wireOp",EDGE,"E481"),sQuery(id+"F0.wireOp",EDGE,"E482"),sQuery(id+"F0.wireOp",EDGE,"E483"),sQuery(id+"F0.wireOp",EDGE,"E484"),sQuery(id+"F0.wireOp",EDGE,"E485"),sQuery(id+"F0.wireOp",EDGE,"E486"),sQuery(id+"F0.wireOp",EDGE,"E487"),sQuery(id+"F0.wireOp",EDGE,"E488"),sQuery(id+"F0.wireOp",EDGE,"E489"),sQuery(id+"F0.wireOp",EDGE,"E490"),sQuery(id+"F0.wireOp",EDGE,"E491"),sQuery(id+"F0.wireOp",EDGE,"E492"),sQuery(id+"F0.wireOp",EDGE,"E493"),sQuery(id+"F0.wireOp",EDGE,"E494"),sQuery(id+"F0.wireOp",EDGE,"E495"),sQuery(id+"F0.wireOp",EDGE,"E496"),sQuery(id+"F0.wireOp",EDGE,"E497"),sQuery(id+"F0.wireOp",EDGE,"E498"),sQuery(id+"F0.wireOp",EDGE,"E499"),sQuery(id+"F0.wireOp",EDGE,"E500"),sQuery(id+"F0.wireOp",EDGE,"E501"),sQuery(id+"F0.wireOp",EDGE,"E502"),sQuery(id+"F0.wireOp",EDGE,"E503"),sQuery(id+"F0.wireOp",EDGE,"E504"),sQuery(id+"F0.wireOp",EDGE,"E505"),sQuery(id+"F0.wireOp",EDGE,"E506"),sQuery(id+"F0.wireOp",EDGE,"E507"),sQuery(id+"F0.wireOp",EDGE,"E508"),sQuery(id+"F0.wireOp",EDGE,"E509"),sQuery(id+"F0.wireOp",EDGE,"E510"),sQuery(id+"F0.wireOp",EDGE,"E511"),sQuery(id+"F0.wireOp",EDGE,"E512"),sQuery(id+"F0.wireOp",EDGE,"E513"),sQuery(id+"F0.wireOp",EDGE,"E514"),sQuery(id+"F0.wireOp",EDGE,"E515"),sQuery(id+"F0.wireOp",EDGE,"E516"),sQuery(id+"F0.wireOp",EDGE,"E517"),sQuery(id+"F0.wireOp",EDGE,"E518"),sQuery(id+"F0.wireOp",EDGE,"E519"),sQuery(id+"F0.wireOp",EDGE,"E520"),sQuery(id+"F0.wireOp",EDGE,"E521"),sQuery(id+"F0.wireOp",EDGE,"E522"),sQuery(id+"F0.wireOp",EDGE,"E523"),sQuery(id+"F0.wireOp",EDGE,"E524"),sQuery(id+"F0.wireOp",EDGE,"E525"),sQuery(id+"F0.wireOp",EDGE,"E526"),sQuery(id+"F0.wireOp",EDGE,"E527"),sQuery(id+"F0.wireOp",EDGE,"E528"),sQuery(id+"F0.wireOp",EDGE,"E529"),sQuery(id+"F0.wireOp",EDGE,"E530"),sQuery(id+"F0.wireOp",EDGE,"E531"),sQuery(id+"F0.wireOp",EDGE,"E532"),sQuery(id+"F0.wireOp",EDGE,"E533"),sQuery(id+"F0.wireOp",EDGE,"E534"),sQuery(id+"F0.wireOp",EDGE,"E535"),sQuery(id+"F0.wireOp",EDGE,"E536"),sQuery(id+"F0.wireOp",EDGE,"E537"),sQuery(id+"F0.wireOp",EDGE,"E538"),sQuery(id+"F0.wireOp",EDGE,"E539"),sQuery(id+"F0.wireOp",EDGE,"E540"),sQuery(id+"F0.wireOp",EDGE,"E541"),sQuery(id+"F0.wireOp",EDGE,"E542"),sQuery(id+"F0.wireOp",EDGE,"E543"),sQuery(id+"F0.wireOp",EDGE,"E544"),sQuery(id+"F0.wireOp",EDGE,"E545"),sQuery(id+"F0.wireOp",EDGE,"E546"),sQuery(id+"F0.wireOp",EDGE,"E547"),sQuery(id+"F0.wireOp",EDGE,"E548"),sQuery(id+"F0.wireOp",EDGE,"E549"),sQuery(id+"F0.wireOp",EDGE,"E550"),sQuery(id+"F0.wireOp",EDGE,"E551"),sQuery(id+"F0.wireOp",EDGE,"E552"),sQuery(id+"F0.wireOp",EDGE,"E553"),sQuery(id+"F0.wireOp",EDGE,"E554"),sQuery(id+"F0.wireOp",EDGE,"E555"),sQuery(id+"F0.wireOp",EDGE,"E556"),sQuery(id+"F0.wireOp",EDGE,"E557"),sQuery(id+"F0.wireOp",EDGE,"E558"),sQuery(id+"F0.wireOp",EDGE,"E559"),sQuery(id+"F0.wireOp",EDGE,"E560"),sQuery(id+"F0.wireOp",EDGE,"E561"),sQuery(id+"F0.wireOp",EDGE,"E562"),sQuery(id+"F0.wireOp",EDGE,"E563"),sQuery(id+"F0.wireOp",EDGE,"E564"),sQuery(id+"F0.wireOp",EDGE,"E565"),sQuery(id+"F0.wireOp",EDGE,"E566"),sQuery(id+"F0.wireOp",EDGE,"E567"),sQuery(id+"F0.wireOp",EDGE,"E568"),sQuery(id+"F0.wireOp",EDGE,"E569"),sQuery(id+"F0.wireOp",EDGE,"E570"),sQuery(id+"F0.wireOp",EDGE,"E571"),sQuery(id+"F0.wireOp",EDGE,"E572"),sQuery(id+"F0.wireOp",EDGE,"E573"),sQuery(id+"F0.wireOp",EDGE,"E574"),sQuery(id+"F0.wireOp",EDGE,"E575"),sQuery(id+"F0.wireOp",EDGE,"E576"),sQuery(id+"F0.wireOp",EDGE,"E577"),sQuery(id+"F0.wireOp",EDGE,"E578"),sQuery(id+"F0.wireOp",EDGE,"E579"),sQuery(id+"F0.wireOp",EDGE,"E580"),sQuery(id+"F0.wireOp",EDGE,"E581"),sQuery(id+"F0.wireOp",EDGE,"E582"),sQuery(id+"F0.wireOp",EDGE,"E583"),sQuery(id+"F0.wireOp",EDGE,"E584"),sQuery(id+"F0.wireOp",EDGE,"E585"),sQuery(id+"F0.wireOp",EDGE,"E586"),sQuery(id+"F0.wireOp",EDGE,"E587"),sQuery(id+"F0.wireOp",EDGE,"E588"),sQuery(id+"F0.wireOp",EDGE,"E589"),sQuery(id+"F0.wireOp",EDGE,"E590"),sQuery(id+"F0.wireOp",EDGE,"E591"),sQuery(id+"F0.wireOp",EDGE,"E592"),sQuery(id+"F0.wireOp",EDGE,"E593"),sQuery(id+"F0.wireOp",EDGE,"E594"),sQuery(id+"F0.wireOp",EDGE,"E595"),sQuery(id+"F0.wireOp",EDGE,"E596"),sQuery(id+"F0.wireOp",EDGE,"E597"),sQuery(id+"F0.wireOp",EDGE,"E598"),sQuery(id+"F0.wireOp",EDGE,"E599"),sQuery(id+"F0.wireOp",EDGE,"E600"),sQuery(id+"F0.wireOp",EDGE,"E601"),sQuery(id+"F0.wireOp",EDGE,"E602"),sQuery(id+"F0.wireOp",EDGE,"E603"),sQuery(id+"F0.wireOp",EDGE,"E604"),sQuery(id+"F0.wireOp",EDGE,"E605"),sQuery(id+"F0.wireOp",EDGE,"E606"),sQuery(id+"F0.wireOp",EDGE,"E607"),sQuery(id+"F0.wireOp",EDGE,"E608"),sQuery(id+"F0.wireOp",EDGE,"E609"),sQuery(id+"F0.wireOp",EDGE,"E610"),sQuery(id+"F0.wireOp",EDGE,"E611"),sQuery(id+"F0.wireOp",EDGE,"E612"),sQuery(id+"F0.wireOp",EDGE,"E613"),sQuery(id+"F0.wireOp",EDGE,"E614"),sQuery(id+"F0.wireOp",EDGE,"E615"),sQuery(id+"F0.wireOp",EDGE,"E616"),sQuery(id+"F0.wireOp",EDGE,"E617"),sQuery(id+"F0.wireOp",EDGE,"E618"),sQuery(id+"F0.wireOp",EDGE,"E619"),sQuery(id+"F0.wireOp",EDGE,"E620"),sQuery(id+"F0.wireOp",EDGE,"E621"),sQuery(id+"F0.wireOp",EDGE,"E622"),sQuery(id+"F0.wireOp",EDGE,"E623"),sQuery(id+"F0.wireOp",EDGE,"E624"),sQuery(id+"F0.wireOp",EDGE,"E625"),sQuery(id+"F0.wireOp",EDGE,"E626"),sQuery(id+"F0.wireOp",EDGE,"E627"),sQuery(id+"F0.wireOp",EDGE,"E628"),sQuery(id+"F0.wireOp",EDGE,"E629"),sQuery(id+"F0.wireOp",EDGE,"E630"),sQuery(id+"F0.wireOp",EDGE,"E631"),sQuery(id+"F0.wireOp",EDGE,"E632"),sQuery(id+"F0.wireOp",EDGE,"E633"),sQuery(id+"F0.wireOp",EDGE,"E634"),sQuery(id+"F0.wireOp",EDGE,"E635"),sQuery(id+"F0.wireOp",EDGE,"E636"),sQuery(id+"F0.wireOp",EDGE,"E637"),sQuery(id+"F0.wireOp",EDGE,"E638"),sQuery(id+"F0.wireOp",EDGE,"E639"),sQuery(id+"F0.wireOp",EDGE,"E640"),sQuery(id+"F0.wireOp",EDGE,"E641"),sQuery(id+"F0.wireOp",EDGE,"E642"),sQuery(id+"F0.wireOp",EDGE,"E643"),sQuery(id+"F0.wireOp",EDGE,"E644"),sQuery(id+"F0.wireOp",EDGE,"E645"),sQuery(id+"F0.wireOp",EDGE,"E646"),sQuery(id+"F0.wireOp",EDGE,"E647"),sQuery(id+"F0.wireOp",EDGE,"E648"),sQuery(id+"F0.wireOp",EDGE,"E649"),sQuery(id+"F0.wireOp",EDGE,"E650"),sQuery(id+"F0.wireOp",EDGE,"E651"),sQuery(id+"F0.wireOp",EDGE,"E652"),sQuery(id+"F0.wireOp",EDGE,"E653"),sQuery(id+"F0.wireOp",EDGE,"E654"),sQuery(id+"F0.wireOp",EDGE,"E655"),sQuery(id+"F0.wireOp",EDGE,"E656"),sQuery(id+"F0.wireOp",EDGE,"E657"),sQuery(id+"F0.wireOp",EDGE,"E658"),sQuery(id+"F0.wireOp",EDGE,"E659"),sQuery(id+"F0.wireOp",EDGE,"E660"),sQuery(id+"F0.wireOp",EDGE,"E661"),sQuery(id+"F0.wireOp",EDGE,"E662"),sQuery(id+"F0.wireOp",EDGE,"E663"),sQuery(id+"F0.wireOp",EDGE,"E664"),sQuery(id+"F0.wireOp",EDGE,"E665"),sQuery(id+"F0.wireOp",EDGE,"E666"),sQuery(id+"F0.wireOp",EDGE,"E667"),sQuery(id+"F0.wireOp",EDGE,"E668"),sQuery(id+"F0.wireOp",EDGE,"E669"),sQuery(id+"F0.wireOp",EDGE,"E670"),sQuery(id+"F0.wireOp",EDGE,"E671"),sQuery(id+"F0.wireOp",EDGE,"E672"),sQuery(id+"F0.wireOp",EDGE,"E673"),sQuery(id+"F0.wireOp",EDGE,"E674"),sQuery(id+"F0.wireOp",EDGE,"E675"),sQuery(id+"F0.wireOp",EDGE,"E676"),sQuery(id+"F0.wireOp",EDGE,"E677"),sQuery(id+"F0.wireOp",EDGE,"E678"),sQuery(id+"F0.wireOp",EDGE,"E679"),sQuery(id+"F0.wireOp",EDGE,"E680"),sQuery(id+"F0.wireOp",EDGE,"E681"),sQuery(id+"F0.wireOp",EDGE,"E682"),sQuery(id+"F0.wireOp",EDGE,"E683"),sQuery(id+"F0.wireOp",EDGE,"E684"),sQuery(id+"F0.wireOp",EDGE,"E685"),sQuery(id+"F0.wireOp",EDGE,"E686"),sQuery(id+"F0.wireOp",EDGE,"E687"),sQuery(id+"F0.wireOp",EDGE,"E688"),sQuery(id+"F0.wireOp",EDGE,"E689"),sQuery(id+"F0.wireOp",EDGE,"E690"),sQuery(id+"F0.wireOp",EDGE,"E691"),sQuery(id+"F0.wireOp",EDGE,"E692"),sQuery(id+"F0.wireOp",EDGE,"E693"),sQuery(id+"F0.wireOp",EDGE,"E694"),sQuery(id+"F0.wireOp",EDGE,"E695"),sQuery(id+"F0.wireOp",EDGE,"E696"),sQuery(id+"F0.wireOp",EDGE,"E697"),sQuery(id+"F0.wireOp",EDGE,"E698"),sQuery(id+"F0.wireOp",EDGE,"E699"),sQuery(id+"F0.wireOp",EDGE,"E700"),sQuery(id+"F0.wireOp",EDGE,"E701"),sQuery(id+"F0.wireOp",EDGE,"E702"),sQuery(id+"F0.wireOp",EDGE,"E703"),sQuery(id+"F0.wireOp",EDGE,"E704"),sQuery(id+"F0.wireOp",EDGE,"E705"),sQuery(id+"F0.wireOp",EDGE,"E706"),sQuery(id+"F0.wireOp",EDGE,"E707"),sQuery(id+"F0.wireOp",EDGE,"E708"),sQuery(id+"F0.wireOp",EDGE,"E709"),sQuery(id+"F0.wireOp",EDGE,"E710"),sQuery(id+"F0.wireOp",EDGE,"E711"),sQuery(id+"F0.wireOp",EDGE,"E712"),sQuery(id+"F0.wireOp",EDGE,"E713"),sQuery(id+"F0.wireOp",EDGE,"E714"),sQuery(id+"F0.wireOp",EDGE,"E715"),sQuery(id+"F0.wireOp",EDGE,"E716"),sQuery(id+"F0.wireOp",EDGE,"E717"),sQuery(id+"F0.wireOp",EDGE,"E718"),sQuery(id+"F0.wireOp",EDGE,"E719"),sQuery(id+"F0.wireOp",EDGE,"E720"),sQuery(id+"F0.wireOp",EDGE,"E721"),sQuery(id+"F0.wireOp",EDGE,"E722"),sQuery(id+"F0.wireOp",EDGE,"E723"),sQuery(id+"F0.wireOp",EDGE,"E724"),sQuery(id+"F0.wireOp",EDGE,"E725"),sQuery(id+"F0.wireOp",EDGE,"E726"),sQuery(id+"F0.wireOp",EDGE,"E727"),sQuery(id+"F0.wireOp",EDGE,"E728"),sQuery(id+"F0.wireOp",EDGE,"E729"),sQuery(id+"F0.wireOp",EDGE,"E730"),sQuery(id+"F0.wireOp",EDGE,"E731"),sQuery(id+"F0.wireOp",EDGE,"E732"),sQuery(id+"F0.wireOp",EDGE,"E733"),sQuery(id+"F0.wireOp",EDGE,"E734"),sQuery(id+"F0.wireOp",EDGE,"E735"),sQuery(id+"F0.wireOp",EDGE,"E736"),sQuery(id+"F0.wireOp",EDGE,"E737"),sQuery(id+"F0.wireOp",EDGE,"E738"),sQuery(id+"F0.wireOp",EDGE,"E739"),sQuery(id+"F0.wireOp",EDGE,"E740"),sQuery(id+"F0.wireOp",EDGE,"E741"),sQuery(id+"F0.wireOp",EDGE,"E742"),sQuery(id+"F0.wireOp",EDGE,"E743"),sQuery(id+"F0.wireOp",EDGE,"E744"),sQuery(id+"F0.wireOp",EDGE,"E745"),sQuery(id+"F0.wireOp",EDGE,"E746"),sQuery(id+"F0.wireOp",EDGE,"E747"),sQuery(id+"F0.wireOp",EDGE,"E748"),sQuery(id+"F0.wireOp",EDGE,"E749"),sQuery(id+"F0.wireOp",EDGE,"E750"),sQuery(id+"F0.wireOp",EDGE,"E751"),sQuery(id+"F0.wireOp",EDGE,"E752"),sQuery(id+"F0.wireOp",EDGE,"E753"),sQuery(id+"F0.wireOp",EDGE,"E754"),sQuery(id+"F0.wireOp",EDGE,"E755"),sQuery(id+"F0.wireOp",EDGE,"E756"),sQuery(id+"F0.wireOp",EDGE,"E757"),sQuery(id+"F0.wireOp",EDGE,"E758"),sQuery(id+"F0.wireOp",EDGE,"E759"),sQuery(id+"F0.wireOp",EDGE,"E760"),sQuery(id+"F0.wireOp",EDGE,"E761"),sQuery(id+"F0.wireOp",EDGE,"E762"),sQuery(id+"F0.wireOp",EDGE,"E763"),sQuery(id+"F0.wireOp",EDGE,"E764"),sQuery(id+"F0.wireOp",EDGE,"E765"),sQuery(id+"F0.wireOp",EDGE,"E766"),sQuery(id+"F0.wireOp",EDGE,"E767"),sQuery(id+"F0.wireOp",EDGE,"E768"),sQuery(id+"F0.wireOp",EDGE,"E769"),sQuery(id+"F0.wireOp",EDGE,"E770"),sQuery(id+"F0.wireOp",EDGE,"E771"),sQuery(id+"F0.wireOp",EDGE,"E772"),sQuery(id+"F0.wireOp",EDGE,"E773"),sQuery(id+"F0.wireOp",EDGE,"E774"),sQuery(id+"F0.wireOp",EDGE,"E775"),sQuery(id+"F0.wireOp",EDGE,"E776"),sQuery(id+"F0.wireOp",EDGE,"E777"),sQuery(id+"F0.wireOp",EDGE,"E778"),sQuery(id+"F0.wireOp",EDGE,"E779"),sQuery(id+"F0.wireOp",EDGE,"E780"),sQuery(id+"F0.wireOp",EDGE,"E781"),sQuery(id+"F0.wireOp",EDGE,"E782"),sQuery(id+"F0.wireOp",EDGE,"E783"),sQuery(id+"F0.wireOp",EDGE,"E784"),sQuery(id+"F0.wireOp",EDGE,"E785"),sQuery(id+"F0.wireOp",EDGE,"E786"),sQuery(id+"F0.wireOp",EDGE,"E787"),sQuery(id+"F0.wireOp",EDGE,"E788"),sQuery(id+"F0.wireOp",EDGE,"E789"),sQuery(id+"F0.wireOp",EDGE,"E790"),sQuery(id+"F0.wireOp",EDGE,"E791"),sQuery(id+"F0.wireOp",EDGE,"E792"),sQuery(id+"F0.wireOp",EDGE,"E793"),sQuery(id+"F0.wireOp",EDGE,"E794"),sQuery(id+"F0.wireOp",EDGE,"E795"),sQuery(id+"F0.wireOp",EDGE,"E796"),sQuery(id+"F0.wireOp",EDGE,"E797"),sQuery(id+"F0.wireOp",EDGE,"E798"),sQuery(id+"F0.wireOp",EDGE,"E799"),sQuery(id+"F0.wireOp",EDGE,"E800"),sQuery(id+"F0.wireOp",EDGE,"E801"),sQuery(id+"F0.wireOp",EDGE,"E802"),sQuery(id+"F0.wireOp",EDGE,"E803"),sQuery(id+"F0.wireOp",EDGE,"E804"),sQuery(id+"F0.wireOp",EDGE,"E805"),sQuery(id+"F0.wireOp",EDGE,"E806"),sQuery(id+"F0.wireOp",EDGE,"E807"),sQuery(id+"F0.wireOp",EDGE,"E808"),sQuery(id+"F0.wireOp",EDGE,"E809"),sQuery(id+"F0.wireOp",EDGE,"E810"),sQuery(id+"F0.wireOp",EDGE,"E811"),sQuery(id+"F0.wireOp",EDGE,"E812"),sQuery(id+"F0.wireOp",EDGE,"E813"),sQuery(id+"F0.wireOp",EDGE,"E814"),sQuery(id+"F0.wireOp",EDGE,"E815"),sQuery(id+"F0.wireOp",EDGE,"E816"),sQuery(id+"F0.wireOp",EDGE,"E817"),sQuery(id+"F0.wireOp",EDGE,"E818"),sQuery(id+"F0.wireOp",EDGE,"E819"),sQuery(id+"F0.wireOp",EDGE,"E820"),sQuery(id+"F0.wireOp",EDGE,"E821"),sQuery(id+"F0.wireOp",EDGE,"E822"),sQuery(id+"F0.wireOp",EDGE,"E823"),sQuery(id+"F0.wireOp",EDGE,"E824"),sQuery(id+"F0.wireOp",EDGE,"E825"),sQuery(id+"F0.wireOp",EDGE,"E826"),sQuery(id+"F0.wireOp",EDGE,"E827"),sQuery(id+"F0.wireOp",EDGE,"E828"),sQuery(id+"F0.wireOp",EDGE,"E829"),sQuery(id+"F0.wireOp",EDGE,"E830"),sQuery(id+"F0.wireOp",EDGE,"E831"),sQuery(id+"F0.wireOp",EDGE,"E832"),sQuery(id+"F0.wireOp",EDGE,"E833"),sQuery(id+"F0.wireOp",EDGE,"E834"),sQuery(id+"F0.wireOp",EDGE,"E835"),sQuery(id+"F0.wireOp",EDGE,"E836"),sQuery(id+"F0.wireOp",EDGE,"E837"),sQuery(id+"F0.wireOp",EDGE,"E838"),sQuery(id+"F0.wireOp",EDGE,"E839"),sQuery(id+"F0.wireOp",EDGE,"E840"),sQuery(id+"F0.wireOp",EDGE,"E841"),sQuery(id+"F0.wireOp",EDGE,"E842"),sQuery(id+"F0.wireOp",EDGE,"E843"),sQuery(id+"F0.wireOp",EDGE,"E844"),sQuery(id+"F0.wireOp",EDGE,"E845"),sQuery(id+"F0.wireOp",EDGE,"E846"),sQuery(id+"F0.wireOp",EDGE,"E847"),sQuery(id+"F0.wireOp",EDGE,"E848"),sQuery(id+"F0.wireOp",EDGE,"E849"),sQuery(id+"F0.wireOp",EDGE,"E850"),sQuery(id+"F0.wireOp",EDGE,"E851"),sQuery(id+"F0.wireOp",EDGE,"E852"),sQuery(id+"F0.wireOp",EDGE,"E853"),sQuery(id+"F0.wireOp",EDGE,"E854"),sQuery(id+"F0.wireOp",EDGE,"E855"),sQuery(id+"F0.wireOp",EDGE,"E856"),sQuery(id+"F0.wireOp",EDGE,"E857"),sQuery(id+"F0.wireOp",EDGE,"E858"),sQuery(id+"F0.wireOp",EDGE,"E859"),sQuery(id+"F0.wireOp",EDGE,"E860"),sQuery(id+"F0.wireOp",EDGE,"E861"),sQuery(id+"F0.wireOp",EDGE,"E862"),sQuery(id+"F0.wireOp",EDGE,"E863"),sQuery(id+"F0.wireOp",EDGE,"E864"),sQuery(id+"F0.wireOp",EDGE,"E865"),sQuery(id+"F0.wireOp",EDGE,"E866"),sQuery(id+"F0.wireOp",EDGE,"E867"),sQuery(id+"F0.wireOp",EDGE,"E868"),sQuery(id+"F0.wireOp",EDGE,"E869"),sQuery(id+"F0.wireOp",EDGE,"E870"),sQuery(id+"F0.wireOp",EDGE,"E871"),sQuery(id+"F0.wireOp",EDGE,"E872"),sQuery(id+"F0.wireOp",EDGE,"E873"),sQuery(id+"F0.wireOp",EDGE,"E874"),sQuery(id+"F0.wireOp",EDGE,"E875"),sQuery(id+"F0.wireOp",EDGE,"E876"),sQuery(id+"F0.wireOp",EDGE,"E877"),sQuery(id+"F0.wireOp",EDGE,"E878"),sQuery(id+"F0.wireOp",EDGE,"E879"),sQuery(id+"F0.wireOp",EDGE,"E880"),sQuery(id+"F0.wireOp",EDGE,"E881"),sQuery(id+"F0.wireOp",EDGE,"E882"),sQuery(id+"F0.wireOp",EDGE,"E883"),sQuery(id+"F0.wireOp",EDGE,"E884"),sQuery(id+"F0.wireOp",EDGE,"E885"),sQuery(id+"F0.wireOp",EDGE,"E886"),sQuery(id+"F0.wireOp",EDGE,"E887"),sQuery(id+"F0.wireOp",EDGE,"E888"),sQuery(id+"F0.wireOp",EDGE,"E889"),sQuery(id+"F0.wireOp",EDGE,"E890"),sQuery(id+"F0.wireOp",EDGE,"E891"),sQuery(id+"F0.wireOp",EDGE,"E892"),sQuery(id+"F0.wireOp",EDGE,"E893"),sQuery(id+"F0.wireOp",EDGE,"E894"),sQuery(id+"F0.wireOp",EDGE,"E895"),sQuery(id+"F0.wireOp",EDGE,"E896"),sQuery(id+"F0.wireOp",EDGE,"E897"),sQuery(id+"F0.wireOp",EDGE,"E898"),sQuery(id+"F0.wireOp",EDGE,"E899"),sQuery(id+"F0.wireOp",EDGE,"E900"),sQuery(id+"F0.wireOp",EDGE,"E901"),sQuery(id+"F0.wireOp",EDGE,"E902"),sQuery(id+"F0.wireOp",EDGE,"E903"),sQuery(id+"F0.wireOp",EDGE,"E904"),sQuery(id+"F0.wireOp",EDGE,"E905"),sQuery(id+"F0.wireOp",EDGE,"E906"),sQuery(id+"F0.wireOp",EDGE,"E907"),sQuery(id+"F0.wireOp",EDGE,"E908"),sQuery(id+"F0.wireOp",EDGE,"E909"),sQuery(id+"F0.wireOp",EDGE,"E910"),sQuery(id+"F0.wireOp",EDGE,"E911"),sQuery(id+"F0.wireOp",EDGE,"E943")])],"isStart":false});
            var sketch = newSketch(context, id + "F13", { "sketchPlane" : qUnion([Q0])});
            skText(sketch, "E950", { "text": "PMG ", "fontName": "OpenSans-Regular.ttf"});
            const initialGuessF13  = {"E950": [-0.0012, -0.0144, 1, 0, 0.00082]};
            skSetInitialGuess(sketch, initialGuessF13);
            skSolve(sketch);
        }
        {
            var Q0;
            Q0 = qSketchRegion(id + "F13", true);
            extrude(context, id + "F14", {"entities" : qUnion([Q0]), "operationType" : NewBodyOperationType.REMOVE, "oppositeDirection" : true, "depth" : 0.2 * mm, "offsetDistance" : 25 * mm});
        }
        {
            var Q0;
            Q0=makeQuery(id+"F4.opExtrude","CAP_FACE",FACE,{"disambiguationData":[OSD([sQuery(id+"F3.wireOp",EDGE,"E944")])],"isStart":false});
            var sketch = newSketch(context, id + "F15", { "sketchPlane" : qUnion([Q0])});
            skCircle(sketch, "E951", {"center": v(-9.45, 6.08) * mm, "radius": 0.5 * mm});
            skCircle(sketch, "E952", {"center": v(-6.98, 6.08) * mm, "radius": 0.5 * mm});
            skCircle(sketch, "E953", {"center": v(-4.08, 6.08) * mm, "radius": 0.5 * mm});
            skCircle(sketch, "E954", {"center": v(-1.48, 6.08) * mm, "radius": 0.5 * mm});
            skCircle(sketch, "E955", {"center": v(1.27, 6.08) * mm, "radius": 0.5 * mm});
            skCircle(sketch, "E956", {"center": v(4.05, 6.08) * mm, "radius": 0.5 * mm});
            skCircle(sketch, "E957", {"center": v(6.7, 6.08) * mm, "radius": 0.5 * mm});
            skCircle(sketch, "E958", {"center": v(8.95, 6.08) * mm, "radius": 0.5 * mm});
            skCircle(sketch, "E959", {"center": v(-10.27, 3.59) * mm, "radius": 0.5 * mm});
            skCircle(sketch, "E960", {"center": v(-8.09, 3.59) * mm, "radius": 0.5 * mm});
            skCircle(sketch, "E961", {"center": v(-5.19, 3.59) * mm, "radius": 0.5 * mm});
            skCircle(sketch, "E962", {"center": v(-2.6, 3.59) * mm, "radius": 0.5 * mm});
            skCircle(sketch, "E963", {"center": v(0.16, 3.59) * mm, "radius": 0.5 * mm});
            skCircle(sketch, "E964", {"center": v(2.94, 3.59) * mm, "radius": 0.5 * mm});
            skCircle(sketch, "E965", {"center": v(5.6, 3.59) * mm, "radius": 0.5 * mm});
            skCircle(sketch, "E966", {"center": v(7.84, 3.59) * mm, "radius": 0.5 * mm});
            skCircle(sketch, "E967", {"center": v(-8.82, 1.1) * mm, "radius": 0.5 * mm});
            skCircle(sketch, "E968", {"center": v(-6.35, 1.1) * mm, "radius": 0.5 * mm});
            skCircle(sketch, "E969", {"center": v(-3.45, 1.1) * mm, "radius": 0.5 * mm});
            skCircle(sketch, "E970", {"center": v(-0.86, 1.1) * mm, "radius": 0.5 * mm});
            skCircle(sketch, "E971", {"center": v(1.9, 1.1) * mm, "radius": 0.5 * mm});
            skCircle(sketch, "E972", {"center": v(4.67, 1.1) * mm, "radius": 0.5 * mm});
            skCircle(sketch, "E973", {"center": v(7.33, 1.1) * mm, "radius": 0.5 * mm});
            skCircle(sketch, "E974", {"center": v(9.58, 1.1) * mm, "radius": 0.5 * mm});
            skCircle(sketch, "E975", {"center": v(-10.2, -1) * mm, "radius": 0.5 * mm});
            skCircle(sketch, "E976", {"center": v(-7.74, -1) * mm, "radius": 0.5 * mm});
            skCircle(sketch, "E977", {"center": v(-4.84, -1) * mm, "radius": 0.5 * mm});
            skCircle(sketch, "E978", {"center": v(-2.24, -1) * mm, "radius": 0.5 * mm});
            skCircle(sketch, "E979", {"center": v(0.5, -1) * mm, "radius": 0.5 * mm});
            skCircle(sketch, "E980", {"center": v(3.29, -1) * mm, "radius": 0.5 * mm});
            skCircle(sketch, "E981", {"center": v(5.94, -1) * mm, "radius": 0.5 * mm});
            skCircle(sketch, "E982", {"center": v(8.2, -1) * mm, "radius": 0.5 * mm});
            skCircle(sketch, "E983", {"center": v(-11.02, -3.5) * mm, "radius": 0.5 * mm});
            skCircle(sketch, "E984", {"center": v(-8.85, -3.5) * mm, "radius": 0.5 * mm});
            skCircle(sketch, "E985", {"center": v(-5.94, -3.5) * mm, "radius": 0.5 * mm});
            skCircle(sketch, "E986", {"center": v(-3.35, -3.5) * mm, "radius": 0.5 * mm});
            skCircle(sketch, "E987", {"center": v(-0.6, -3.5) * mm, "radius": 0.5 * mm});
            skCircle(sketch, "E988", {"center": v(2.18, -3.5) * mm, "radius": 0.5 * mm});
            skCircle(sketch, "E989", {"center": v(4.83, -3.5) * mm, "radius": 0.5 * mm});
            skCircle(sketch, "E990", {"center": v(7.08, -3.5) * mm, "radius": 0.5 * mm});
            skCircle(sketch, "E991", {"center": v(-9.58, -5.99) * mm, "radius": 0.5 * mm});
            skCircle(sketch, "E992", {"center": v(-7.11, -5.99) * mm, "radius": 0.5 * mm});
            skCircle(sketch, "E993", {"center": v(-4.2, -5.99) * mm, "radius": 0.5 * mm});
            skCircle(sketch, "E994", {"center": v(-1.61, -5.99) * mm, "radius": 0.5 * mm});
            skCircle(sketch, "E995", {"center": v(1.14, -5.99) * mm, "radius": 0.5 * mm});
            skCircle(sketch, "E996", {"center": v(3.91, -5.99) * mm, "radius": 0.5 * mm});
            skCircle(sketch, "E997", {"center": v(6.57, -5.99) * mm, "radius": 0.5 * mm});
            skCircle(sketch, "E998", {"center": v(8.82, -5.99) * mm, "radius": 0.5 * mm});
            skCircle(sketch, "E999", {"center": v(-5.7, -8.24) * mm, "radius": 0.5 * mm});
            skCircle(sketch, "E1000", {"center": v(-2.8, -8.24) * mm, "radius": 0.5 * mm});
            skCircle(sketch, "E1001", {"center": v(-0.2, -8.24) * mm, "radius": 0.5 * mm});
            skCircle(sketch, "E1002", {"center": v(2.55, -8.24) * mm, "radius": 0.5 * mm});
            skCircle(sketch, "E1003", {"center": v(5.33, -8.24) * mm, "radius": 0.5 * mm});
            skCircle(sketch, "E1004", {"center": v(-6.02, 8.81) * mm, "radius": 0.5 * mm});
            skCircle(sketch, "E1005", {"center": v(-3.12, 8.81) * mm, "radius": 0.5 * mm});
            skCircle(sketch, "E1006", {"center": v(-0.53, 8.81) * mm, "radius": 0.5 * mm});
            skCircle(sketch, "E1007", {"center": v(2.22, 8.81) * mm, "radius": 0.5 * mm});
            skCircle(sketch, "E1008", {"center": v(5, 8.81) * mm, "radius": 0.5 * mm});
            skCircle(sketch, "E1009", {"center": v(-2.47, -10.28) * mm, "radius": 0.5 * mm});
            skCircle(sketch, "E1010", {"center": v(1.5, -10.23) * mm, "radius": 0.5 * mm});
            skCircle(sketch, "E1011", {"center": v(0.95, 10.8) * mm, "radius": 0.5 * mm});
            skCircle(sketch, "E1012", {"center": v(-1.8, 10.8) * mm, "radius": 0.5 * mm});
            skCircle(sketch, "E1013", {"center": v(9.98, -3.6) * mm, "radius": 0.5 * mm});
            skSolve(sketch);
        }
        {
            var Q0;
            Q0 = qSketchRegion(id + "F15", true);
            extrude(context, id + "F16", {"entities" : qUnion([Q0]), "operationType" : NewBodyOperationType.ADD, "depth" : 0.2 * mm, "offsetDistance" : 25 * mm});
        }
        {
            var Q0;
            Q0=makeQuery(id+"F1.opExtrude","CAP_EDGE",EDGE,{"disambiguationData":[OSD([sQuery(id+"F0.wireOp",EDGE,"E943")])],"isStart":true});
            chamfer(context, id + "F17", {"entities" : qUnion([Q0]), "width" : 0.5 * mm, "tangentPropagation" : true});
        }
    });
